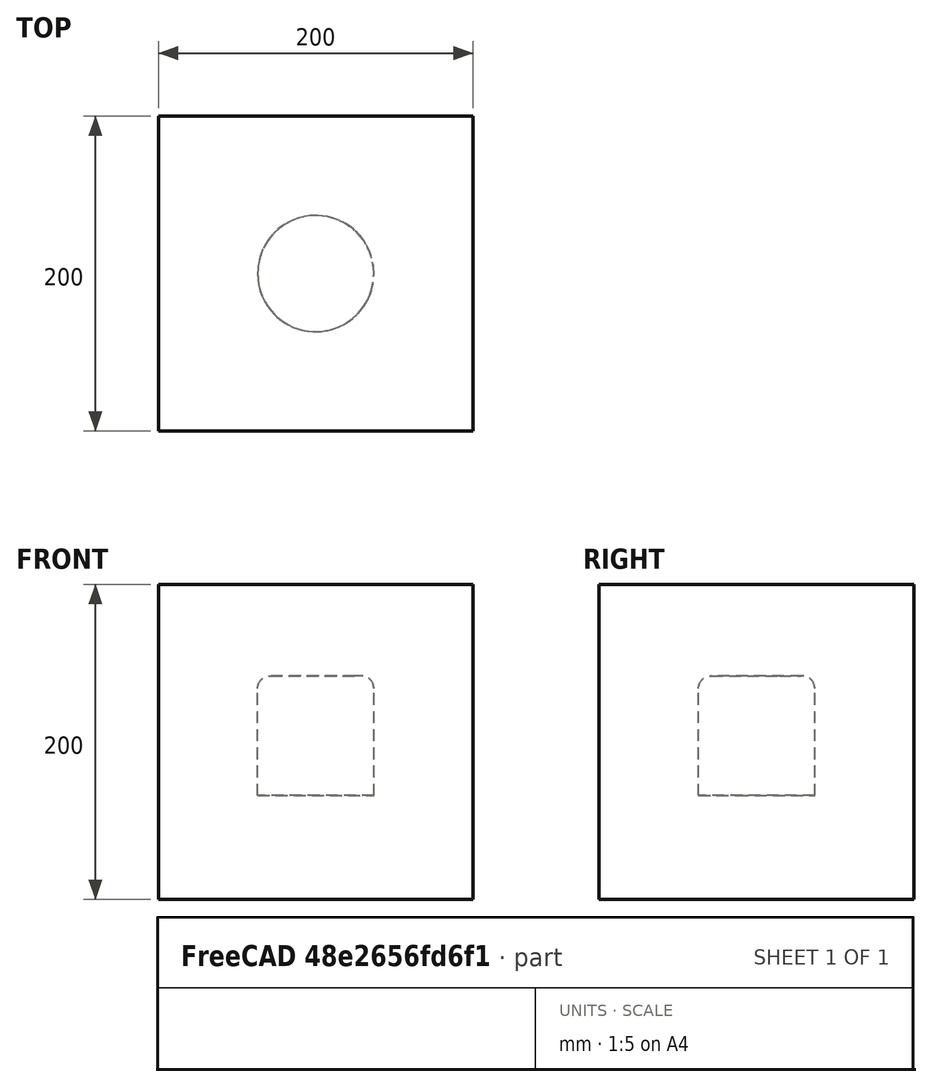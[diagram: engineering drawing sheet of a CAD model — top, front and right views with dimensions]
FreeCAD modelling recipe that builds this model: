
FCSTD DOCUMENT  (FreeCAD 0.21R33694 (Git))
Label: assemblyTest-B
License: All rights reserved
LicenseURL: http://en.wikipedia.org/wiki/All_rights_reserved
objects: App::DocumentObjectGroupPython×1254, Part::FeaturePython×4, App::Part×3, Part::Fuse×2
note: 6 computed .brp shape members not serialized (recipe doc carries the construction recipe); baked Part::Feature solids carry a one-line shape summary decoded from their .brp

FEATURE [App::DocumentObjectGroupPython] HALFPI  # scripted group (container) (typed FeaturePython)
  name = HALFPI
  value = pi/2.
FEATURE [App::DocumentObjectGroupPython] PI  # scripted group (container) (typed FeaturePython)
  name = PI
  value = 1.*pi
FEATURE [App::DocumentObjectGroupPython] TWOPI  # scripted group (container) (typed FeaturePython)
  name = TWOPI
  value = 2.*pi
FEATURE [App::DocumentObjectGroupPython] Variables  # scripted group (container) (typed FeaturePython)
FEATURE [App::DocumentObjectGroupPython] Quantities  # scripted group (container) (typed FeaturePython)
FEATURE [App::DocumentObjectGroupPython] Isotopes  # scripted group (container) (typed FeaturePython)
FEATURE [App::DocumentObjectGroupPython] Elements  # scripted group (container) (typed FeaturePython)
FEATURE [App::DocumentObjectGroupPython] G4Isotopes  # scripted group (container) (typed FeaturePython)
FEATURE [App::DocumentObjectGroupPython] H_element  # scripted group (container) (typed FeaturePython)
  Z = 1
  atom_value = 1.008
  formula = H
  name = H_element
FEATURE [App::DocumentObjectGroupPython] He_element  # scripted group (container) (typed FeaturePython)
  Z = 2
  atom_value = 4.0026
  formula = He
  name = He_element
FEATURE [App::DocumentObjectGroupPython] Li_element  # scripted group (container) (typed FeaturePython)
  Z = 3
  atom_value = 6.94
  formula = Li
  name = Li_element
FEATURE [App::DocumentObjectGroupPython] Be_element  # scripted group (container) (typed FeaturePython)
  Z = 4
  atom_value = 9.01218
  formula = Be
  name = Be_element
FEATURE [App::DocumentObjectGroupPython] B_element  # scripted group (container) (typed FeaturePython)
  Z = 5
  atom_value = 10.81
  formula = B
  name = B_element
FEATURE [App::DocumentObjectGroupPython] C_element  # scripted group (container) (typed FeaturePython)
  Z = 6
  atom_value = 12.011
  formula = C
  name = C_element
FEATURE [App::DocumentObjectGroupPython] N_element  # scripted group (container) (typed FeaturePython)
  Z = 7
  atom_value = 14.007
  formula = N
  name = N_element
FEATURE [App::DocumentObjectGroupPython] O_element  # scripted group (container) (typed FeaturePython)
  Z = 8
  atom_value = 15.999
  formula = O
  name = O_element
FEATURE [App::DocumentObjectGroupPython] F_element  # scripted group (container) (typed FeaturePython)
  Z = 9
  atom_value = 18.9984
  formula = F
  name = F_element
FEATURE [App::DocumentObjectGroupPython] Ne_element  # scripted group (container) (typed FeaturePython)
  Z = 10
  atom_value = 20.1797
  formula = Ne
  name = Ne_element
FEATURE [App::DocumentObjectGroupPython] Na_element  # scripted group (container) (typed FeaturePython)
  Z = 11
  atom_value = 22.9898
  formula = Na
  name = Na_element
FEATURE [App::DocumentObjectGroupPython] Mg_element  # scripted group (container) (typed FeaturePython)
  Z = 12
  atom_value = 24.305
  formula = Mg
  name = Mg_element
FEATURE [App::DocumentObjectGroupPython] Al_element  # scripted group (container) (typed FeaturePython)
  Z = 13
  atom_value = 26.9815
  formula = Al
  name = Al_element
FEATURE [App::DocumentObjectGroupPython] Si_element  # scripted group (container) (typed FeaturePython)
  Z = 14
  atom_value = 28.085
  formula = Si
  name = Si_element
FEATURE [App::DocumentObjectGroupPython] P_element  # scripted group (container) (typed FeaturePython)
  Z = 15
  atom_value = 30.9738
  formula = P
  name = P_element
FEATURE [App::DocumentObjectGroupPython] S_element  # scripted group (container) (typed FeaturePython)
  Z = 16
  atom_value = 32.06
  formula = S
  name = S_element
FEATURE [App::DocumentObjectGroupPython] Cl_element  # scripted group (container) (typed FeaturePython)
  Z = 17
  atom_value = 35.45
  formula = Cl
  name = Cl_element
FEATURE [App::DocumentObjectGroupPython] Ar_element  # scripted group (container) (typed FeaturePython)
  Z = 18
  atom_value = 39.95
  formula = Ar
  name = Ar_element
FEATURE [App::DocumentObjectGroupPython] K_element  # scripted group (container) (typed FeaturePython)
  Z = 19
  atom_value = 39.0983
  formula = K
  name = K_element
FEATURE [App::DocumentObjectGroupPython] Ca_element  # scripted group (container) (typed FeaturePython)
  Z = 20
  atom_value = 40.078
  formula = Ca
  name = Ca_element
FEATURE [App::DocumentObjectGroupPython] Sc_element  # scripted group (container) (typed FeaturePython)
  Z = 21
  atom_value = 44.9559
  formula = Sc
  name = Sc_element
FEATURE [App::DocumentObjectGroupPython] Ti_element  # scripted group (container) (typed FeaturePython)
  Z = 22
  atom_value = 47.867
  formula = Ti
  name = Ti_element
FEATURE [App::DocumentObjectGroupPython] V_element  # scripted group (container) (typed FeaturePython)
  Z = 23
  atom_value = 50.9415
  formula = V
  name = V_element
FEATURE [App::DocumentObjectGroupPython] Cr_element  # scripted group (container) (typed FeaturePython)
  Z = 24
  atom_value = 51.9961
  formula = Cr
  name = Cr_element
FEATURE [App::DocumentObjectGroupPython] Mn_element  # scripted group (container) (typed FeaturePython)
  Z = 25
  atom_value = 54.938
  formula = Mn
  name = Mn_element
FEATURE [App::DocumentObjectGroupPython] Fe_element  # scripted group (container) (typed FeaturePython)
  Z = 26
  atom_value = 55.845
  formula = Fe
  name = Fe_element
FEATURE [App::DocumentObjectGroupPython] Co_element  # scripted group (container) (typed FeaturePython)
  Z = 27
  atom_value = 58.9332
  formula = Co
  name = Co_element
FEATURE [App::DocumentObjectGroupPython] Ni_element  # scripted group (container) (typed FeaturePython)
  Z = 28
  atom_value = 58.6934
  formula = Ni
  name = Ni_element
FEATURE [App::DocumentObjectGroupPython] Cu_element  # scripted group (container) (typed FeaturePython)
  Z = 29
  atom_value = 63.546
  formula = Cu
  name = Cu_element
FEATURE [App::DocumentObjectGroupPython] Zn_element  # scripted group (container) (typed FeaturePython)
  Z = 30
  atom_value = 65.38
  formula = Zn
  name = Zn_element
FEATURE [App::DocumentObjectGroupPython] Ga_element  # scripted group (container) (typed FeaturePython)
  Z = 31
  atom_value = 69.723
  formula = Ga
  name = Ga_element
FEATURE [App::DocumentObjectGroupPython] Ge_element  # scripted group (container) (typed FeaturePython)
  Z = 32
  atom_value = 72.63
  formula = Ge
  name = Ge_element
FEATURE [App::DocumentObjectGroupPython] As_element  # scripted group (container) (typed FeaturePython)
  Z = 33
  atom_value = 74.9216
  formula = As
  name = As_element
FEATURE [App::DocumentObjectGroupPython] Se_element  # scripted group (container) (typed FeaturePython)
  Z = 34
  atom_value = 78.971
  formula = Se
  name = Se_element
FEATURE [App::DocumentObjectGroupPython] Br_element  # scripted group (container) (typed FeaturePython)
  Z = 35
  atom_value = 79.904
  formula = Br
  name = Br_element
FEATURE [App::DocumentObjectGroupPython] Kr_element  # scripted group (container) (typed FeaturePython)
  Z = 36
  atom_value = 83.798
  formula = Kr
  name = Kr_element
FEATURE [App::DocumentObjectGroupPython] Rb_element  # scripted group (container) (typed FeaturePython)
  Z = 37
  atom_value = 85.4678
  formula = Rb
  name = Rb_element
FEATURE [App::DocumentObjectGroupPython] Sr_element  # scripted group (container) (typed FeaturePython)
  Z = 38
  atom_value = 87.62
  formula = Sr
  name = Sr_element
FEATURE [App::DocumentObjectGroupPython] Y_element  # scripted group (container) (typed FeaturePython)
  Z = 39
  atom_value = 88.9058
  formula = Y
  name = Y_element
FEATURE [App::DocumentObjectGroupPython] Zr_element  # scripted group (container) (typed FeaturePython)
  Z = 40
  atom_value = 91.224
  formula = Zr
  name = Zr_element
FEATURE [App::DocumentObjectGroupPython] Nb_element  # scripted group (container) (typed FeaturePython)
  Z = 41
  atom_value = 92.9064
  formula = Nb
  name = Nb_element
FEATURE [App::DocumentObjectGroupPython] Mo_element  # scripted group (container) (typed FeaturePython)
  Z = 42
  atom_value = 95.95
  formula = Mo
  name = Mo_element
FEATURE [App::DocumentObjectGroupPython] Tc_element  # scripted group (container) (typed FeaturePython)
  Z = 43
  atom_value = 97
  formula = Tc
  name = Tc_element
FEATURE [App::DocumentObjectGroupPython] Ru_element  # scripted group (container) (typed FeaturePython)
  Z = 44
  atom_value = 101.07
  formula = Ru
  name = Ru_element
FEATURE [App::DocumentObjectGroupPython] Rh_element  # scripted group (container) (typed FeaturePython)
  Z = 45
  atom_value = 102.905
  formula = Rh
  name = Rh_element
FEATURE [App::DocumentObjectGroupPython] Pd_element  # scripted group (container) (typed FeaturePython)
  Z = 46
  atom_value = 106.42
  formula = Pd
  name = Pd_element
FEATURE [App::DocumentObjectGroupPython] Ag_element  # scripted group (container) (typed FeaturePython)
  Z = 47
  atom_value = 107.868
  formula = Ag
  name = Ag_element
FEATURE [App::DocumentObjectGroupPython] Cd_element  # scripted group (container) (typed FeaturePython)
  Z = 48
  atom_value = 112.414
  formula = Cd
  name = Cd_element
FEATURE [App::DocumentObjectGroupPython] In_element  # scripted group (container) (typed FeaturePython)
  Z = 49
  atom_value = 114.818
  formula = In
  name = In_element
FEATURE [App::DocumentObjectGroupPython] Sn_element  # scripted group (container) (typed FeaturePython)
  Z = 50
  atom_value = 118.71
  formula = Sn
  name = Sn_element
FEATURE [App::DocumentObjectGroupPython] Sb_element  # scripted group (container) (typed FeaturePython)
  Z = 51
  atom_value = 121.76
  formula = Sb
  name = Sb_element
FEATURE [App::DocumentObjectGroupPython] Te_element  # scripted group (container) (typed FeaturePython)
  Z = 52
  atom_value = 127.6
  formula = Te
  name = Te_element
FEATURE [App::DocumentObjectGroupPython] I_element  # scripted group (container) (typed FeaturePython)
  Z = 53
  atom_value = 126.904
  formula = I
  name = I_element
FEATURE [App::DocumentObjectGroupPython] Xe_element  # scripted group (container) (typed FeaturePython)
  Z = 54
  atom_value = 131.293
  formula = Xe
  name = Xe_element
FEATURE [App::DocumentObjectGroupPython] Cs_element  # scripted group (container) (typed FeaturePython)
  Z = 55
  atom_value = 132.905
  formula = Cs
  name = Cs_element
FEATURE [App::DocumentObjectGroupPython] Ba_element  # scripted group (container) (typed FeaturePython)
  Z = 56
  atom_value = 137.327
  formula = Ba
  name = Ba_element
FEATURE [App::DocumentObjectGroupPython] La_element  # scripted group (container) (typed FeaturePython)
  Z = 57
  atom_value = 138.905
  formula = La
  name = La_element
FEATURE [App::DocumentObjectGroupPython] Ce_element  # scripted group (container) (typed FeaturePython)
  Z = 58
  atom_value = 140.116
  formula = Ce
  name = Ce_element
FEATURE [App::DocumentObjectGroupPython] Pr_element  # scripted group (container) (typed FeaturePython)
  Z = 59
  atom_value = 140.908
  formula = Pr
  name = Pr_element
FEATURE [App::DocumentObjectGroupPython] Nd_element  # scripted group (container) (typed FeaturePython)
  Z = 60
  atom_value = 144.242
  formula = Nd
  name = Nd_element
FEATURE [App::DocumentObjectGroupPython] Pm_element  # scripted group (container) (typed FeaturePython)
  Z = 61
  atom_value = 145
  formula = Pm
  name = Pm_element
FEATURE [App::DocumentObjectGroupPython] Sm_element  # scripted group (container) (typed FeaturePython)
  Z = 62
  atom_value = 150.36
  formula = Sm
  name = Sm_element
FEATURE [App::DocumentObjectGroupPython] Eu_element  # scripted group (container) (typed FeaturePython)
  Z = 63
  atom_value = 151.964
  formula = Eu
  name = Eu_element
FEATURE [App::DocumentObjectGroupPython] Gd_element  # scripted group (container) (typed FeaturePython)
  Z = 64
  atom_value = 157.25
  formula = Gd
  name = Gd_element
FEATURE [App::DocumentObjectGroupPython] Tb_element  # scripted group (container) (typed FeaturePython)
  Z = 65
  atom_value = 158.925
  formula = Tb
  name = Tb_element
FEATURE [App::DocumentObjectGroupPython] Dy_element  # scripted group (container) (typed FeaturePython)
  Z = 66
  atom_value = 162.5
  formula = Dy
  name = Dy_element
FEATURE [App::DocumentObjectGroupPython] Ho_element  # scripted group (container) (typed FeaturePython)
  Z = 67
  atom_value = 164.93
  formula = Ho
  name = Ho_element
FEATURE [App::DocumentObjectGroupPython] Er_element  # scripted group (container) (typed FeaturePython)
  Z = 68
  atom_value = 167.259
  formula = Er
  name = Er_element
FEATURE [App::DocumentObjectGroupPython] Tm_element  # scripted group (container) (typed FeaturePython)
  Z = 69
  atom_value = 168.934
  formula = Tm
  name = Tm_element
FEATURE [App::DocumentObjectGroupPython] Yb_element  # scripted group (container) (typed FeaturePython)
  Z = 70
  atom_value = 173.045
  formula = Yb
  name = Yb_element
FEATURE [App::DocumentObjectGroupPython] Lu_element  # scripted group (container) (typed FeaturePython)
  Z = 71
  atom_value = 174.967
  formula = Lu
  name = Lu_element
FEATURE [App::DocumentObjectGroupPython] Hf_element  # scripted group (container) (typed FeaturePython)
  Z = 72
  atom_value = 178.49
  formula = Hf
  name = Hf_element
FEATURE [App::DocumentObjectGroupPython] Ta_element  # scripted group (container) (typed FeaturePython)
  Z = 73
  atom_value = 180.948
  formula = Ta
  name = Ta_element
FEATURE [App::DocumentObjectGroupPython] W_element  # scripted group (container) (typed FeaturePython)
  Z = 74
  atom_value = 183.84
  formula = W
  name = W_element
FEATURE [App::DocumentObjectGroupPython] Re_element  # scripted group (container) (typed FeaturePython)
  Z = 75
  atom_value = 186.207
  formula = Re
  name = Re_element
FEATURE [App::DocumentObjectGroupPython] Os_element  # scripted group (container) (typed FeaturePython)
  Z = 76
  atom_value = 190.23
  formula = Os
  name = Os_element
FEATURE [App::DocumentObjectGroupPython] Ir_element  # scripted group (container) (typed FeaturePython)
  Z = 77
  atom_value = 192.217
  formula = Ir
  name = Ir_element
FEATURE [App::DocumentObjectGroupPython] Pt_element  # scripted group (container) (typed FeaturePython)
  Z = 78
  atom_value = 195.084
  formula = Pt
  name = Pt_element
FEATURE [App::DocumentObjectGroupPython] Au_element  # scripted group (container) (typed FeaturePython)
  Z = 79
  atom_value = 196.967
  formula = Au
  name = Au_element
FEATURE [App::DocumentObjectGroupPython] Hg_element  # scripted group (container) (typed FeaturePython)
  Z = 80
  atom_value = 200.592
  formula = Hg
  name = Hg_element
FEATURE [App::DocumentObjectGroupPython] Tl_element  # scripted group (container) (typed FeaturePython)
  Z = 81
  atom_value = 204.38
  formula = Tl
  name = Tl_element
FEATURE [App::DocumentObjectGroupPython] Pb_element  # scripted group (container) (typed FeaturePython)
  Z = 82
  atom_value = 207.2
  formula = Pb
  name = Pb_element
FEATURE [App::DocumentObjectGroupPython] Bi_element  # scripted group (container) (typed FeaturePython)
  Z = 83
  atom_value = 208.98
  formula = Bi
  name = Bi_element
FEATURE [App::DocumentObjectGroupPython] Po_element  # scripted group (container) (typed FeaturePython)
  Z = 84
  atom_value = 209
  formula = Po
  name = Po_element
FEATURE [App::DocumentObjectGroupPython] At_element  # scripted group (container) (typed FeaturePython)
  Z = 85
  atom_value = 210
  formula = At
  name = At_element
FEATURE [App::DocumentObjectGroupPython] Rn_element  # scripted group (container) (typed FeaturePython)
  Z = 86
  atom_value = 222
  formula = Rn
  name = Rn_element
FEATURE [App::DocumentObjectGroupPython] Fr_element  # scripted group (container) (typed FeaturePython)
  Z = 87
  atom_value = 223
  formula = Fr
  name = Fr_element
FEATURE [App::DocumentObjectGroupPython] Ra_element  # scripted group (container) (typed FeaturePython)
  Z = 88
  atom_value = 226
  formula = Ra
  name = Ra_element
FEATURE [App::DocumentObjectGroupPython] Ac_element  # scripted group (container) (typed FeaturePython)
  Z = 89
  atom_value = 227
  formula = Ac
  name = Ac_element
FEATURE [App::DocumentObjectGroupPython] Th_element  # scripted group (container) (typed FeaturePython)
  Z = 90
  atom_value = 232.038
  formula = Th
  name = Th_element
FEATURE [App::DocumentObjectGroupPython] Pa_element  # scripted group (container) (typed FeaturePython)
  Z = 91
  atom_value = 231.036
  formula = Pa
  name = Pa_element
FEATURE [App::DocumentObjectGroupPython] U_element  # scripted group (container) (typed FeaturePython)
  Z = 92
  atom_value = 238.029
  formula = U
  name = U_element
FEATURE [App::DocumentObjectGroupPython] Np_element  # scripted group (container) (typed FeaturePython)
  Z = 93
  atom_value = 237
  formula = Np
  name = Np_element
FEATURE [App::DocumentObjectGroupPython] Pu_element  # scripted group (container) (typed FeaturePython)
  Z = 94
  atom_value = 244
  formula = Pu
  name = Pu_element
FEATURE [App::DocumentObjectGroupPython] Am_element  # scripted group (container) (typed FeaturePython)
  Z = 95
  atom_value = 243
  formula = Am
  name = Am_element
FEATURE [App::DocumentObjectGroupPython] Cm_element  # scripted group (container) (typed FeaturePython)
  Z = 96
  atom_value = 247
  formula = Cm
  name = Cm_element
FEATURE [App::DocumentObjectGroupPython] Bk_element  # scripted group (container) (typed FeaturePython)
  Z = 97
  atom_value = 247
  formula = Bk
  name = Bk_element
FEATURE [App::DocumentObjectGroupPython] Cf_element  # scripted group (container) (typed FeaturePython)
  Z = 98
  atom_value = 251
  formula = Cf
  name = Cf_element
FEATURE [App::DocumentObjectGroupPython] G4Elements  # scripted group (container) (typed FeaturePython)
  Group = -> [H_element,He_element,Li_element,Be_element,B_element,C_element,N_element,O_element,F_element,Ne_element,Na_element,Mg_element,Al_element,Si_element,P_element,S_element,Cl_element,Ar_element,K_element,Ca_element,Sc_element,Ti_element,V_element,Cr_element,Mn_element,Fe_element,Co_element,Ni_element,Cu_element,Zn_element,Ga_element,Ge_element,As_element,Se_element,Br_element,Kr_element,Rb_element,+61 more]
FEATURE [Part::FeaturePython] GDMLBox_WorldBox  # WARN: FeaturePython — macro-defined, semantics opaque (R4)
  lunit = 2
  material = 5
  x = 200
  y = 200
  z = 200
FEATURE [App::DocumentObjectGroupPython] HALFPI001  # scripted group (container) (typed FeaturePython)
  name = HALFPI
  value = pi/2.
FEATURE [App::DocumentObjectGroupPython] PI001  # scripted group (container) (typed FeaturePython)
  name = PI
  value = 1.*pi
FEATURE [App::DocumentObjectGroupPython] TWOPI001  # scripted group (container) (typed FeaturePython)
  name = TWOPI
  value = 2.*pi
FEATURE [App::DocumentObjectGroupPython] HALFPI001001  # scripted group (container) (typed FeaturePython)
  name = HALFPI001
  value = pi/2.
FEATURE [App::DocumentObjectGroupPython] PI001001  # scripted group (container) (typed FeaturePython)
  name = PI001
  value = 1.*pi
FEATURE [App::DocumentObjectGroupPython] TWOPI001001  # scripted group (container) (typed FeaturePython)
  name = TWOPI001
  value = 2.*pi
FEATURE [App::DocumentObjectGroupPython] Constants  # scripted group (container) (typed FeaturePython)
  Group = -> [HALFPI,PI,TWOPI,HALFPI001,PI001,TWOPI001,HALFPI001001,PI001001,TWOPI001001]
FEATURE [Part::FeaturePython] GDMLTorus_Torus  # WARN: FeaturePython — macro-defined, semantics opaque (R4)
  aunit = deg
  deltaphi = 360
  lunit = 2
  material = 0
  rmax = 8
  rmin = 0
  rtor = 28.9
  startphi = 0
FEATURE [Part::FeaturePython] GDMLTube_Tube  # WARN: FeaturePython — macro-defined, semantics opaque (R4)
  aunit = 1
  deltaphi = 360
  lunit = 2
  material = 0
  rmax = 28.9
  rmin = 0
  startphi = 0
  z = 16
FEATURE [Part::FeaturePython] GDMLTube_Tube001  label="GDMLTube_T_1"  # WARN: FeaturePython — macro-defined, semantics opaque (R4)
  Placement = pos=(0,0,-34) rot=(0,0,-1;0.349066rad)
  aunit = 1
  deltaphi = 360
  lunit = 2
  material = 0
  rmax = 36.9
  rmin = 0
  startphi = 0
  z = 68
FEATURE [Part::Fuse] Union
  Base = -> GDMLTorus_Torus
  Placement = pos=(0,0,0) rot=(0,0,1;0.523599rad)
  Tool = -> GDMLTube_Tube
FEATURE [Part::Fuse] Union001  label="U1"
  Base = -> Union
  Placement = pos=(0,0,34) rot=(0,0,1;0rad)
  Tool = -> GDMLTube_Tube001
  material = 211
FEATURE [App::Part] Bool_Union001  label="Detector"
  Group = -> [GDMLTorus_Torus,GDMLTube_Tube,Union,GDMLTube_Tube001,Union001]
  Origin = -> Origin005
FEATURE [App::Part] Part  label="DetectorAssembly"
  Group = -> [Bool_Union001]
  Origin = -> Origin007
FEATURE [App::Part] worldVOL
  Group = -> [GDMLBox_WorldBox,Part]
  Origin = -> Origin
FEATURE [App::DocumentObjectGroupPython] H_element553  label="H_element : 0.246"  # scripted group (container) (typed FeaturePython)
  n = 0.101327
FEATURE [App::DocumentObjectGroupPython] C_element593  label="C_element : 0.974"  # scripted group (container) (typed FeaturePython)
  n = 0.7755
FEATURE [App::DocumentObjectGroupPython] N_element273  label="N_element : 0.828"  # scripted group (container) (typed FeaturePython)
  n = 0.035057
FEATURE [App::DocumentObjectGroupPython] O_element521  label="O_element : 0.966"  # scripted group (container) (typed FeaturePython)
  n = 0.0523159
FEATURE [App::DocumentObjectGroupPython] F_element077  label="F_element : 0.727"  # scripted group (container) (typed FeaturePython)
  n = 0.017422
FEATURE [App::DocumentObjectGroupPython] Ca_element057  label="Ca_element : 0.240"  # scripted group (container) (typed FeaturePython)
  n = 0.018378
FEATURE [App::DocumentObjectGroupPython] G4_A_150_TISSUE  label="G4_A-150_TISSUE"  # scripted group (container) (typed FeaturePython)
  Dunit = g/cm3
  Dvalue = 1.127
  Group = -> [H_element553,C_element593,N_element273,O_element521,F_element077,Ca_element057]
  conduct = 2
  density = 1
  expand = 3
  formula = G4_A-150_TISSUE
  name = G4_A-150_TISSUE
  specific = 4
FEATURE [App::DocumentObjectGroupPython] C_element594  label="C_element : 390"  # scripted group (container) (typed FeaturePython)
  n = 3
  ref = C_element
FEATURE [App::DocumentObjectGroupPython] H_element554  label="H_element : 358"  # scripted group (container) (typed FeaturePython)
  n = 6
  ref = H_element
FEATURE [App::DocumentObjectGroupPython] O_element522  label="O_element : 335"  # scripted group (container) (typed FeaturePython)
  n = 1
  ref = O_element
FEATURE [App::DocumentObjectGroupPython] G4_ACETONE  # scripted group (container) (typed FeaturePython)
  Dunit = g/cm3
  Dvalue = 0.7899
  Group = -> [C_element594,H_element554,O_element522]
  conduct = 2
  density = 1
  expand = 3
  formula = G4_ACETONE
  name = G4_ACETONE
  specific = 4
FEATURE [App::DocumentObjectGroupPython] C_element595  label="C_element : 391"  # scripted group (container) (typed FeaturePython)
  n = 2
  ref = C_element
FEATURE [App::DocumentObjectGroupPython] H_element555  label="H_element : 359"  # scripted group (container) (typed FeaturePython)
  n = 2
  ref = H_element
FEATURE [App::DocumentObjectGroupPython] G4_ACETYLENE  # scripted group (container) (typed FeaturePython)
  Dunit = g/cm3
  Dvalue = 0.0010967
  Group = -> [C_element595,H_element555]
  conduct = 2
  density = 1
  expand = 3
  formula = G4_ACETYLENE
  name = G4_ACETYLENE
  specific = 4
FEATURE [App::DocumentObjectGroupPython] C_element596  label="C_element : 392"  # scripted group (container) (typed FeaturePython)
  n = 5
  ref = C_element
FEATURE [App::DocumentObjectGroupPython] H_element556  label="H_element : 360"  # scripted group (container) (typed FeaturePython)
  n = 5
  ref = H_element
FEATURE [App::DocumentObjectGroupPython] N_element274  label="N_element : 154"  # scripted group (container) (typed FeaturePython)
  n = 5
  ref = N_element
FEATURE [App::DocumentObjectGroupPython] G4_ADENINE  # scripted group (container) (typed FeaturePython)
  Dunit = g/cm3
  Dvalue = 1.6
  Group = -> [C_element596,H_element556,N_element274]
  conduct = 2
  density = 1
  expand = 3
  formula = G4_ADENINE
  name = G4_ADENINE
  specific = 4
FEATURE [App::DocumentObjectGroupPython] H_element557  label="H_element : 0.247"  # scripted group (container) (typed FeaturePython)
  n = 0.114
FEATURE [App::DocumentObjectGroupPython] C_element597  label="C_element : 0.975"  # scripted group (container) (typed FeaturePython)
  n = 0.598
FEATURE [App::DocumentObjectGroupPython] N_element275  label="N_element : 0.829"  # scripted group (container) (typed FeaturePython)
  n = 0.007
FEATURE [App::DocumentObjectGroupPython] O_element523  label="O_element : 0.967"  # scripted group (container) (typed FeaturePython)
  n = 0.278
FEATURE [App::DocumentObjectGroupPython] Na_element081  label="Na_element : 0.142"  # scripted group (container) (typed FeaturePython)
  n = 0.001
FEATURE [App::DocumentObjectGroupPython] S_element093  label="S_element : 0.065"  # scripted group (container) (typed FeaturePython)
  n = 0.001
FEATURE [App::DocumentObjectGroupPython] Cl_element121  label="Cl_element : 0.627"  # scripted group (container) (typed FeaturePython)
  n = 0.001
FEATURE [App::DocumentObjectGroupPython] G4_ADIPOSE_TISSUE_ICRP  # scripted group (container) (typed FeaturePython)
  Dunit = g/cm3
  Dvalue = 0.95
  Group = -> [H_element557,C_element597,N_element275,O_element523,Na_element081,S_element093,Cl_element121]
  conduct = 2
  density = 1
  expand = 3
  formula = G4_ADIPOSE_TISSUE_ICRP
  name = G4_ADIPOSE_TISSUE_ICRP
  specific = 4
FEATURE [App::DocumentObjectGroupPython] C_element598  label="C_element : 0.976"  # scripted group (container) (typed FeaturePython)
  n = 0.000124
FEATURE [App::DocumentObjectGroupPython] N_element276  label="N_element : 0.830"  # scripted group (container) (typed FeaturePython)
  n = 0.755268
FEATURE [App::DocumentObjectGroupPython] O_element524  label="O_element : 0.968"  # scripted group (container) (typed FeaturePython)
  n = 0.231781
FEATURE [App::DocumentObjectGroupPython] Ar_element009  label="Ar_element : 0.016"  # scripted group (container) (typed FeaturePython)
  n = 0.012827
FEATURE [App::DocumentObjectGroupPython] G4_AIR  # scripted group (container) (typed FeaturePython)
  Dunit = g/cm3
  Dvalue = 0.00120479
  Group = -> [C_element598,N_element276,O_element524,Ar_element009]
  conduct = 2
  density = 1
  expand = 3
  formula = G4_AIR
  name = G4_AIR
  specific = 4
FEATURE [App::DocumentObjectGroupPython] C_element599  label="C_element : 393"  # scripted group (container) (typed FeaturePython)
  n = 3
  ref = C_element
FEATURE [App::DocumentObjectGroupPython] H_element558  label="H_element : 361"  # scripted group (container) (typed FeaturePython)
  n = 7
  ref = H_element
FEATURE [App::DocumentObjectGroupPython] N_element277  label="N_element : 155"  # scripted group (container) (typed FeaturePython)
  n = 1
  ref = N_element
FEATURE [App::DocumentObjectGroupPython] O_element525  label="O_element : 336"  # scripted group (container) (typed FeaturePython)
  n = 2
  ref = O_element
FEATURE [App::DocumentObjectGroupPython] G4_ALANINE  # scripted group (container) (typed FeaturePython)
  Dunit = g/cm3
  Dvalue = 1.42
  Group = -> [C_element599,H_element558,N_element277,O_element525]
  conduct = 2
  density = 1
  expand = 3
  formula = G4_ALANINE
  name = G4_ALANINE
  specific = 4
FEATURE [App::DocumentObjectGroupPython] Al_element017  label="Al_element : 007"  # scripted group (container) (typed FeaturePython)
  n = 2
  ref = Al_element
FEATURE [App::DocumentObjectGroupPython] O_element526  label="O_element : 337"  # scripted group (container) (typed FeaturePython)
  n = 3
  ref = O_element
FEATURE [App::DocumentObjectGroupPython] G4_ALUMINUM_OXIDE  # scripted group (container) (typed FeaturePython)
  Dunit = g/cm3
  Dvalue = 3.97
  Group = -> [Al_element017,O_element526]
  conduct = 2
  density = 1
  expand = 3
  formula = G4_ALUMINUM_OXIDE
  name = G4_ALUMINUM_OXIDE
  specific = 4
FEATURE [App::DocumentObjectGroupPython] H_element559  label="H_element : 0.248"  # scripted group (container) (typed FeaturePython)
  n = 0.10593
FEATURE [App::DocumentObjectGroupPython] C_element600  label="C_element : 0.977"  # scripted group (container) (typed FeaturePython)
  n = 0.788974
FEATURE [App::DocumentObjectGroupPython] O_element527  label="O_element : 0.969"  # scripted group (container) (typed FeaturePython)
  n = 0.105096
FEATURE [App::DocumentObjectGroupPython] G4_AMBER  # scripted group (container) (typed FeaturePython)
  Dunit = g/cm3
  Dvalue = 1.1
  Group = -> [H_element559,C_element600,O_element527]
  conduct = 2
  density = 1
  expand = 3
  formula = G4_AMBER
  name = G4_AMBER
  specific = 4
FEATURE [App::DocumentObjectGroupPython] N_element278  label="N_element : 156"  # scripted group (container) (typed FeaturePython)
  n = 1
  ref = N_element
FEATURE [App::DocumentObjectGroupPython] H_element560  label="H_element : 362"  # scripted group (container) (typed FeaturePython)
  n = 3
  ref = H_element
FEATURE [App::DocumentObjectGroupPython] G4_AMMONIA  # scripted group (container) (typed FeaturePython)
  Dunit = g/cm3
  Dvalue = 0.000826019
  Group = -> [N_element278,H_element560]
  conduct = 2
  density = 1
  expand = 3
  formula = G4_AMMONIA
  name = G4_AMMONIA
  specific = 4
FEATURE [App::DocumentObjectGroupPython] C_element601  label="C_element : 394"  # scripted group (container) (typed FeaturePython)
  n = 6
  ref = C_element
FEATURE [App::DocumentObjectGroupPython] H_element561  label="H_element : 363"  # scripted group (container) (typed FeaturePython)
  n = 7
  ref = H_element
FEATURE [App::DocumentObjectGroupPython] N_element279  label="N_element : 157"  # scripted group (container) (typed FeaturePython)
  n = 1
  ref = N_element
FEATURE [App::DocumentObjectGroupPython] G4_ANILINE  # scripted group (container) (typed FeaturePython)
  Dunit = g/cm3
  Dvalue = 1.0235
  Group = -> [C_element601,H_element561,N_element279]
  conduct = 2
  density = 1
  expand = 3
  formula = G4_ANILINE
  name = G4_ANILINE
  specific = 4
FEATURE [App::DocumentObjectGroupPython] C_element602  label="C_element : 395"  # scripted group (container) (typed FeaturePython)
  n = 14
  ref = C_element
FEATURE [App::DocumentObjectGroupPython] H_element562  label="H_element : 364"  # scripted group (container) (typed FeaturePython)
  n = 10
  ref = H_element
FEATURE [App::DocumentObjectGroupPython] G4_ANTHRACENE  # scripted group (container) (typed FeaturePython)
  Dunit = g/cm3
  Dvalue = 1.283
  Group = -> [C_element602,H_element562]
  conduct = 2
  density = 1
  expand = 3
  formula = G4_ANTHRACENE
  name = G4_ANTHRACENE
  specific = 4
FEATURE [App::DocumentObjectGroupPython] H_element563  label="H_element : 0.249"  # scripted group (container) (typed FeaturePython)
  n = 0.0654709
FEATURE [App::DocumentObjectGroupPython] C_element603  label="C_element : 0.978"  # scripted group (container) (typed FeaturePython)
  n = 0.536944
FEATURE [App::DocumentObjectGroupPython] N_element280  label="N_element : 0.831"  # scripted group (container) (typed FeaturePython)
  n = 0.0215
FEATURE [App::DocumentObjectGroupPython] O_element528  label="O_element : 0.970"  # scripted group (container) (typed FeaturePython)
  n = 0.032085
FEATURE [App::DocumentObjectGroupPython] F_element078  label="F_element : 0.728"  # scripted group (container) (typed FeaturePython)
  n = 0.167411
FEATURE [App::DocumentObjectGroupPython] Ca_element058  label="Ca_element : 0.241"  # scripted group (container) (typed FeaturePython)
  n = 0.176589
FEATURE [App::DocumentObjectGroupPython] G4_B_100_BONE  label="G4_B-100_BONE"  # scripted group (container) (typed FeaturePython)
  Dunit = g/cm3
  Dvalue = 1.45
  Group = -> [H_element563,C_element603,N_element280,O_element528,F_element078,Ca_element058]
  conduct = 2
  density = 1
  expand = 3
  formula = G4_B-100_BONE
  name = G4_B-100_BONE
  specific = 4
FEATURE [App::DocumentObjectGroupPython] H_element564  label="H_element : 0.250"  # scripted group (container) (typed FeaturePython)
  n = 0.057441
FEATURE [App::DocumentObjectGroupPython] C_element604  label="C_element : 0.979"  # scripted group (container) (typed FeaturePython)
  n = 0.774591
FEATURE [App::DocumentObjectGroupPython] O_element529  label="O_element : 0.971"  # scripted group (container) (typed FeaturePython)
  n = 0.167968
FEATURE [App::DocumentObjectGroupPython] G4_BAKELITE  # scripted group (container) (typed FeaturePython)
  Dunit = g/cm3
  Dvalue = 1.25
  Group = -> [H_element564,C_element604,O_element529]
  conduct = 2
  density = 1
  expand = 3
  formula = G4_BAKELITE
  name = G4_BAKELITE
  specific = 4
FEATURE [App::DocumentObjectGroupPython] Ba_element013  label="Ba_element : 012"  # scripted group (container) (typed FeaturePython)
  n = 1
  ref = Ba_element
FEATURE [App::DocumentObjectGroupPython] F_element079  label="F_element : 037"  # scripted group (container) (typed FeaturePython)
  n = 2
  ref = F_element
FEATURE [App::DocumentObjectGroupPython] G4_BARIUM_FLUORIDE  # scripted group (container) (typed FeaturePython)
  Dunit = g/cm3
  Dvalue = 4.89
  Group = -> [Ba_element013,F_element079]
  conduct = 2
  density = 1
  expand = 3
  formula = G4_BARIUM_FLUORIDE
  name = G4_BARIUM_FLUORIDE
  specific = 4
FEATURE [App::DocumentObjectGroupPython] Ba_element014  label="Ba_element : 013"  # scripted group (container) (typed FeaturePython)
  n = 1
  ref = Ba_element
FEATURE [App::DocumentObjectGroupPython] S_element094  label="S_element : 028"  # scripted group (container) (typed FeaturePython)
  n = 1
  ref = S_element
FEATURE [App::DocumentObjectGroupPython] O_element530  label="O_element : 338"  # scripted group (container) (typed FeaturePython)
  n = 4
  ref = O_element
FEATURE [App::DocumentObjectGroupPython] G4_BARIUM_SULFATE  # scripted group (container) (typed FeaturePython)
  Dunit = g/cm3
  Dvalue = 4.5
  Group = -> [Ba_element014,S_element094,O_element530]
  conduct = 2
  density = 1
  expand = 3
  formula = G4_BARIUM_SULFATE
  name = G4_BARIUM_SULFATE
  specific = 4
FEATURE [App::DocumentObjectGroupPython] C_element605  label="C_element : 396"  # scripted group (container) (typed FeaturePython)
  n = 6
  ref = C_element
FEATURE [App::DocumentObjectGroupPython] H_element565  label="H_element : 365"  # scripted group (container) (typed FeaturePython)
  n = 6
  ref = H_element
FEATURE [App::DocumentObjectGroupPython] G4_BENZENE  # scripted group (container) (typed FeaturePython)
  Dunit = g/cm3
  Dvalue = 0.87865
  Group = -> [C_element605,H_element565]
  conduct = 2
  density = 1
  expand = 3
  formula = G4_BENZENE
  name = G4_BENZENE
  specific = 4
FEATURE [App::DocumentObjectGroupPython] Be_element009  label="Be_element : 008"  # scripted group (container) (typed FeaturePython)
  n = 1
  ref = Be_element
FEATURE [App::DocumentObjectGroupPython] O_element531  label="O_element : 339"  # scripted group (container) (typed FeaturePython)
  n = 1
  ref = O_element
FEATURE [App::DocumentObjectGroupPython] G4_BERYLLIUM_OXIDE  # scripted group (container) (typed FeaturePython)
  Dunit = g/cm3
  Dvalue = 3.01
  Group = -> [Be_element009,O_element531]
  conduct = 2
  density = 1
  expand = 3
  formula = G4_BERYLLIUM_OXIDE
  name = G4_BERYLLIUM_OXIDE
  specific = 4
FEATURE [App::DocumentObjectGroupPython] Bi_element009  label="Bi_element : 009"  # scripted group (container) (typed FeaturePython)
  n = 4
  ref = Bi_element
FEATURE [App::DocumentObjectGroupPython] Ge_element009  label="Ge_element : 008"  # scripted group (container) (typed FeaturePython)
  n = 3
  ref = Ge_element
FEATURE [App::DocumentObjectGroupPython] O_element532  label="O_element : 340"  # scripted group (container) (typed FeaturePython)
  n = 12
  ref = O_element
FEATURE [App::DocumentObjectGroupPython] G4_BGO  # scripted group (container) (typed FeaturePython)
  Dunit = g/cm3
  Dvalue = 7.13
  Group = -> [Bi_element009,Ge_element009,O_element532]
  conduct = 2
  density = 1
  expand = 3
  formula = G4_BGO
  name = G4_BGO
  specific = 4
FEATURE [App::DocumentObjectGroupPython] H_element566  label="H_element : 0.251"  # scripted group (container) (typed FeaturePython)
  n = 0.102
FEATURE [App::DocumentObjectGroupPython] C_element606  label="C_element : 0.980"  # scripted group (container) (typed FeaturePython)
  n = 0.11
FEATURE [App::DocumentObjectGroupPython] N_element281  label="N_element : 0.832"  # scripted group (container) (typed FeaturePython)
  n = 0.033
FEATURE [App::DocumentObjectGroupPython] O_element533  label="O_element : 0.972"  # scripted group (container) (typed FeaturePython)
  n = 0.745
FEATURE [App::DocumentObjectGroupPython] Na_element082  label="Na_element : 0.143"  # scripted group (container) (typed FeaturePython)
  n = 0.001
FEATURE [App::DocumentObjectGroupPython] P_element077  label="P_element : 0.138"  # scripted group (container) (typed FeaturePython)
  n = 0.001
FEATURE [App::DocumentObjectGroupPython] S_element095  label="S_element : 0.066"  # scripted group (container) (typed FeaturePython)
  n = 0.002
FEATURE [App::DocumentObjectGroupPython] Cl_element122  label="Cl_element : 0.628"  # scripted group (container) (typed FeaturePython)
  n = 0.003
FEATURE [App::DocumentObjectGroupPython] K_element053  label="K_element : 0.044"  # scripted group (container) (typed FeaturePython)
  n = 0.002
FEATURE [App::DocumentObjectGroupPython] Fe_element033  label="Fe_element : 0.021"  # scripted group (container) (typed FeaturePython)
  n = 0.001
FEATURE [App::DocumentObjectGroupPython] G4_BLOOD_ICRP  # scripted group (container) (typed FeaturePython)
  Dunit = g/cm3
  Dvalue = 1.06
  Group = -> [H_element566,C_element606,N_element281,O_element533,Na_element082,P_element077,S_element095,Cl_element122,K_element053,Fe_element033]
  conduct = 2
  density = 1
  expand = 3
  formula = G4_BLOOD_ICRP
  name = G4_BLOOD_ICRP
  specific = 4
FEATURE [App::DocumentObjectGroupPython] H_element567  label="H_element : 0.252"  # scripted group (container) (typed FeaturePython)
  n = 0.064
FEATURE [App::DocumentObjectGroupPython] C_element607  label="C_element : 0.981"  # scripted group (container) (typed FeaturePython)
  n = 0.278
FEATURE [App::DocumentObjectGroupPython] N_element282  label="N_element : 0.833"  # scripted group (container) (typed FeaturePython)
  n = 0.027
FEATURE [App::DocumentObjectGroupPython] O_element534  label="O_element : 0.973"  # scripted group (container) (typed FeaturePython)
  n = 0.41
FEATURE [App::DocumentObjectGroupPython] Mg_element045  label="Mg_element : 0.150"  # scripted group (container) (typed FeaturePython)
  n = 0.002
FEATURE [App::DocumentObjectGroupPython] P_element078  label="P_element : 0.139"  # scripted group (container) (typed FeaturePython)
  n = 0.07
FEATURE [App::DocumentObjectGroupPython] S_element096  label="S_element : 0.067"  # scripted group (container) (typed FeaturePython)
  n = 0.002
FEATURE [App::DocumentObjectGroupPython] Ca_element059  label="Ca_element : 0.242"  # scripted group (container) (typed FeaturePython)
  n = 0.147
FEATURE [App::DocumentObjectGroupPython] G4_BONE_COMPACT_ICRU  # scripted group (container) (typed FeaturePython)
  Dunit = g/cm3
  Dvalue = 1.85
  Group = -> [H_element567,C_element607,N_element282,O_element534,Mg_element045,P_element078,S_element096,Ca_element059]
  conduct = 2
  density = 1
  expand = 3
  formula = G4_BONE_COMPACT_ICRU
  name = G4_BONE_COMPACT_ICRU
  specific = 4
FEATURE [App::DocumentObjectGroupPython] H_element568  label="H_element : 0.253"  # scripted group (container) (typed FeaturePython)
  n = 0.034
FEATURE [App::DocumentObjectGroupPython] C_element608  label="C_element : 0.982"  # scripted group (container) (typed FeaturePython)
  n = 0.155
FEATURE [App::DocumentObjectGroupPython] N_element283  label="N_element : 0.834"  # scripted group (container) (typed FeaturePython)
  n = 0.042
FEATURE [App::DocumentObjectGroupPython] O_element535  label="O_element : 0.974"  # scripted group (container) (typed FeaturePython)
  n = 0.435
FEATURE [App::DocumentObjectGroupPython] Na_element083  label="Na_element : 0.144"  # scripted group (container) (typed FeaturePython)
  n = 0.001
FEATURE [App::DocumentObjectGroupPython] Mg_element046  label="Mg_element : 0.151"  # scripted group (container) (typed FeaturePython)
  n = 0.002
FEATURE [App::DocumentObjectGroupPython] P_element079  label="P_element : 0.140"  # scripted group (container) (typed FeaturePython)
  n = 0.103
FEATURE [App::DocumentObjectGroupPython] S_element097  label="S_element : 0.068"  # scripted group (container) (typed FeaturePython)
  n = 0.003
FEATURE [App::DocumentObjectGroupPython] Ca_element060  label="Ca_element : 0.243"  # scripted group (container) (typed FeaturePython)
  n = 0.225
FEATURE [App::DocumentObjectGroupPython] G4_BONE_CORTICAL_ICRP  # scripted group (container) (typed FeaturePython)
  Dunit = g/cm3
  Dvalue = 1.92
  Group = -> [H_element568,C_element608,N_element283,O_element535,Na_element083,Mg_element046,P_element079,S_element097,Ca_element060]
  conduct = 2
  density = 1
  expand = 3
  formula = G4_BONE_CORTICAL_ICRP
  name = G4_BONE_CORTICAL_ICRP
  specific = 4
FEATURE [App::DocumentObjectGroupPython] B_element029  label="B_element : 023"  # scripted group (container) (typed FeaturePython)
  n = 4
  ref = B_element
FEATURE [App::DocumentObjectGroupPython] C_element609  label="C_element : 397"  # scripted group (container) (typed FeaturePython)
  n = 1
  ref = C_element
FEATURE [App::DocumentObjectGroupPython] G4_BORON_CARBIDE  # scripted group (container) (typed FeaturePython)
  Dunit = g/cm3
  Dvalue = 2.52
  Group = -> [B_element029,C_element609]
  conduct = 2
  density = 1
  expand = 3
  formula = G4_BORON_CARBIDE
  name = G4_BORON_CARBIDE
  specific = 4
FEATURE [App::DocumentObjectGroupPython] B_element030  label="B_element : 024"  # scripted group (container) (typed FeaturePython)
  n = 2
  ref = B_element
FEATURE [App::DocumentObjectGroupPython] O_element536  label="O_element : 341"  # scripted group (container) (typed FeaturePython)
  n = 3
  ref = O_element
FEATURE [App::DocumentObjectGroupPython] G4_BORON_OXIDE  # scripted group (container) (typed FeaturePython)
  Dunit = g/cm3
  Dvalue = 1.812
  Group = -> [B_element030,O_element536]
  conduct = 2
  density = 1
  expand = 3
  formula = G4_BORON_OXIDE
  name = G4_BORON_OXIDE
  specific = 4
FEATURE [App::DocumentObjectGroupPython] H_element569  label="H_element : 0.254"  # scripted group (container) (typed FeaturePython)
  n = 0.107
FEATURE [App::DocumentObjectGroupPython] C_element610  label="C_element : 0.983"  # scripted group (container) (typed FeaturePython)
  n = 0.145
FEATURE [App::DocumentObjectGroupPython] N_element284  label="N_element : 0.835"  # scripted group (container) (typed FeaturePython)
  n = 0.022
FEATURE [App::DocumentObjectGroupPython] O_element537  label="O_element : 0.975"  # scripted group (container) (typed FeaturePython)
  n = 0.712
FEATURE [App::DocumentObjectGroupPython] Na_element084  label="Na_element : 0.145"  # scripted group (container) (typed FeaturePython)
  n = 0.002
FEATURE [App::DocumentObjectGroupPython] P_element080  label="P_element : 0.141"  # scripted group (container) (typed FeaturePython)
  n = 0.004
FEATURE [App::DocumentObjectGroupPython] S_element098  label="S_element : 0.069"  # scripted group (container) (typed FeaturePython)
  n = 0.002
FEATURE [App::DocumentObjectGroupPython] Cl_element123  label="Cl_element : 0.629"  # scripted group (container) (typed FeaturePython)
  n = 0.003
FEATURE [App::DocumentObjectGroupPython] K_element054  label="K_element : 0.045"  # scripted group (container) (typed FeaturePython)
  n = 0.003
FEATURE [App::DocumentObjectGroupPython] G4_BRAIN_ICRP  # scripted group (container) (typed FeaturePython)
  Dunit = g/cm3
  Dvalue = 1.04
  Group = -> [H_element569,C_element610,N_element284,O_element537,Na_element084,P_element080,S_element098,Cl_element123,K_element054]
  conduct = 2
  density = 1
  expand = 3
  formula = G4_BRAIN_ICRP
  name = G4_BRAIN_ICRP
  specific = 4
FEATURE [App::DocumentObjectGroupPython] C_element611  label="C_element : 398"  # scripted group (container) (typed FeaturePython)
  n = 4
  ref = C_element
FEATURE [App::DocumentObjectGroupPython] H_element570  label="H_element : 366"  # scripted group (container) (typed FeaturePython)
  n = 10
  ref = H_element
FEATURE [App::DocumentObjectGroupPython] G4_BUTANE  # scripted group (container) (typed FeaturePython)
  Dunit = g/cm3
  Dvalue = 0.00249343
  Group = -> [C_element611,H_element570]
  conduct = 2
  density = 1
  expand = 3
  formula = G4_BUTANE
  name = G4_BUTANE
  specific = 4
FEATURE [App::DocumentObjectGroupPython] C_element612  label="C_element : 399"  # scripted group (container) (typed FeaturePython)
  n = 4
  ref = C_element
FEATURE [App::DocumentObjectGroupPython] H_element571  label="H_element : 367"  # scripted group (container) (typed FeaturePython)
  n = 10
  ref = H_element
FEATURE [App::DocumentObjectGroupPython] O_element538  label="O_element : 342"  # scripted group (container) (typed FeaturePython)
  n = 1
  ref = O_element
FEATURE [App::DocumentObjectGroupPython] G4_N_BUTYL_ALCOHOL  label="G4_N-BUTYL_ALCOHOL"  # scripted group (container) (typed FeaturePython)
  Dunit = g/cm3
  Dvalue = 0.8098
  Group = -> [C_element612,H_element571,O_element538]
  conduct = 2
  density = 1
  expand = 3
  formula = G4_N-BUTYL_ALCOHOL
  name = G4_N-BUTYL_ALCOHOL
  specific = 4
FEATURE [App::DocumentObjectGroupPython] H_element572  label="H_element : 0.255"  # scripted group (container) (typed FeaturePython)
  n = 0.02468
FEATURE [App::DocumentObjectGroupPython] C_element613  label="C_element : 0.984"  # scripted group (container) (typed FeaturePython)
  n = 0.501611
FEATURE [App::DocumentObjectGroupPython] O_element539  label="O_element : 0.976"  # scripted group (container) (typed FeaturePython)
  n = 0.004527
FEATURE [App::DocumentObjectGroupPython] F_element080  label="F_element : 0.729"  # scripted group (container) (typed FeaturePython)
  n = 0.465209
FEATURE [App::DocumentObjectGroupPython] Si_element029  label="Si_element : 0.390"  # scripted group (container) (typed FeaturePython)
  n = 0.003973
FEATURE [App::DocumentObjectGroupPython] G4_C_552  label="G4_C-552"  # scripted group (container) (typed FeaturePython)
  Dunit = g/cm3
  Dvalue = 1.76
  Group = -> [H_element572,C_element613,O_element539,F_element080,Si_element029]
  conduct = 2
  density = 1
  expand = 3
  formula = G4_C-552
  name = G4_C-552
  specific = 4
FEATURE [App::DocumentObjectGroupPython] Cd_element013  label="Cd_element : 012"  # scripted group (container) (typed FeaturePython)
  n = 1
  ref = Cd_element
FEATURE [App::DocumentObjectGroupPython] Te_element009  label="Te_element : 008"  # scripted group (container) (typed FeaturePython)
  n = 1
  ref = Te_element
FEATURE [App::DocumentObjectGroupPython] G4_CADMIUM_TELLURIDE  # scripted group (container) (typed FeaturePython)
  Dunit = g/cm3
  Dvalue = 6.2
  Group = -> [Cd_element013,Te_element009]
  conduct = 2
  density = 1
  expand = 3
  formula = G4_CADMIUM_TELLURIDE
  name = G4_CADMIUM_TELLURIDE
  specific = 4
FEATURE [App::DocumentObjectGroupPython] Cd_element014  label="Cd_element : 013"  # scripted group (container) (typed FeaturePython)
  n = 1
  ref = Cd_element
FEATURE [App::DocumentObjectGroupPython] W_element021  label="W_element : 020"  # scripted group (container) (typed FeaturePython)
  n = 1
  ref = W_element
FEATURE [App::DocumentObjectGroupPython] O_element540  label="O_element : 343"  # scripted group (container) (typed FeaturePython)
  n = 4
  ref = O_element
FEATURE [App::DocumentObjectGroupPython] G4_CADMIUM_TUNGSTATE  # scripted group (container) (typed FeaturePython)
  Dunit = g/cm3
  Dvalue = 7.9
  Group = -> [Cd_element014,W_element021,O_element540]
  conduct = 2
  density = 1
  expand = 3
  formula = G4_CADMIUM_TUNGSTATE
  name = G4_CADMIUM_TUNGSTATE
  specific = 4
FEATURE [App::DocumentObjectGroupPython] Ca_element061  label="Ca_element : 028"  # scripted group (container) (typed FeaturePython)
  n = 1
  ref = Ca_element
FEATURE [App::DocumentObjectGroupPython] C_element614  label="C_element : 400"  # scripted group (container) (typed FeaturePython)
  n = 1
  ref = C_element
FEATURE [App::DocumentObjectGroupPython] O_element541  label="O_element : 344"  # scripted group (container) (typed FeaturePython)
  n = 3
  ref = O_element
FEATURE [App::DocumentObjectGroupPython] G4_CALCIUM_CARBONATE  # scripted group (container) (typed FeaturePython)
  Dunit = g/cm3
  Dvalue = 2.8
  Group = -> [Ca_element061,C_element614,O_element541]
  conduct = 2
  density = 1
  expand = 3
  formula = G4_CALCIUM_CARBONATE
  name = G4_CALCIUM_CARBONATE
  specific = 4
FEATURE [App::DocumentObjectGroupPython] Ca_element062  label="Ca_element : 029"  # scripted group (container) (typed FeaturePython)
  n = 1
  ref = Ca_element
FEATURE [App::DocumentObjectGroupPython] F_element081  label="F_element : 038"  # scripted group (container) (typed FeaturePython)
  n = 2
  ref = F_element
FEATURE [App::DocumentObjectGroupPython] G4_CALCIUM_FLUORIDE  # scripted group (container) (typed FeaturePython)
  Dunit = g/cm3
  Dvalue = 3.18
  Group = -> [Ca_element062,F_element081]
  conduct = 2
  density = 1
  expand = 3
  formula = G4_CALCIUM_FLUORIDE
  name = G4_CALCIUM_FLUORIDE
  specific = 4
FEATURE [App::DocumentObjectGroupPython] Ca_element063  label="Ca_element : 030"  # scripted group (container) (typed FeaturePython)
  n = 1
  ref = Ca_element
FEATURE [App::DocumentObjectGroupPython] O_element542  label="O_element : 345"  # scripted group (container) (typed FeaturePython)
  n = 1
  ref = O_element
FEATURE [App::DocumentObjectGroupPython] G4_CALCIUM_OXIDE  # scripted group (container) (typed FeaturePython)
  Dunit = g/cm3
  Dvalue = 3.3
  Group = -> [Ca_element063,O_element542]
  conduct = 2
  density = 1
  expand = 3
  formula = G4_CALCIUM_OXIDE
  name = G4_CALCIUM_OXIDE
  specific = 4
FEATURE [App::DocumentObjectGroupPython] Ca_element064  label="Ca_element : 031"  # scripted group (container) (typed FeaturePython)
  n = 1
  ref = Ca_element
FEATURE [App::DocumentObjectGroupPython] S_element099  label="S_element : 029"  # scripted group (container) (typed FeaturePython)
  n = 1
  ref = S_element
FEATURE [App::DocumentObjectGroupPython] O_element543  label="O_element : 346"  # scripted group (container) (typed FeaturePython)
  n = 4
  ref = O_element
FEATURE [App::DocumentObjectGroupPython] G4_CALCIUM_SULFATE  # scripted group (container) (typed FeaturePython)
  Dunit = g/cm3
  Dvalue = 2.96
  Group = -> [Ca_element064,S_element099,O_element543]
  conduct = 2
  density = 1
  expand = 3
  formula = G4_CALCIUM_SULFATE
  name = G4_CALCIUM_SULFATE
  specific = 4
FEATURE [App::DocumentObjectGroupPython] Ca_element065  label="Ca_element : 032"  # scripted group (container) (typed FeaturePython)
  n = 1
  ref = Ca_element
FEATURE [App::DocumentObjectGroupPython] W_element022  label="W_element : 021"  # scripted group (container) (typed FeaturePython)
  n = 1
  ref = W_element
FEATURE [App::DocumentObjectGroupPython] O_element544  label="O_element : 347"  # scripted group (container) (typed FeaturePython)
  n = 4
  ref = O_element
FEATURE [App::DocumentObjectGroupPython] G4_CALCIUM_TUNGSTATE  # scripted group (container) (typed FeaturePython)
  Dunit = g/cm3
  Dvalue = 6.062
  Group = -> [Ca_element065,W_element022,O_element544]
  conduct = 2
  density = 1
  expand = 3
  formula = G4_CALCIUM_TUNGSTATE
  name = G4_CALCIUM_TUNGSTATE
  specific = 4
FEATURE [App::DocumentObjectGroupPython] C_element615  label="C_element : 401"  # scripted group (container) (typed FeaturePython)
  n = 1
  ref = C_element
FEATURE [App::DocumentObjectGroupPython] O_element545  label="O_element : 348"  # scripted group (container) (typed FeaturePython)
  n = 2
  ref = O_element
FEATURE [App::DocumentObjectGroupPython] G4_CARBON_DIOXIDE  # scripted group (container) (typed FeaturePython)
  Dunit = g/cm3
  Dvalue = 0.00184212
  Group = -> [C_element615,O_element545]
  conduct = 2
  density = 1
  expand = 3
  formula = G4_CARBON_DIOXIDE
  name = G4_CARBON_DIOXIDE
  specific = 4
FEATURE [App::DocumentObjectGroupPython] C_element616  label="C_element : 402"  # scripted group (container) (typed FeaturePython)
  n = 1
  ref = C_element
FEATURE [App::DocumentObjectGroupPython] Cl_element124  label="Cl_element : 061"  # scripted group (container) (typed FeaturePython)
  n = 4
  ref = Cl_element
FEATURE [App::DocumentObjectGroupPython] G4_CARBON_TETRACHLORIDE  # scripted group (container) (typed FeaturePython)
  Dunit = g/cm3
  Dvalue = 1.594
  Group = -> [C_element616,Cl_element124]
  conduct = 2
  density = 1
  expand = 3
  formula = G4_CARBON_TETRACHLORIDE
  name = G4_CARBON_TETRACHLORIDE
  specific = 4
FEATURE [App::DocumentObjectGroupPython] C_element617  label="C_element : 403"  # scripted group (container) (typed FeaturePython)
  n = 6
  ref = C_element
FEATURE [App::DocumentObjectGroupPython] H_element573  label="H_element : 368"  # scripted group (container) (typed FeaturePython)
  n = 10
  ref = H_element
FEATURE [App::DocumentObjectGroupPython] O_element546  label="O_element : 349"  # scripted group (container) (typed FeaturePython)
  n = 5
  ref = O_element
FEATURE [App::DocumentObjectGroupPython] G4_CELLULOSE_CELLOPHANE  # scripted group (container) (typed FeaturePython)
  Dunit = g/cm3
  Dvalue = 1.42
  Group = -> [C_element617,H_element573,O_element546]
  conduct = 2
  density = 1
  expand = 3
  formula = G4_CELLULOSE_CELLOPHANE
  name = G4_CELLULOSE_CELLOPHANE
  specific = 4
FEATURE [App::DocumentObjectGroupPython] H_element574  label="H_element : 0.256"  # scripted group (container) (typed FeaturePython)
  n = 0.067125
FEATURE [App::DocumentObjectGroupPython] C_element618  label="C_element : 0.985"  # scripted group (container) (typed FeaturePython)
  n = 0.545403
FEATURE [App::DocumentObjectGroupPython] O_element547  label="O_element : 0.977"  # scripted group (container) (typed FeaturePython)
  n = 0.387472
FEATURE [App::DocumentObjectGroupPython] G4_CELLULOSE_BUTYRATE  # scripted group (container) (typed FeaturePython)
  Dunit = g/cm3
  Dvalue = 1.2
  Group = -> [H_element574,C_element618,O_element547]
  conduct = 2
  density = 1
  expand = 3
  formula = G4_CELLULOSE_BUTYRATE
  name = G4_CELLULOSE_BUTYRATE
  specific = 4
FEATURE [App::DocumentObjectGroupPython] H_element575  label="H_element : 0.257"  # scripted group (container) (typed FeaturePython)
  n = 0.029216
FEATURE [App::DocumentObjectGroupPython] C_element619  label="C_element : 0.986"  # scripted group (container) (typed FeaturePython)
  n = 0.271296
FEATURE [App::DocumentObjectGroupPython] N_element285  label="N_element : 0.836"  # scripted group (container) (typed FeaturePython)
  n = 0.121276
FEATURE [App::DocumentObjectGroupPython] O_element548  label="O_element : 0.978"  # scripted group (container) (typed FeaturePython)
  n = 0.578212
FEATURE [App::DocumentObjectGroupPython] G4_CELLULOSE_NITRATE  # scripted group (container) (typed FeaturePython)
  Dunit = g/cm3
  Dvalue = 1.49
  Group = -> [H_element575,C_element619,N_element285,O_element548]
  conduct = 2
  density = 1
  expand = 3
  formula = G4_CELLULOSE_NITRATE
  name = G4_CELLULOSE_NITRATE
  specific = 4
FEATURE [App::DocumentObjectGroupPython] H_element576  label="H_element : 0.258"  # scripted group (container) (typed FeaturePython)
  n = 0.107596
FEATURE [App::DocumentObjectGroupPython] N_element286  label="N_element : 0.837"  # scripted group (container) (typed FeaturePython)
  n = 0.0008
FEATURE [App::DocumentObjectGroupPython] O_element549  label="O_element : 0.979"  # scripted group (container) (typed FeaturePython)
  n = 0.874976
FEATURE [App::DocumentObjectGroupPython] S_element100  label="S_element : 0.070"  # scripted group (container) (typed FeaturePython)
  n = 0.014627
FEATURE [App::DocumentObjectGroupPython] Ce_element009  label="Ce_element : 0.005"  # scripted group (container) (typed FeaturePython)
  n = 0.002001
FEATURE [App::DocumentObjectGroupPython] G4_CERIC_SULFATE  # scripted group (container) (typed FeaturePython)
  Dunit = g/cm3
  Dvalue = 1.03
  Group = -> [H_element576,N_element286,O_element549,S_element100,Ce_element009]
  conduct = 2
  density = 1
  expand = 3
  formula = G4_CERIC_SULFATE
  name = G4_CERIC_SULFATE
  specific = 4
FEATURE [App::DocumentObjectGroupPython] Cs_element013  label="Cs_element : 012"  # scripted group (container) (typed FeaturePython)
  n = 1
  ref = Cs_element
FEATURE [App::DocumentObjectGroupPython] F_element082  label="F_element : 039"  # scripted group (container) (typed FeaturePython)
  n = 1
  ref = F_element
FEATURE [App::DocumentObjectGroupPython] G4_CESIUM_FLUORIDE  # scripted group (container) (typed FeaturePython)
  Dunit = g/cm3
  Dvalue = 4.115
  Group = -> [Cs_element013,F_element082]
  conduct = 2
  density = 1
  expand = 3
  formula = G4_CESIUM_FLUORIDE
  name = G4_CESIUM_FLUORIDE
  specific = 4
FEATURE [App::DocumentObjectGroupPython] Cs_element014  label="Cs_element : 013"  # scripted group (container) (typed FeaturePython)
  n = 1
  ref = Cs_element
FEATURE [App::DocumentObjectGroupPython] I_element041  label="I_element : 026"  # scripted group (container) (typed FeaturePython)
  n = 1
  ref = I_element
FEATURE [App::DocumentObjectGroupPython] G4_CESIUM_IODIDE  # scripted group (container) (typed FeaturePython)
  Dunit = g/cm3
  Dvalue = 4.51
  Group = -> [Cs_element014,I_element041]
  conduct = 2
  density = 1
  expand = 3
  formula = G4_CESIUM_IODIDE
  name = G4_CESIUM_IODIDE
  specific = 4
FEATURE [App::DocumentObjectGroupPython] C_element620  label="C_element : 404"  # scripted group (container) (typed FeaturePython)
  n = 6
  ref = C_element
FEATURE [App::DocumentObjectGroupPython] H_element577  label="H_element : 369"  # scripted group (container) (typed FeaturePython)
  n = 5
  ref = H_element
FEATURE [App::DocumentObjectGroupPython] Cl_element125  label="Cl_element : 062"  # scripted group (container) (typed FeaturePython)
  n = 1
  ref = Cl_element
FEATURE [App::DocumentObjectGroupPython] G4_CHLOROBENZENE  # scripted group (container) (typed FeaturePython)
  Dunit = g/cm3
  Dvalue = 1.1058
  Group = -> [C_element620,H_element577,Cl_element125]
  conduct = 2
  density = 1
  expand = 3
  formula = G4_CHLOROBENZENE
  name = G4_CHLOROBENZENE
  specific = 4
FEATURE [App::DocumentObjectGroupPython] C_element621  label="C_element : 405"  # scripted group (container) (typed FeaturePython)
  n = 1
  ref = C_element
FEATURE [App::DocumentObjectGroupPython] H_element578  label="H_element : 370"  # scripted group (container) (typed FeaturePython)
  n = 1
  ref = H_element
FEATURE [App::DocumentObjectGroupPython] Cl_element126  label="Cl_element : 063"  # scripted group (container) (typed FeaturePython)
  n = 3
  ref = Cl_element
FEATURE [App::DocumentObjectGroupPython] G4_CHLOROFORM  # scripted group (container) (typed FeaturePython)
  Dunit = g/cm3
  Dvalue = 1.4832
  Group = -> [C_element621,H_element578,Cl_element126]
  conduct = 2
  density = 1
  expand = 3
  formula = G4_CHLOROFORM
  name = G4_CHLOROFORM
  specific = 4
FEATURE [App::DocumentObjectGroupPython] H_element579  label="H_element : 0.259"  # scripted group (container) (typed FeaturePython)
  n = 0.01
FEATURE [App::DocumentObjectGroupPython] C_element622  label="C_element : 0.987"  # scripted group (container) (typed FeaturePython)
  n = 0.001
FEATURE [App::DocumentObjectGroupPython] O_element550  label="O_element : 0.980"  # scripted group (container) (typed FeaturePython)
  n = 0.529107
FEATURE [App::DocumentObjectGroupPython] Na_element085  label="Na_element : 0.146"  # scripted group (container) (typed FeaturePython)
  n = 0.016
FEATURE [App::DocumentObjectGroupPython] Mg_element047  label="Mg_element : 0.152"  # scripted group (container) (typed FeaturePython)
  n = 0.002
FEATURE [App::DocumentObjectGroupPython] Al_element018  label="Al_element : 0.039"  # scripted group (container) (typed FeaturePython)
  n = 0.033872
FEATURE [App::DocumentObjectGroupPython] Si_element030  label="Si_element : 0.391"  # scripted group (container) (typed FeaturePython)
  n = 0.337021
FEATURE [App::DocumentObjectGroupPython] K_element055  label="K_element : 0.046"  # scripted group (container) (typed FeaturePython)
  n = 0.013
FEATURE [App::DocumentObjectGroupPython] Ca_element066  label="Ca_element : 0.244"  # scripted group (container) (typed FeaturePython)
  n = 0.044
FEATURE [App::DocumentObjectGroupPython] Fe_element034  label="Fe_element : 0.022"  # scripted group (container) (typed FeaturePython)
  n = 0.014
FEATURE [App::DocumentObjectGroupPython] G4_CONCRETE  # scripted group (container) (typed FeaturePython)
  Dunit = g/cm3
  Dvalue = 2.3
  Group = -> [H_element579,C_element622,O_element550,Na_element085,Mg_element047,Al_element018,Si_element030,K_element055,Ca_element066,Fe_element034]
  conduct = 2
  density = 1
  expand = 3
  formula = G4_CONCRETE
  name = G4_CONCRETE
  specific = 4
FEATURE [App::DocumentObjectGroupPython] C_element623  label="C_element : 406"  # scripted group (container) (typed FeaturePython)
  n = 6
  ref = C_element
FEATURE [App::DocumentObjectGroupPython] H_element580  label="H_element : 371"  # scripted group (container) (typed FeaturePython)
  n = 12
  ref = H_element
FEATURE [App::DocumentObjectGroupPython] G4_CYCLOHEXANE  # scripted group (container) (typed FeaturePython)
  Dunit = g/cm3
  Dvalue = 0.779
  Group = -> [C_element623,H_element580]
  conduct = 2
  density = 1
  expand = 3
  formula = G4_CYCLOHEXANE
  name = G4_CYCLOHEXANE
  specific = 4
FEATURE [App::DocumentObjectGroupPython] C_element624  label="C_element : 407"  # scripted group (container) (typed FeaturePython)
  n = 6
  ref = C_element
FEATURE [App::DocumentObjectGroupPython] H_element581  label="H_element : 372"  # scripted group (container) (typed FeaturePython)
  n = 4
  ref = H_element
FEATURE [App::DocumentObjectGroupPython] Cl_element127  label="Cl_element : 064"  # scripted group (container) (typed FeaturePython)
  n = 2
  ref = Cl_element
FEATURE [App::DocumentObjectGroupPython] G4_1_2_DICHLOROBENZENE  label="G4_1.2-DICHLOROBENZENE"  # scripted group (container) (typed FeaturePython)
  Dunit = g/cm3
  Dvalue = 1.3048
  Group = -> [C_element624,H_element581,Cl_element127]
  conduct = 2
  density = 1
  expand = 3
  formula = G4_1.2-DICHLOROBENZENE
  name = G4_1.2-DICHLOROBENZENE
  specific = 4
FEATURE [App::DocumentObjectGroupPython] C_element625  label="C_element : 408"  # scripted group (container) (typed FeaturePython)
  n = 4
  ref = C_element
FEATURE [App::DocumentObjectGroupPython] H_element582  label="H_element : 373"  # scripted group (container) (typed FeaturePython)
  n = 8
  ref = H_element
FEATURE [App::DocumentObjectGroupPython] O_element551  label="O_element : 350"  # scripted group (container) (typed FeaturePython)
  n = 1
  ref = O_element
FEATURE [App::DocumentObjectGroupPython] Cl_element128  label="Cl_element : 065"  # scripted group (container) (typed FeaturePython)
  n = 2
  ref = Cl_element
FEATURE [App::DocumentObjectGroupPython] G4_DICHLORODIETHYL_ETHER  # scripted group (container) (typed FeaturePython)
  Dunit = g/cm3
  Dvalue = 1.2199
  Group = -> [C_element625,H_element582,O_element551,Cl_element128]
  conduct = 2
  density = 1
  expand = 3
  formula = G4_DICHLORODIETHYL_ETHER
  name = G4_DICHLORODIETHYL_ETHER
  specific = 4
FEATURE [App::DocumentObjectGroupPython] C_element626  label="C_element : 409"  # scripted group (container) (typed FeaturePython)
  n = 2
  ref = C_element
FEATURE [App::DocumentObjectGroupPython] H_element583  label="H_element : 374"  # scripted group (container) (typed FeaturePython)
  n = 4
  ref = H_element
FEATURE [App::DocumentObjectGroupPython] Cl_element129  label="Cl_element : 066"  # scripted group (container) (typed FeaturePython)
  n = 2
  ref = Cl_element
FEATURE [App::DocumentObjectGroupPython] G4_1_2_DICHLOROETHANE  label="G4_1.2-DICHLOROETHANE"  # scripted group (container) (typed FeaturePython)
  Dunit = g/cm3
  Dvalue = 1.2351
  Group = -> [C_element626,H_element583,Cl_element129]
  conduct = 2
  density = 1
  expand = 3
  formula = G4_1.2-DICHLOROETHANE
  name = G4_1.2-DICHLOROETHANE
  specific = 4
FEATURE [App::DocumentObjectGroupPython] C_element627  label="C_element : 410"  # scripted group (container) (typed FeaturePython)
  n = 4
  ref = C_element
FEATURE [App::DocumentObjectGroupPython] H_element584  label="H_element : 375"  # scripted group (container) (typed FeaturePython)
  n = 10
  ref = H_element
FEATURE [App::DocumentObjectGroupPython] O_element552  label="O_element : 351"  # scripted group (container) (typed FeaturePython)
  n = 1
  ref = O_element
FEATURE [App::DocumentObjectGroupPython] G4_DIETHYL_ETHER  # scripted group (container) (typed FeaturePython)
  Dunit = g/cm3
  Dvalue = 0.71378
  Group = -> [C_element627,H_element584,O_element552]
  conduct = 2
  density = 1
  expand = 3
  formula = G4_DIETHYL_ETHER
  name = G4_DIETHYL_ETHER
  specific = 4
FEATURE [App::DocumentObjectGroupPython] C_element628  label="C_element : 411"  # scripted group (container) (typed FeaturePython)
  n = 3
  ref = C_element
FEATURE [App::DocumentObjectGroupPython] H_element585  label="H_element : 376"  # scripted group (container) (typed FeaturePython)
  n = 7
  ref = H_element
FEATURE [App::DocumentObjectGroupPython] N_element287  label="N_element : 158"  # scripted group (container) (typed FeaturePython)
  n = 1
  ref = N_element
FEATURE [App::DocumentObjectGroupPython] O_element553  label="O_element : 352"  # scripted group (container) (typed FeaturePython)
  n = 1
  ref = O_element
FEATURE [App::DocumentObjectGroupPython] G4_N_N_DIMETHYL_FORMAMIDE  label="G4_N.N-DIMETHYL_FORMAMIDE"  # scripted group (container) (typed FeaturePython)
  Dunit = g/cm3
  Dvalue = 0.9487
  Group = -> [C_element628,H_element585,N_element287,O_element553]
  conduct = 2
  density = 1
  expand = 3
  formula = G4_N.N-DIMETHYL_FORMAMIDE
  name = G4_N.N-DIMETHYL_FORMAMIDE
  specific = 4
FEATURE [App::DocumentObjectGroupPython] C_element629  label="C_element : 412"  # scripted group (container) (typed FeaturePython)
  n = 2
  ref = C_element
FEATURE [App::DocumentObjectGroupPython] H_element586  label="H_element : 377"  # scripted group (container) (typed FeaturePython)
  n = 6
  ref = H_element
FEATURE [App::DocumentObjectGroupPython] O_element554  label="O_element : 353"  # scripted group (container) (typed FeaturePython)
  n = 1
  ref = O_element
FEATURE [App::DocumentObjectGroupPython] S_element101  label="S_element : 030"  # scripted group (container) (typed FeaturePython)
  n = 1
  ref = S_element
FEATURE [App::DocumentObjectGroupPython] G4_DIMETHYL_SULFOXIDE  # scripted group (container) (typed FeaturePython)
  Dunit = g/cm3
  Dvalue = 1.1014
  Group = -> [C_element629,H_element586,O_element554,S_element101]
  conduct = 2
  density = 1
  expand = 3
  formula = G4_DIMETHYL_SULFOXIDE
  name = G4_DIMETHYL_SULFOXIDE
  specific = 4
FEATURE [App::DocumentObjectGroupPython] C_element630  label="C_element : 413"  # scripted group (container) (typed FeaturePython)
  n = 2
  ref = C_element
FEATURE [App::DocumentObjectGroupPython] H_element587  label="H_element : 378"  # scripted group (container) (typed FeaturePython)
  n = 6
  ref = H_element
FEATURE [App::DocumentObjectGroupPython] G4_ETHANE  # scripted group (container) (typed FeaturePython)
  Dunit = g/cm3
  Dvalue = 0.00125324
  Group = -> [C_element630,H_element587]
  conduct = 2
  density = 1
  expand = 3
  formula = G4_ETHANE
  name = G4_ETHANE
  specific = 4
FEATURE [App::DocumentObjectGroupPython] C_element631  label="C_element : 414"  # scripted group (container) (typed FeaturePython)
  n = 2
  ref = C_element
FEATURE [App::DocumentObjectGroupPython] H_element588  label="H_element : 379"  # scripted group (container) (typed FeaturePython)
  n = 6
  ref = H_element
FEATURE [App::DocumentObjectGroupPython] O_element555  label="O_element : 354"  # scripted group (container) (typed FeaturePython)
  n = 1
  ref = O_element
FEATURE [App::DocumentObjectGroupPython] G4_ETHYL_ALCOHOL  # scripted group (container) (typed FeaturePython)
  Dunit = g/cm3
  Dvalue = 0.7893
  Group = -> [C_element631,H_element588,O_element555]
  conduct = 2
  density = 1
  expand = 3
  formula = G4_ETHYL_ALCOHOL
  name = G4_ETHYL_ALCOHOL
  specific = 4
FEATURE [App::DocumentObjectGroupPython] H_element589  label="H_element : 0.260"  # scripted group (container) (typed FeaturePython)
  n = 0.090027
FEATURE [App::DocumentObjectGroupPython] C_element632  label="C_element : 0.988"  # scripted group (container) (typed FeaturePython)
  n = 0.585182
FEATURE [App::DocumentObjectGroupPython] O_element556  label="O_element : 0.981"  # scripted group (container) (typed FeaturePython)
  n = 0.324791
FEATURE [App::DocumentObjectGroupPython] G4_ETHYL_CELLULOSE  # scripted group (container) (typed FeaturePython)
  Dunit = g/cm3
  Dvalue = 1.13
  Group = -> [H_element589,C_element632,O_element556]
  conduct = 2
  density = 1
  expand = 3
  formula = G4_ETHYL_CELLULOSE
  name = G4_ETHYL_CELLULOSE
  specific = 4
FEATURE [App::DocumentObjectGroupPython] C_element633  label="C_element : 415"  # scripted group (container) (typed FeaturePython)
  n = 2
  ref = C_element
FEATURE [App::DocumentObjectGroupPython] H_element590  label="H_element : 380"  # scripted group (container) (typed FeaturePython)
  n = 4
  ref = H_element
FEATURE [App::DocumentObjectGroupPython] G4_ETHYLENE  # scripted group (container) (typed FeaturePython)
  Dunit = g/cm3
  Dvalue = 0.00117497
  Group = -> [C_element633,H_element590]
  conduct = 2
  density = 1
  expand = 3
  formula = G4_ETHYLENE
  name = G4_ETHYLENE
  specific = 4
FEATURE [App::DocumentObjectGroupPython] H_element591  label="H_element : 0.261"  # scripted group (container) (typed FeaturePython)
  n = 0.096
FEATURE [App::DocumentObjectGroupPython] C_element634  label="C_element : 0.989"  # scripted group (container) (typed FeaturePython)
  n = 0.195
FEATURE [App::DocumentObjectGroupPython] N_element288  label="N_element : 0.838"  # scripted group (container) (typed FeaturePython)
  n = 0.057
FEATURE [App::DocumentObjectGroupPython] O_element557  label="O_element : 0.982"  # scripted group (container) (typed FeaturePython)
  n = 0.646
FEATURE [App::DocumentObjectGroupPython] Na_element086  label="Na_element : 0.147"  # scripted group (container) (typed FeaturePython)
  n = 0.001
FEATURE [App::DocumentObjectGroupPython] P_element081  label="P_element : 0.142"  # scripted group (container) (typed FeaturePython)
  n = 0.001
FEATURE [App::DocumentObjectGroupPython] S_element102  label="S_element : 0.071"  # scripted group (container) (typed FeaturePython)
  n = 0.003
FEATURE [App::DocumentObjectGroupPython] Cl_element130  label="Cl_element : 0.630"  # scripted group (container) (typed FeaturePython)
  n = 0.001
FEATURE [App::DocumentObjectGroupPython] G4_EYE_LENS_ICRP  # scripted group (container) (typed FeaturePython)
  Dunit = g/cm3
  Dvalue = 1.07
  Group = -> [H_element591,C_element634,N_element288,O_element557,Na_element086,P_element081,S_element102,Cl_element130]
  conduct = 2
  density = 1
  expand = 3
  formula = G4_EYE_LENS_ICRP
  name = G4_EYE_LENS_ICRP
  specific = 4
FEATURE [App::DocumentObjectGroupPython] Fe_element035  label="Fe_element : 017"  # scripted group (container) (typed FeaturePython)
  n = 2
  ref = Fe_element
FEATURE [App::DocumentObjectGroupPython] O_element558  label="O_element : 355"  # scripted group (container) (typed FeaturePython)
  n = 3
  ref = O_element
FEATURE [App::DocumentObjectGroupPython] G4_FERRIC_OXIDE  # scripted group (container) (typed FeaturePython)
  Dunit = g/cm3
  Dvalue = 5.2
  Group = -> [Fe_element035,O_element558]
  conduct = 2
  density = 1
  expand = 3
  formula = G4_FERRIC_OXIDE
  name = G4_FERRIC_OXIDE
  specific = 4
FEATURE [App::DocumentObjectGroupPython] Fe_element036  label="Fe_element : 018"  # scripted group (container) (typed FeaturePython)
  n = 1
  ref = Fe_element
FEATURE [App::DocumentObjectGroupPython] B_element031  label="B_element : 025"  # scripted group (container) (typed FeaturePython)
  n = 1
  ref = B_element
FEATURE [App::DocumentObjectGroupPython] G4_FERROBORIDE  # scripted group (container) (typed FeaturePython)
  Dunit = g/cm3
  Dvalue = 7.15
  Group = -> [Fe_element036,B_element031]
  conduct = 2
  density = 1
  expand = 3
  formula = G4_FERROBORIDE
  name = G4_FERROBORIDE
  specific = 4
FEATURE [App::DocumentObjectGroupPython] Fe_element037  label="Fe_element : 019"  # scripted group (container) (typed FeaturePython)
  n = 1
  ref = Fe_element
FEATURE [App::DocumentObjectGroupPython] O_element559  label="O_element : 356"  # scripted group (container) (typed FeaturePython)
  n = 1
  ref = O_element
FEATURE [App::DocumentObjectGroupPython] G4_FERROUS_OXIDE  # scripted group (container) (typed FeaturePython)
  Dunit = g/cm3
  Dvalue = 5.7
  Group = -> [Fe_element037,O_element559]
  conduct = 2
  density = 1
  expand = 3
  formula = G4_FERROUS_OXIDE
  name = G4_FERROUS_OXIDE
  specific = 4
FEATURE [App::DocumentObjectGroupPython] H_element592  label="H_element : 0.262"  # scripted group (container) (typed FeaturePython)
  n = 0.108259
FEATURE [App::DocumentObjectGroupPython] N_element289  label="N_element : 0.839"  # scripted group (container) (typed FeaturePython)
  n = 2.7e-05
FEATURE [App::DocumentObjectGroupPython] O_element560  label="O_element : 0.983"  # scripted group (container) (typed FeaturePython)
  n = 0.878636
FEATURE [App::DocumentObjectGroupPython] Na_element087  label="Na_element : 0.148"  # scripted group (container) (typed FeaturePython)
  n = 2.2e-05
FEATURE [App::DocumentObjectGroupPython] S_element103  label="S_element : 0.072"  # scripted group (container) (typed FeaturePython)
  n = 0.012968
FEATURE [App::DocumentObjectGroupPython] Cl_element131  label="Cl_element : 0.631"  # scripted group (container) (typed FeaturePython)
  n = 3.4e-05
FEATURE [App::DocumentObjectGroupPython] Fe_element038  label="Fe_element : 0.023"  # scripted group (container) (typed FeaturePython)
  n = 5.4e-05
FEATURE [App::DocumentObjectGroupPython] G4_FERROUS_SULFATE  # scripted group (container) (typed FeaturePython)
  Dunit = g/cm3
  Dvalue = 1.024
  Group = -> [H_element592,N_element289,O_element560,Na_element087,S_element103,Cl_element131,Fe_element038]
  conduct = 2
  density = 1
  expand = 3
  formula = G4_FERROUS_SULFATE
  name = G4_FERROUS_SULFATE
  specific = 4
FEATURE [App::DocumentObjectGroupPython] C_element635  label="C_element : 0.990"  # scripted group (container) (typed FeaturePython)
  n = 0.099335
FEATURE [App::DocumentObjectGroupPython] F_element083  label="F_element : 0.730"  # scripted group (container) (typed FeaturePython)
  n = 0.314247
FEATURE [App::DocumentObjectGroupPython] Cl_element132  label="Cl_element : 0.632"  # scripted group (container) (typed FeaturePython)
  n = 0.586418
FEATURE [App::DocumentObjectGroupPython] G4_FREON_12  label="G4_FREON-12"  # scripted group (container) (typed FeaturePython)
  Dunit = g/cm3
  Dvalue = 1.12
  Group = -> [C_element635,F_element083,Cl_element132]
  conduct = 2
  density = 1
  expand = 3
  formula = G4_FREON-12
  name = G4_FREON-12
  specific = 4
FEATURE [App::DocumentObjectGroupPython] C_element636  label="C_element : 0.991"  # scripted group (container) (typed FeaturePython)
  n = 0.057245
FEATURE [App::DocumentObjectGroupPython] F_element084  label="F_element : 0.731"  # scripted group (container) (typed FeaturePython)
  n = 0.181096
FEATURE [App::DocumentObjectGroupPython] Br_element029  label="Br_element : 0.769"  # scripted group (container) (typed FeaturePython)
  n = 0.761659
FEATURE [App::DocumentObjectGroupPython] G4_FREON_12B2  label="G4_FREON-12B2"  # scripted group (container) (typed FeaturePython)
  Dunit = g/cm3
  Dvalue = 1.8
  Group = -> [C_element636,F_element084,Br_element029]
  conduct = 2
  density = 1
  expand = 3
  formula = G4_FREON-12B2
  name = G4_FREON-12B2
  specific = 4
FEATURE [App::DocumentObjectGroupPython] C_element637  label="C_element : 0.992"  # scripted group (container) (typed FeaturePython)
  n = 0.114983
FEATURE [App::DocumentObjectGroupPython] F_element085  label="F_element : 0.732"  # scripted group (container) (typed FeaturePython)
  n = 0.545621
FEATURE [App::DocumentObjectGroupPython] Cl_element133  label="Cl_element : 0.633"  # scripted group (container) (typed FeaturePython)
  n = 0.339396
FEATURE [App::DocumentObjectGroupPython] G4_FREON_13  label="G4_FREON-13"  # scripted group (container) (typed FeaturePython)
  Dunit = g/cm3
  Dvalue = 0.95
  Group = -> [C_element637,F_element085,Cl_element133]
  conduct = 2
  density = 1
  expand = 3
  formula = G4_FREON-13
  name = G4_FREON-13
  specific = 4
FEATURE [App::DocumentObjectGroupPython] C_element638  label="C_element : 416"  # scripted group (container) (typed FeaturePython)
  n = 1
  ref = C_element
FEATURE [App::DocumentObjectGroupPython] F_element086  label="F_element : 040"  # scripted group (container) (typed FeaturePython)
  n = 3
  ref = F_element
FEATURE [App::DocumentObjectGroupPython] Br_element030  label="Br_element : 016"  # scripted group (container) (typed FeaturePython)
  n = 1
  ref = Br_element
FEATURE [App::DocumentObjectGroupPython] G4_FREON_13B1  label="G4_FREON-13B1"  # scripted group (container) (typed FeaturePython)
  Dunit = g/cm3
  Dvalue = 1.5
  Group = -> [C_element638,F_element086,Br_element030]
  conduct = 2
  density = 1
  expand = 3
  formula = G4_FREON-13B1
  name = G4_FREON-13B1
  specific = 4
FEATURE [App::DocumentObjectGroupPython] C_element639  label="C_element : 0.993"  # scripted group (container) (typed FeaturePython)
  n = 0.061309
FEATURE [App::DocumentObjectGroupPython] F_element087  label="F_element : 0.733"  # scripted group (container) (typed FeaturePython)
  n = 0.290924
FEATURE [App::DocumentObjectGroupPython] I_element042  label="I_element : 0.657"  # scripted group (container) (typed FeaturePython)
  n = 0.647767
FEATURE [App::DocumentObjectGroupPython] G4_FREON_13I1  label="G4_FREON-13I1"  # scripted group (container) (typed FeaturePython)
  Dunit = g/cm3
  Dvalue = 1.8
  Group = -> [C_element639,F_element087,I_element042]
  conduct = 2
  density = 1
  expand = 3
  formula = G4_FREON-13I1
  name = G4_FREON-13I1
  specific = 4
FEATURE [App::DocumentObjectGroupPython] Gd_element009  label="Gd_element : 007"  # scripted group (container) (typed FeaturePython)
  n = 2
  ref = Gd_element
FEATURE [App::DocumentObjectGroupPython] O_element561  label="O_element : 357"  # scripted group (container) (typed FeaturePython)
  n = 2
  ref = O_element
FEATURE [App::DocumentObjectGroupPython] S_element104  label="S_element : 031"  # scripted group (container) (typed FeaturePython)
  n = 1
  ref = S_element
FEATURE [App::DocumentObjectGroupPython] G4_GADOLINIUM_OXYSULFIDE  # scripted group (container) (typed FeaturePython)
  Dunit = g/cm3
  Dvalue = 7.44
  Group = -> [Gd_element009,O_element561,S_element104]
  conduct = 2
  density = 1
  expand = 3
  formula = G4_GADOLINIUM_OXYSULFIDE
  name = G4_GADOLINIUM_OXYSULFIDE
  specific = 4
FEATURE [App::DocumentObjectGroupPython] Ga_element009  label="Ga_element : 008"  # scripted group (container) (typed FeaturePython)
  n = 1
  ref = Ga_element
FEATURE [App::DocumentObjectGroupPython] As_element013  label="As_element : 008"  # scripted group (container) (typed FeaturePython)
  n = 1
  ref = As_element
FEATURE [App::DocumentObjectGroupPython] G4_GALLIUM_ARSENIDE  # scripted group (container) (typed FeaturePython)
  Dunit = g/cm3
  Dvalue = 5.31
  Group = -> [Ga_element009,As_element013]
  conduct = 2
  density = 1
  expand = 3
  formula = G4_GALLIUM_ARSENIDE
  name = G4_GALLIUM_ARSENIDE
  specific = 4
FEATURE [App::DocumentObjectGroupPython] H_element593  label="H_element : 0.263"  # scripted group (container) (typed FeaturePython)
  n = 0.08118
FEATURE [App::DocumentObjectGroupPython] C_element640  label="C_element : 0.994"  # scripted group (container) (typed FeaturePython)
  n = 0.41606
FEATURE [App::DocumentObjectGroupPython] N_element290  label="N_element : 0.840"  # scripted group (container) (typed FeaturePython)
  n = 0.11124
FEATURE [App::DocumentObjectGroupPython] O_element562  label="O_element : 0.984"  # scripted group (container) (typed FeaturePython)
  n = 0.38064
FEATURE [App::DocumentObjectGroupPython] S_element105  label="S_element : 0.073"  # scripted group (container) (typed FeaturePython)
  n = 0.01088
FEATURE [App::DocumentObjectGroupPython] G4_GEL_PHOTO_EMULSION  # scripted group (container) (typed FeaturePython)
  Dunit = g/cm3
  Dvalue = 1.2914
  Group = -> [H_element593,C_element640,N_element290,O_element562,S_element105]
  conduct = 2
  density = 1
  expand = 3
  formula = G4_GEL_PHOTO_EMULSION
  name = G4_GEL_PHOTO_EMULSION
  specific = 4
FEATURE [App::DocumentObjectGroupPython] B_element032  label="B_element : 0.043"  # scripted group (container) (typed FeaturePython)
  n = 0.0400639
FEATURE [App::DocumentObjectGroupPython] O_element563  label="O_element : 0.985"  # scripted group (container) (typed FeaturePython)
  n = 0.539561
FEATURE [App::DocumentObjectGroupPython] Na_element088  label="Na_element : 0.149"  # scripted group (container) (typed FeaturePython)
  n = 0.0281909
FEATURE [App::DocumentObjectGroupPython] Al_element019  label="Al_element : 0.040"  # scripted group (container) (typed FeaturePython)
  n = 0.011644
FEATURE [App::DocumentObjectGroupPython] Si_element031  label="Si_element : 0.392"  # scripted group (container) (typed FeaturePython)
  n = 0.377219
FEATURE [App::DocumentObjectGroupPython] K_element056  label="K_element : 0.047"  # scripted group (container) (typed FeaturePython)
  n = 0.00332099
FEATURE [App::DocumentObjectGroupPython] G4_Pyrex_Glass  # scripted group (container) (typed FeaturePython)
  Dunit = g/cm3
  Dvalue = 2.23
  Group = -> [B_element032,O_element563,Na_element088,Al_element019,Si_element031,K_element056]
  conduct = 2
  density = 1
  expand = 3
  formula = G4_Pyrex_Glass
  name = G4_Pyrex_Glass
  specific = 4
FEATURE [App::DocumentObjectGroupPython] O_element564  label="O_element : 0.986"  # scripted group (container) (typed FeaturePython)
  n = 0.156453
FEATURE [App::DocumentObjectGroupPython] Si_element032  label="Si_element : 0.393"  # scripted group (container) (typed FeaturePython)
  n = 0.080866
FEATURE [App::DocumentObjectGroupPython] Ti_element017  label="Ti_element : 0.019"  # scripted group (container) (typed FeaturePython)
  n = 0.008092
FEATURE [App::DocumentObjectGroupPython] As_element014  label="As_element : 0.006"  # scripted group (container) (typed FeaturePython)
  n = 0.002651
FEATURE [App::DocumentObjectGroupPython] Pb_element025  label="Pb_element : 0.933"  # scripted group (container) (typed FeaturePython)
  n = 0.751938
FEATURE [App::DocumentObjectGroupPython] G4_GLASS_LEAD  # scripted group (container) (typed FeaturePython)
  Dunit = g/cm3
  Dvalue = 6.22
  Group = -> [O_element564,Si_element032,Ti_element017,As_element014,Pb_element025]
  conduct = 2
  density = 1
  expand = 3
  formula = G4_GLASS_LEAD
  name = G4_GLASS_LEAD
  specific = 4
FEATURE [App::DocumentObjectGroupPython] O_element565  label="O_element : 0.987"  # scripted group (container) (typed FeaturePython)
  n = 0.4598
FEATURE [App::DocumentObjectGroupPython] Na_element089  label="Na_element : 0.150"  # scripted group (container) (typed FeaturePython)
  n = 0.0964411
FEATURE [App::DocumentObjectGroupPython] Si_element033  label="Si_element : 0.394"  # scripted group (container) (typed FeaturePython)
  n = 0.336553
FEATURE [App::DocumentObjectGroupPython] Ca_element067  label="Ca_element : 0.245"  # scripted group (container) (typed FeaturePython)
  n = 0.107205
FEATURE [App::DocumentObjectGroupPython] G4_GLASS_PLATE  # scripted group (container) (typed FeaturePython)
  Dunit = g/cm3
  Dvalue = 2.4
  Group = -> [O_element565,Na_element089,Si_element033,Ca_element067]
  conduct = 2
  density = 1
  expand = 3
  formula = G4_GLASS_PLATE
  name = G4_GLASS_PLATE
  specific = 4
FEATURE [App::DocumentObjectGroupPython] C_element641  label="C_element : 417"  # scripted group (container) (typed FeaturePython)
  n = 5
  ref = C_element
FEATURE [App::DocumentObjectGroupPython] H_element594  label="H_element : 381"  # scripted group (container) (typed FeaturePython)
  n = 10
  ref = H_element
FEATURE [App::DocumentObjectGroupPython] N_element291  label="N_element : 159"  # scripted group (container) (typed FeaturePython)
  n = 2
  ref = N_element
FEATURE [App::DocumentObjectGroupPython] O_element566  label="O_element : 358"  # scripted group (container) (typed FeaturePython)
  n = 3
  ref = O_element
FEATURE [App::DocumentObjectGroupPython] G4_GLUTAMINE  # scripted group (container) (typed FeaturePython)
  Dunit = g/cm3
  Dvalue = 1.46
  Group = -> [C_element641,H_element594,N_element291,O_element566]
  conduct = 2
  density = 1
  expand = 3
  formula = G4_GLUTAMINE
  name = G4_GLUTAMINE
  specific = 4
FEATURE [App::DocumentObjectGroupPython] C_element642  label="C_element : 418"  # scripted group (container) (typed FeaturePython)
  n = 3
  ref = C_element
FEATURE [App::DocumentObjectGroupPython] H_element595  label="H_element : 382"  # scripted group (container) (typed FeaturePython)
  n = 8
  ref = H_element
FEATURE [App::DocumentObjectGroupPython] O_element567  label="O_element : 359"  # scripted group (container) (typed FeaturePython)
  n = 3
  ref = O_element
FEATURE [App::DocumentObjectGroupPython] G4_GLYCEROL  # scripted group (container) (typed FeaturePython)
  Dunit = g/cm3
  Dvalue = 1.2613
  Group = -> [C_element642,H_element595,O_element567]
  conduct = 2
  density = 1
  expand = 3
  formula = G4_GLYCEROL
  name = G4_GLYCEROL
  specific = 4
FEATURE [App::DocumentObjectGroupPython] C_element643  label="C_element : 419"  # scripted group (container) (typed FeaturePython)
  n = 5
  ref = C_element
FEATURE [App::DocumentObjectGroupPython] H_element596  label="H_element : 383"  # scripted group (container) (typed FeaturePython)
  n = 5
  ref = H_element
FEATURE [App::DocumentObjectGroupPython] N_element292  label="N_element : 160"  # scripted group (container) (typed FeaturePython)
  n = 5
  ref = N_element
FEATURE [App::DocumentObjectGroupPython] O_element568  label="O_element : 360"  # scripted group (container) (typed FeaturePython)
  n = 1
  ref = O_element
FEATURE [App::DocumentObjectGroupPython] G4_GUANINE  # scripted group (container) (typed FeaturePython)
  Dunit = g/cm3
  Dvalue = 2.2
  Group = -> [C_element643,H_element596,N_element292,O_element568]
  conduct = 2
  density = 1
  expand = 3
  formula = G4_GUANINE
  name = G4_GUANINE
  specific = 4
FEATURE [App::DocumentObjectGroupPython] Ca_element068  label="Ca_element : 033"  # scripted group (container) (typed FeaturePython)
  n = 1
  ref = Ca_element
FEATURE [App::DocumentObjectGroupPython] S_element106  label="S_element : 032"  # scripted group (container) (typed FeaturePython)
  n = 1
  ref = S_element
FEATURE [App::DocumentObjectGroupPython] O_element569  label="O_element : 361"  # scripted group (container) (typed FeaturePython)
  n = 6
  ref = O_element
FEATURE [App::DocumentObjectGroupPython] H_element597  label="H_element : 384"  # scripted group (container) (typed FeaturePython)
  n = 4
  ref = H_element
FEATURE [App::DocumentObjectGroupPython] G4_GYPSUM  # scripted group (container) (typed FeaturePython)
  Dunit = g/cm3
  Dvalue = 2.32
  Group = -> [Ca_element068,S_element106,O_element569,H_element597]
  conduct = 2
  density = 1
  expand = 3
  formula = G4_GYPSUM
  name = G4_GYPSUM
  specific = 4
FEATURE [App::DocumentObjectGroupPython] C_element644  label="C_element : 420"  # scripted group (container) (typed FeaturePython)
  n = 7
  ref = C_element
FEATURE [App::DocumentObjectGroupPython] H_element598  label="H_element : 385"  # scripted group (container) (typed FeaturePython)
  n = 16
  ref = H_element
FEATURE [App::DocumentObjectGroupPython] G4_N_HEPTANE  label="G4_N-HEPTANE"  # scripted group (container) (typed FeaturePython)
  Dunit = g/cm3
  Dvalue = 0.68376
  Group = -> [C_element644,H_element598]
  conduct = 2
  density = 1
  expand = 3
  formula = G4_N-HEPTANE
  name = G4_N-HEPTANE
  specific = 4
FEATURE [App::DocumentObjectGroupPython] C_element645  label="C_element : 421"  # scripted group (container) (typed FeaturePython)
  n = 6
  ref = C_element
FEATURE [App::DocumentObjectGroupPython] H_element599  label="H_element : 386"  # scripted group (container) (typed FeaturePython)
  n = 14
  ref = H_element
FEATURE [App::DocumentObjectGroupPython] G4_N_HEXANE  label="G4_N-HEXANE"  # scripted group (container) (typed FeaturePython)
  Dunit = g/cm3
  Dvalue = 0.6603
  Group = -> [C_element645,H_element599]
  conduct = 2
  density = 1
  expand = 3
  formula = G4_N-HEXANE
  name = G4_N-HEXANE
  specific = 4
FEATURE [App::DocumentObjectGroupPython] C_element646  label="C_element : 422"  # scripted group (container) (typed FeaturePython)
  n = 22
  ref = C_element
FEATURE [App::DocumentObjectGroupPython] H_element600  label="H_element : 387"  # scripted group (container) (typed FeaturePython)
  n = 10
  ref = H_element
FEATURE [App::DocumentObjectGroupPython] N_element293  label="N_element : 161"  # scripted group (container) (typed FeaturePython)
  n = 2
  ref = N_element
FEATURE [App::DocumentObjectGroupPython] O_element570  label="O_element : 362"  # scripted group (container) (typed FeaturePython)
  n = 5
  ref = O_element
FEATURE [App::DocumentObjectGroupPython] G4_KAPTON  # scripted group (container) (typed FeaturePython)
  Dunit = g/cm3
  Dvalue = 1.42
  Group = -> [C_element646,H_element600,N_element293,O_element570]
  conduct = 2
  density = 1
  expand = 3
  formula = G4_KAPTON
  name = G4_KAPTON
  specific = 4
FEATURE [App::DocumentObjectGroupPython] La_element013  label="La_element : 011"  # scripted group (container) (typed FeaturePython)
  n = 1
  ref = La_element
FEATURE [App::DocumentObjectGroupPython] Br_element031  label="Br_element : 017"  # scripted group (container) (typed FeaturePython)
  n = 1
  ref = Br_element
FEATURE [App::DocumentObjectGroupPython] O_element571  label="O_element : 363"  # scripted group (container) (typed FeaturePython)
  n = 1
  ref = O_element
FEATURE [App::DocumentObjectGroupPython] G4_LANTHANUM_OXYBROMIDE  # scripted group (container) (typed FeaturePython)
  Dunit = g/cm3
  Dvalue = 6.28
  Group = -> [La_element013,Br_element031,O_element571]
  conduct = 2
  density = 1
  expand = 3
  formula = G4_LANTHANUM_OXYBROMIDE
  name = G4_LANTHANUM_OXYBROMIDE
  specific = 4
FEATURE [App::DocumentObjectGroupPython] La_element014  label="La_element : 012"  # scripted group (container) (typed FeaturePython)
  n = 2
  ref = La_element
FEATURE [App::DocumentObjectGroupPython] O_element572  label="O_element : 364"  # scripted group (container) (typed FeaturePython)
  n = 2
  ref = O_element
FEATURE [App::DocumentObjectGroupPython] S_element107  label="S_element : 033"  # scripted group (container) (typed FeaturePython)
  n = 1
  ref = S_element
FEATURE [App::DocumentObjectGroupPython] G4_LANTHANUM_OXYSULFIDE  # scripted group (container) (typed FeaturePython)
  Dunit = g/cm3
  Dvalue = 5.86
  Group = -> [La_element014,O_element572,S_element107]
  conduct = 2
  density = 1
  expand = 3
  formula = G4_LANTHANUM_OXYSULFIDE
  name = G4_LANTHANUM_OXYSULFIDE
  specific = 4
FEATURE [App::DocumentObjectGroupPython] O_element573  label="O_element : 0.988"  # scripted group (container) (typed FeaturePython)
  n = 0.071682
FEATURE [App::DocumentObjectGroupPython] Pb_element026  label="Pb_element : 0.934"  # scripted group (container) (typed FeaturePython)
  n = 0.928318
FEATURE [App::DocumentObjectGroupPython] G4_LEAD_OXIDE  # scripted group (container) (typed FeaturePython)
  Dunit = g/cm3
  Dvalue = 9.53
  Group = -> [O_element573,Pb_element026]
  conduct = 2
  density = 1
  expand = 3
  formula = G4_LEAD_OXIDE
  name = G4_LEAD_OXIDE
  specific = 4
FEATURE [App::DocumentObjectGroupPython] Li_element033  label="Li_element : 031"  # scripted group (container) (typed FeaturePython)
  n = 1
  ref = Li_element
FEATURE [App::DocumentObjectGroupPython] N_element294  label="N_element : 162"  # scripted group (container) (typed FeaturePython)
  n = 1
  ref = N_element
FEATURE [App::DocumentObjectGroupPython] H_element601  label="H_element : 388"  # scripted group (container) (typed FeaturePython)
  n = 2
  ref = H_element
FEATURE [App::DocumentObjectGroupPython] G4_LITHIUM_AMIDE  # scripted group (container) (typed FeaturePython)
  Dunit = g/cm3
  Dvalue = 1.178
  Group = -> [Li_element033,N_element294,H_element601]
  conduct = 2
  density = 1
  expand = 3
  formula = G4_LITHIUM_AMIDE
  name = G4_LITHIUM_AMIDE
  specific = 4
FEATURE [App::DocumentObjectGroupPython] Li_element034  label="Li_element : 032"  # scripted group (container) (typed FeaturePython)
  n = 2
  ref = Li_element
FEATURE [App::DocumentObjectGroupPython] C_element647  label="C_element : 423"  # scripted group (container) (typed FeaturePython)
  n = 1
  ref = C_element
FEATURE [App::DocumentObjectGroupPython] O_element574  label="O_element : 365"  # scripted group (container) (typed FeaturePython)
  n = 3
  ref = O_element
FEATURE [App::DocumentObjectGroupPython] G4_LITHIUM_CARBONATE  # scripted group (container) (typed FeaturePython)
  Dunit = g/cm3
  Dvalue = 2.11
  Group = -> [Li_element034,C_element647,O_element574]
  conduct = 2
  density = 1
  expand = 3
  formula = G4_LITHIUM_CARBONATE
  name = G4_LITHIUM_CARBONATE
  specific = 4
FEATURE [App::DocumentObjectGroupPython] Li_element035  label="Li_element : 033"  # scripted group (container) (typed FeaturePython)
  n = 1
  ref = Li_element
FEATURE [App::DocumentObjectGroupPython] F_element088  label="F_element : 041"  # scripted group (container) (typed FeaturePython)
  n = 1
  ref = F_element
FEATURE [App::DocumentObjectGroupPython] G4_LITHIUM_FLUORIDE  # scripted group (container) (typed FeaturePython)
  Dunit = g/cm3
  Dvalue = 2.635
  Group = -> [Li_element035,F_element088]
  conduct = 2
  density = 1
  expand = 3
  formula = G4_LITHIUM_FLUORIDE
  name = G4_LITHIUM_FLUORIDE
  specific = 4
FEATURE [App::DocumentObjectGroupPython] Li_element036  label="Li_element : 034"  # scripted group (container) (typed FeaturePython)
  n = 1
  ref = Li_element
FEATURE [App::DocumentObjectGroupPython] H_element602  label="H_element : 389"  # scripted group (container) (typed FeaturePython)
  n = 1
  ref = H_element
FEATURE [App::DocumentObjectGroupPython] G4_LITHIUM_HYDRIDE  # scripted group (container) (typed FeaturePython)
  Dunit = g/cm3
  Dvalue = 0.82
  Group = -> [Li_element036,H_element602]
  conduct = 2
  density = 1
  expand = 3
  formula = G4_LITHIUM_HYDRIDE
  name = G4_LITHIUM_HYDRIDE
  specific = 4
FEATURE [App::DocumentObjectGroupPython] Li_element037  label="Li_element : 035"  # scripted group (container) (typed FeaturePython)
  n = 1
  ref = Li_element
FEATURE [App::DocumentObjectGroupPython] I_element043  label="I_element : 027"  # scripted group (container) (typed FeaturePython)
  n = 1
  ref = I_element
FEATURE [App::DocumentObjectGroupPython] G4_LITHIUM_IODIDE  # scripted group (container) (typed FeaturePython)
  Dunit = g/cm3
  Dvalue = 3.494
  Group = -> [Li_element037,I_element043]
  conduct = 2
  density = 1
  expand = 3
  formula = G4_LITHIUM_IODIDE
  name = G4_LITHIUM_IODIDE
  specific = 4
FEATURE [App::DocumentObjectGroupPython] Li_element038  label="Li_element : 036"  # scripted group (container) (typed FeaturePython)
  n = 2
  ref = Li_element
FEATURE [App::DocumentObjectGroupPython] O_element575  label="O_element : 366"  # scripted group (container) (typed FeaturePython)
  n = 1
  ref = O_element
FEATURE [App::DocumentObjectGroupPython] G4_LITHIUM_OXIDE  # scripted group (container) (typed FeaturePython)
  Dunit = g/cm3
  Dvalue = 2.013
  Group = -> [Li_element038,O_element575]
  conduct = 2
  density = 1
  expand = 3
  formula = G4_LITHIUM_OXIDE
  name = G4_LITHIUM_OXIDE
  specific = 4
FEATURE [App::DocumentObjectGroupPython] Li_element039  label="Li_element : 037"  # scripted group (container) (typed FeaturePython)
  n = 2
  ref = Li_element
FEATURE [App::DocumentObjectGroupPython] B_element033  label="B_element : 026"  # scripted group (container) (typed FeaturePython)
  n = 4
  ref = B_element
FEATURE [App::DocumentObjectGroupPython] O_element576  label="O_element : 367"  # scripted group (container) (typed FeaturePython)
  n = 7
  ref = O_element
FEATURE [App::DocumentObjectGroupPython] G4_LITHIUM_TETRABORATE  # scripted group (container) (typed FeaturePython)
  Dunit = g/cm3
  Dvalue = 2.44
  Group = -> [Li_element039,B_element033,O_element576]
  conduct = 2
  density = 1
  expand = 3
  formula = G4_LITHIUM_TETRABORATE
  name = G4_LITHIUM_TETRABORATE
  specific = 4
FEATURE [App::DocumentObjectGroupPython] H_element603  label="H_element : 0.264"  # scripted group (container) (typed FeaturePython)
  n = 0.105
FEATURE [App::DocumentObjectGroupPython] C_element648  label="C_element : 0.995"  # scripted group (container) (typed FeaturePython)
  n = 0.083
FEATURE [App::DocumentObjectGroupPython] N_element295  label="N_element : 0.841"  # scripted group (container) (typed FeaturePython)
  n = 0.023
FEATURE [App::DocumentObjectGroupPython] O_element577  label="O_element : 0.989"  # scripted group (container) (typed FeaturePython)
  n = 0.779
FEATURE [App::DocumentObjectGroupPython] Na_element090  label="Na_element : 0.151"  # scripted group (container) (typed FeaturePython)
  n = 0.002
FEATURE [App::DocumentObjectGroupPython] P_element082  label="P_element : 0.143"  # scripted group (container) (typed FeaturePython)
  n = 0.001
FEATURE [App::DocumentObjectGroupPython] S_element108  label="S_element : 0.074"  # scripted group (container) (typed FeaturePython)
  n = 0.002
FEATURE [App::DocumentObjectGroupPython] Cl_element134  label="Cl_element : 0.634"  # scripted group (container) (typed FeaturePython)
  n = 0.003
FEATURE [App::DocumentObjectGroupPython] K_element057  label="K_element : 0.048"  # scripted group (container) (typed FeaturePython)
  n = 0.002
FEATURE [App::DocumentObjectGroupPython] G4_LUNG_ICRP  # scripted group (container) (typed FeaturePython)
  Dunit = g/cm3
  Dvalue = 1.04
  Group = -> [H_element603,C_element648,N_element295,O_element577,Na_element090,P_element082,S_element108,Cl_element134,K_element057]
  conduct = 2
  density = 1
  expand = 3
  formula = G4_LUNG_ICRP
  name = G4_LUNG_ICRP
  specific = 4
FEATURE [App::DocumentObjectGroupPython] H_element604  label="H_element : 0.265"  # scripted group (container) (typed FeaturePython)
  n = 0.114318
FEATURE [App::DocumentObjectGroupPython] C_element649  label="C_element : 0.996"  # scripted group (container) (typed FeaturePython)
  n = 0.655824
FEATURE [App::DocumentObjectGroupPython] O_element578  label="O_element : 0.990"  # scripted group (container) (typed FeaturePython)
  n = 0.0921831
FEATURE [App::DocumentObjectGroupPython] Mg_element048  label="Mg_element : 0.153"  # scripted group (container) (typed FeaturePython)
  n = 0.134792
FEATURE [App::DocumentObjectGroupPython] Ca_element069  label="Ca_element : 0.246"  # scripted group (container) (typed FeaturePython)
  n = 0.002883
FEATURE [App::DocumentObjectGroupPython] G4_M3_WAX  # scripted group (container) (typed FeaturePython)
  Dunit = g/cm3
  Dvalue = 1.05
  Group = -> [H_element604,C_element649,O_element578,Mg_element048,Ca_element069]
  conduct = 2
  density = 1
  expand = 3
  formula = G4_M3_WAX
  name = G4_M3_WAX
  specific = 4
FEATURE [App::DocumentObjectGroupPython] Mg_element049  label="Mg_element : 020"  # scripted group (container) (typed FeaturePython)
  n = 1
  ref = Mg_element
FEATURE [App::DocumentObjectGroupPython] C_element650  label="C_element : 424"  # scripted group (container) (typed FeaturePython)
  n = 1
  ref = C_element
FEATURE [App::DocumentObjectGroupPython] O_element579  label="O_element : 368"  # scripted group (container) (typed FeaturePython)
  n = 3
  ref = O_element
FEATURE [App::DocumentObjectGroupPython] G4_MAGNESIUM_CARBONATE  # scripted group (container) (typed FeaturePython)
  Dunit = g/cm3
  Dvalue = 2.958
  Group = -> [Mg_element049,C_element650,O_element579]
  conduct = 2
  density = 1
  expand = 3
  formula = G4_MAGNESIUM_CARBONATE
  name = G4_MAGNESIUM_CARBONATE
  specific = 4
FEATURE [App::DocumentObjectGroupPython] Mg_element050  label="Mg_element : 021"  # scripted group (container) (typed FeaturePython)
  n = 1
  ref = Mg_element
FEATURE [App::DocumentObjectGroupPython] F_element089  label="F_element : 042"  # scripted group (container) (typed FeaturePython)
  n = 2
  ref = F_element
FEATURE [App::DocumentObjectGroupPython] G4_MAGNESIUM_FLUORIDE  # scripted group (container) (typed FeaturePython)
  Dunit = g/cm3
  Dvalue = 3
  Group = -> [Mg_element050,F_element089]
  conduct = 2
  density = 1
  expand = 3
  formula = G4_MAGNESIUM_FLUORIDE
  name = G4_MAGNESIUM_FLUORIDE
  specific = 4
FEATURE [App::DocumentObjectGroupPython] Mg_element051  label="Mg_element : 022"  # scripted group (container) (typed FeaturePython)
  n = 1
  ref = Mg_element
FEATURE [App::DocumentObjectGroupPython] O_element580  label="O_element : 369"  # scripted group (container) (typed FeaturePython)
  n = 1
  ref = O_element
FEATURE [App::DocumentObjectGroupPython] G4_MAGNESIUM_OXIDE  # scripted group (container) (typed FeaturePython)
  Dunit = g/cm3
  Dvalue = 3.58
  Group = -> [Mg_element051,O_element580]
  conduct = 2
  density = 1
  expand = 3
  formula = G4_MAGNESIUM_OXIDE
  name = G4_MAGNESIUM_OXIDE
  specific = 4
FEATURE [App::DocumentObjectGroupPython] Mg_element052  label="Mg_element : 023"  # scripted group (container) (typed FeaturePython)
  n = 1
  ref = Mg_element
FEATURE [App::DocumentObjectGroupPython] B_element034  label="B_element : 027"  # scripted group (container) (typed FeaturePython)
  n = 4
  ref = B_element
FEATURE [App::DocumentObjectGroupPython] O_element581  label="O_element : 370"  # scripted group (container) (typed FeaturePython)
  n = 7
  ref = O_element
FEATURE [App::DocumentObjectGroupPython] G4_MAGNESIUM_TETRABORATE  # scripted group (container) (typed FeaturePython)
  Dunit = g/cm3
  Dvalue = 2.53
  Group = -> [Mg_element052,B_element034,O_element581]
  conduct = 2
  density = 1
  expand = 3
  formula = G4_MAGNESIUM_TETRABORATE
  name = G4_MAGNESIUM_TETRABORATE
  specific = 4
FEATURE [App::DocumentObjectGroupPython] Hg_element009  label="Hg_element : 008"  # scripted group (container) (typed FeaturePython)
  n = 1
  ref = Hg_element
FEATURE [App::DocumentObjectGroupPython] I_element044  label="I_element : 028"  # scripted group (container) (typed FeaturePython)
  n = 2
  ref = I_element
FEATURE [App::DocumentObjectGroupPython] G4_MERCURIC_IODIDE  # scripted group (container) (typed FeaturePython)
  Dunit = g/cm3
  Dvalue = 6.36
  Group = -> [Hg_element009,I_element044]
  conduct = 2
  density = 1
  expand = 3
  formula = G4_MERCURIC_IODIDE
  name = G4_MERCURIC_IODIDE
  specific = 4
FEATURE [App::DocumentObjectGroupPython] C_element651  label="C_element : 425"  # scripted group (container) (typed FeaturePython)
  n = 1
  ref = C_element
FEATURE [App::DocumentObjectGroupPython] H_element605  label="H_element : 390"  # scripted group (container) (typed FeaturePython)
  n = 4
  ref = H_element
FEATURE [App::DocumentObjectGroupPython] G4_METHANE  # scripted group (container) (typed FeaturePython)
  Dunit = g/cm3
  Dvalue = 0.000667151
  Group = -> [C_element651,H_element605]
  conduct = 2
  density = 1
  expand = 3
  formula = G4_METHANE
  name = G4_METHANE
  specific = 4
FEATURE [App::DocumentObjectGroupPython] C_element652  label="C_element : 426"  # scripted group (container) (typed FeaturePython)
  n = 1
  ref = C_element
FEATURE [App::DocumentObjectGroupPython] H_element606  label="H_element : 391"  # scripted group (container) (typed FeaturePython)
  n = 4
  ref = H_element
FEATURE [App::DocumentObjectGroupPython] O_element582  label="O_element : 371"  # scripted group (container) (typed FeaturePython)
  n = 1
  ref = O_element
FEATURE [App::DocumentObjectGroupPython] G4_METHANOL  # scripted group (container) (typed FeaturePython)
  Dunit = g/cm3
  Dvalue = 0.7914
  Group = -> [C_element652,H_element606,O_element582]
  conduct = 2
  density = 1
  expand = 3
  formula = G4_METHANOL
  name = G4_METHANOL
  specific = 4
FEATURE [App::DocumentObjectGroupPython] H_element607  label="H_element : 0.266"  # scripted group (container) (typed FeaturePython)
  n = 0.13404
FEATURE [App::DocumentObjectGroupPython] C_element653  label="C_element : 0.997"  # scripted group (container) (typed FeaturePython)
  n = 0.77796
FEATURE [App::DocumentObjectGroupPython] O_element583  label="O_element : 0.991"  # scripted group (container) (typed FeaturePython)
  n = 0.03502
FEATURE [App::DocumentObjectGroupPython] Mg_element053  label="Mg_element : 0.154"  # scripted group (container) (typed FeaturePython)
  n = 0.038594
FEATURE [App::DocumentObjectGroupPython] Ti_element018  label="Ti_element : 0.020"  # scripted group (container) (typed FeaturePython)
  n = 0.014386
FEATURE [App::DocumentObjectGroupPython] G4_MIX_D_WAX  # scripted group (container) (typed FeaturePython)
  Dunit = g/cm3
  Dvalue = 0.99
  Group = -> [H_element607,C_element653,O_element583,Mg_element053,Ti_element018]
  conduct = 2
  density = 1
  expand = 3
  formula = G4_MIX_D_WAX
  name = G4_MIX_D_WAX
  specific = 4
FEATURE [App::DocumentObjectGroupPython] H_element608  label="H_element : 0.267"  # scripted group (container) (typed FeaturePython)
  n = 0.081192
FEATURE [App::DocumentObjectGroupPython] C_element654  label="C_element : 0.998"  # scripted group (container) (typed FeaturePython)
  n = 0.583442
FEATURE [App::DocumentObjectGroupPython] N_element296  label="N_element : 0.842"  # scripted group (container) (typed FeaturePython)
  n = 0.017798
FEATURE [App::DocumentObjectGroupPython] O_element584  label="O_element : 0.992"  # scripted group (container) (typed FeaturePython)
  n = 0.186381
FEATURE [App::DocumentObjectGroupPython] Mg_element054  label="Mg_element : 0.155"  # scripted group (container) (typed FeaturePython)
  n = 0.130287
FEATURE [App::DocumentObjectGroupPython] Cl_element135  label="Cl_element : 0.635"  # scripted group (container) (typed FeaturePython)
  n = 0.0009
FEATURE [App::DocumentObjectGroupPython] G4_MS20_TISSUE  # scripted group (container) (typed FeaturePython)
  Dunit = g/cm3
  Dvalue = 1
  Group = -> [H_element608,C_element654,N_element296,O_element584,Mg_element054,Cl_element135]
  conduct = 2
  density = 1
  expand = 3
  formula = G4_MS20_TISSUE
  name = G4_MS20_TISSUE
  specific = 4
FEATURE [App::DocumentObjectGroupPython] H_element609  label="H_element : 0.268"  # scripted group (container) (typed FeaturePython)
  n = 0.102
FEATURE [App::DocumentObjectGroupPython] C_element655  label="C_element : 0.999"  # scripted group (container) (typed FeaturePython)
  n = 0.143
FEATURE [App::DocumentObjectGroupPython] N_element297  label="N_element : 0.843"  # scripted group (container) (typed FeaturePython)
  n = 0.034
FEATURE [App::DocumentObjectGroupPython] O_element585  label="O_element : 0.993"  # scripted group (container) (typed FeaturePython)
  n = 0.71
FEATURE [App::DocumentObjectGroupPython] Na_element091  label="Na_element : 0.152"  # scripted group (container) (typed FeaturePython)
  n = 0.001
FEATURE [App::DocumentObjectGroupPython] P_element083  label="P_element : 0.144"  # scripted group (container) (typed FeaturePython)
  n = 0.002
FEATURE [App::DocumentObjectGroupPython] S_element109  label="S_element : 0.075"  # scripted group (container) (typed FeaturePython)
  n = 0.003
FEATURE [App::DocumentObjectGroupPython] Cl_element136  label="Cl_element : 0.636"  # scripted group (container) (typed FeaturePython)
  n = 0.001
FEATURE [App::DocumentObjectGroupPython] K_element058  label="K_element : 0.049"  # scripted group (container) (typed FeaturePython)
  n = 0.004
FEATURE [App::DocumentObjectGroupPython] G4_MUSCLE_SKELETAL_ICRP  # scripted group (container) (typed FeaturePython)
  Dunit = g/cm3
  Dvalue = 1.05
  Group = -> [H_element609,C_element655,N_element297,O_element585,Na_element091,P_element083,S_element109,Cl_element136,K_element058]
  conduct = 2
  density = 1
  expand = 3
  formula = G4_MUSCLE_SKELETAL_ICRP
  name = G4_MUSCLE_SKELETAL_ICRP
  specific = 4
FEATURE [App::DocumentObjectGroupPython] H_element610  label="H_element : 0.269"  # scripted group (container) (typed FeaturePython)
  n = 0.102102
FEATURE [App::DocumentObjectGroupPython] C_element656  label="C_element : 0.1000"  # scripted group (container) (typed FeaturePython)
  n = 0.123123
FEATURE [App::DocumentObjectGroupPython] N_element298  label="N_element : 0.844"  # scripted group (container) (typed FeaturePython)
  n = 0.035035
FEATURE [App::DocumentObjectGroupPython] O_element586  label="O_element : 0.994"  # scripted group (container) (typed FeaturePython)
  n = 0.72973
FEATURE [App::DocumentObjectGroupPython] Na_element092  label="Na_element : 0.153"  # scripted group (container) (typed FeaturePython)
  n = 0.001001
FEATURE [App::DocumentObjectGroupPython] P_element084  label="P_element : 0.145"  # scripted group (container) (typed FeaturePython)
  n = 0.002002
FEATURE [App::DocumentObjectGroupPython] S_element110  label="S_element : 0.076"  # scripted group (container) (typed FeaturePython)
  n = 0.004004
FEATURE [App::DocumentObjectGroupPython] K_element059  label="K_element : 0.050"  # scripted group (container) (typed FeaturePython)
  n = 0.003003
FEATURE [App::DocumentObjectGroupPython] G4_MUSCLE_STRIATED_ICRU  # scripted group (container) (typed FeaturePython)
  Dunit = g/cm3
  Dvalue = 1.04
  Group = -> [H_element610,C_element656,N_element298,O_element586,Na_element092,P_element084,S_element110,K_element059]
  conduct = 2
  density = 1
  expand = 3
  formula = G4_MUSCLE_STRIATED_ICRU
  name = G4_MUSCLE_STRIATED_ICRU
  specific = 4
FEATURE [App::DocumentObjectGroupPython] H_element611  label="H_element : 0.270"  # scripted group (container) (typed FeaturePython)
  n = 0.0982341
FEATURE [App::DocumentObjectGroupPython] C_element657  label="C_element : 0.1001"  # scripted group (container) (typed FeaturePython)
  n = 0.156214
FEATURE [App::DocumentObjectGroupPython] N_element299  label="N_element : 0.845"  # scripted group (container) (typed FeaturePython)
  n = 0.035451
FEATURE [App::DocumentObjectGroupPython] O_element587  label="O_element : 0.995"  # scripted group (container) (typed FeaturePython)
  n = 0.710101
FEATURE [App::DocumentObjectGroupPython] G4_MUSCLE_WITH_SUCROSE  # scripted group (container) (typed FeaturePython)
  Dunit = g/cm3
  Dvalue = 1.11
  Group = -> [H_element611,C_element657,N_element299,O_element587]
  conduct = 2
  density = 1
  expand = 3
  formula = G4_MUSCLE_WITH_SUCROSE
  name = G4_MUSCLE_WITH_SUCROSE
  specific = 4
FEATURE [App::DocumentObjectGroupPython] H_element612  label="H_element : 0.271"  # scripted group (container) (typed FeaturePython)
  n = 0.101969
FEATURE [App::DocumentObjectGroupPython] C_element658  label="C_element : 0.1002"  # scripted group (container) (typed FeaturePython)
  n = 0.120058
FEATURE [App::DocumentObjectGroupPython] N_element300  label="N_element : 0.846"  # scripted group (container) (typed FeaturePython)
  n = 0.035451
FEATURE [App::DocumentObjectGroupPython] O_element588  label="O_element : 0.996"  # scripted group (container) (typed FeaturePython)
  n = 0.742522
FEATURE [App::DocumentObjectGroupPython] G4_MUSCLE_WITHOUT_SUCROSE  # scripted group (container) (typed FeaturePython)
  Dunit = g/cm3
  Dvalue = 1.07
  Group = -> [H_element612,C_element658,N_element300,O_element588]
  conduct = 2
  density = 1
  expand = 3
  formula = G4_MUSCLE_WITHOUT_SUCROSE
  name = G4_MUSCLE_WITHOUT_SUCROSE
  specific = 4
FEATURE [App::DocumentObjectGroupPython] C_element659  label="C_element : 427"  # scripted group (container) (typed FeaturePython)
  n = 10
  ref = C_element
FEATURE [App::DocumentObjectGroupPython] H_element613  label="H_element : 392"  # scripted group (container) (typed FeaturePython)
  n = 8
  ref = H_element
FEATURE [App::DocumentObjectGroupPython] G4_NAPHTHALENE  # scripted group (container) (typed FeaturePython)
  Dunit = g/cm3
  Dvalue = 1.145
  Group = -> [C_element659,H_element613]
  conduct = 2
  density = 1
  expand = 3
  formula = G4_NAPHTHALENE
  name = G4_NAPHTHALENE
  specific = 4
FEATURE [App::DocumentObjectGroupPython] C_element660  label="C_element : 428"  # scripted group (container) (typed FeaturePython)
  n = 6
  ref = C_element
FEATURE [App::DocumentObjectGroupPython] H_element614  label="H_element : 393"  # scripted group (container) (typed FeaturePython)
  n = 5
  ref = H_element
FEATURE [App::DocumentObjectGroupPython] N_element301  label="N_element : 163"  # scripted group (container) (typed FeaturePython)
  n = 1
  ref = N_element
FEATURE [App::DocumentObjectGroupPython] O_element589  label="O_element : 372"  # scripted group (container) (typed FeaturePython)
  n = 2
  ref = O_element
FEATURE [App::DocumentObjectGroupPython] G4_NITROBENZENE  # scripted group (container) (typed FeaturePython)
  Dunit = g/cm3
  Dvalue = 1.19867
  Group = -> [C_element660,H_element614,N_element301,O_element589]
  conduct = 2
  density = 1
  expand = 3
  formula = G4_NITROBENZENE
  name = G4_NITROBENZENE
  specific = 4
FEATURE [App::DocumentObjectGroupPython] N_element302  label="N_element : 164"  # scripted group (container) (typed FeaturePython)
  n = 2
  ref = N_element
FEATURE [App::DocumentObjectGroupPython] O_element590  label="O_element : 373"  # scripted group (container) (typed FeaturePython)
  n = 1
  ref = O_element
FEATURE [App::DocumentObjectGroupPython] G4_NITROUS_OXIDE  # scripted group (container) (typed FeaturePython)
  Dunit = g/cm3
  Dvalue = 0.00183094
  Group = -> [N_element302,O_element590]
  conduct = 2
  density = 1
  expand = 3
  formula = G4_NITROUS_OXIDE
  name = G4_NITROUS_OXIDE
  specific = 4
FEATURE [App::DocumentObjectGroupPython] H_element615  label="H_element : 0.272"  # scripted group (container) (typed FeaturePython)
  n = 0.103509
FEATURE [App::DocumentObjectGroupPython] C_element661  label="C_element : 0.1003"  # scripted group (container) (typed FeaturePython)
  n = 0.648416
FEATURE [App::DocumentObjectGroupPython] N_element303  label="N_element : 0.847"  # scripted group (container) (typed FeaturePython)
  n = 0.0995361
FEATURE [App::DocumentObjectGroupPython] O_element591  label="O_element : 0.997"  # scripted group (container) (typed FeaturePython)
  n = 0.148539
FEATURE [App::DocumentObjectGroupPython] G4_NYLON_8062  label="G4_NYLON-8062"  # scripted group (container) (typed FeaturePython)
  Dunit = g/cm3
  Dvalue = 1.08
  Group = -> [H_element615,C_element661,N_element303,O_element591]
  conduct = 2
  density = 1
  expand = 3
  formula = G4_NYLON-8062
  name = G4_NYLON-8062
  specific = 4
FEATURE [App::DocumentObjectGroupPython] C_element662  label="C_element : 429"  # scripted group (container) (typed FeaturePython)
  n = 6
  ref = C_element
FEATURE [App::DocumentObjectGroupPython] H_element616  label="H_element : 394"  # scripted group (container) (typed FeaturePython)
  n = 11
  ref = H_element
FEATURE [App::DocumentObjectGroupPython] N_element304  label="N_element : 165"  # scripted group (container) (typed FeaturePython)
  n = 1
  ref = N_element
FEATURE [App::DocumentObjectGroupPython] O_element592  label="O_element : 374"  # scripted group (container) (typed FeaturePython)
  n = 1
  ref = O_element
FEATURE [App::DocumentObjectGroupPython] G4_NYLON_6_6  label="G4_NYLON-6-6"  # scripted group (container) (typed FeaturePython)
  Dunit = g/cm3
  Dvalue = 1.14
  Group = -> [C_element662,H_element616,N_element304,O_element592]
  conduct = 2
  density = 1
  expand = 3
  formula = G4_NYLON-6-6
  name = G4_NYLON-6-6
  specific = 4
FEATURE [App::DocumentObjectGroupPython] H_element617  label="H_element : 0.273"  # scripted group (container) (typed FeaturePython)
  n = 0.107062
FEATURE [App::DocumentObjectGroupPython] C_element663  label="C_element : 0.1004"  # scripted group (container) (typed FeaturePython)
  n = 0.680449
FEATURE [App::DocumentObjectGroupPython] N_element305  label="N_element : 0.848"  # scripted group (container) (typed FeaturePython)
  n = 0.099189
FEATURE [App::DocumentObjectGroupPython] O_element593  label="O_element : 0.998"  # scripted group (container) (typed FeaturePython)
  n = 0.1133
FEATURE [App::DocumentObjectGroupPython] G4_NYLON_6_10  label="G4_NYLON-6-10"  # scripted group (container) (typed FeaturePython)
  Dunit = g/cm3
  Dvalue = 1.14
  Group = -> [H_element617,C_element663,N_element305,O_element593]
  conduct = 2
  density = 1
  expand = 3
  formula = G4_NYLON-6-10
  name = G4_NYLON-6-10
  specific = 4
FEATURE [App::DocumentObjectGroupPython] H_element618  label="H_element : 0.274"  # scripted group (container) (typed FeaturePython)
  n = 0.115476
FEATURE [App::DocumentObjectGroupPython] C_element664  label="C_element : 0.1005"  # scripted group (container) (typed FeaturePython)
  n = 0.720818
FEATURE [App::DocumentObjectGroupPython] N_element306  label="N_element : 0.849"  # scripted group (container) (typed FeaturePython)
  n = 0.0764169
FEATURE [App::DocumentObjectGroupPython] O_element594  label="O_element : 0.999"  # scripted group (container) (typed FeaturePython)
  n = 0.0872889
FEATURE [App::DocumentObjectGroupPython] G4_NYLON_11_RILSAN  label="G4_NYLON-11_RILSAN"  # scripted group (container) (typed FeaturePython)
  Dunit = g/cm3
  Dvalue = 1.425
  Group = -> [H_element618,C_element664,N_element306,O_element594]
  conduct = 2
  density = 1
  expand = 3
  formula = G4_NYLON-11_RILSAN
  name = G4_NYLON-11_RILSAN
  specific = 4
FEATURE [App::DocumentObjectGroupPython] C_element665  label="C_element : 430"  # scripted group (container) (typed FeaturePython)
  n = 8
  ref = C_element
FEATURE [App::DocumentObjectGroupPython] H_element619  label="H_element : 395"  # scripted group (container) (typed FeaturePython)
  n = 18
  ref = H_element
FEATURE [App::DocumentObjectGroupPython] G4_OCTANE  # scripted group (container) (typed FeaturePython)
  Dunit = g/cm3
  Dvalue = 0.7026
  Group = -> [C_element665,H_element619]
  conduct = 2
  density = 1
  expand = 3
  formula = G4_OCTANE
  name = G4_OCTANE
  specific = 4
FEATURE [App::DocumentObjectGroupPython] C_element666  label="C_element : 431"  # scripted group (container) (typed FeaturePython)
  n = 25
  ref = C_element
FEATURE [App::DocumentObjectGroupPython] H_element620  label="H_element : 396"  # scripted group (container) (typed FeaturePython)
  n = 52
  ref = H_element
FEATURE [App::DocumentObjectGroupPython] G4_PARAFFIN  # scripted group (container) (typed FeaturePython)
  Dunit = g/cm3
  Dvalue = 0.93
  Group = -> [C_element666,H_element620]
  conduct = 2
  density = 1
  expand = 3
  formula = G4_PARAFFIN
  name = G4_PARAFFIN
  specific = 4
FEATURE [App::DocumentObjectGroupPython] C_element667  label="C_element : 432"  # scripted group (container) (typed FeaturePython)
  n = 5
  ref = C_element
FEATURE [App::DocumentObjectGroupPython] H_element621  label="H_element : 397"  # scripted group (container) (typed FeaturePython)
  n = 12
  ref = H_element
FEATURE [App::DocumentObjectGroupPython] G4_N_PENTANE  label="G4_N-PENTANE"  # scripted group (container) (typed FeaturePython)
  Dunit = g/cm3
  Dvalue = 0.6262
  Group = -> [C_element667,H_element621]
  conduct = 2
  density = 1
  expand = 3
  formula = G4_N-PENTANE
  name = G4_N-PENTANE
  specific = 4
FEATURE [App::DocumentObjectGroupPython] H_element622  label="H_element : 0.275"  # scripted group (container) (typed FeaturePython)
  n = 0.0141
FEATURE [App::DocumentObjectGroupPython] C_element668  label="C_element : 0.1006"  # scripted group (container) (typed FeaturePython)
  n = 0.072261
FEATURE [App::DocumentObjectGroupPython] N_element307  label="N_element : 0.850"  # scripted group (container) (typed FeaturePython)
  n = 0.01932
FEATURE [App::DocumentObjectGroupPython] O_element595  label="O_element : 0.1000"  # scripted group (container) (typed FeaturePython)
  n = 0.066101
FEATURE [App::DocumentObjectGroupPython] S_element111  label="S_element : 0.077"  # scripted group (container) (typed FeaturePython)
  n = 0.00189
FEATURE [App::DocumentObjectGroupPython] Br_element032  label="Br_element : 0.770"  # scripted group (container) (typed FeaturePython)
  n = 0.349103
FEATURE [App::DocumentObjectGroupPython] Ag_element025  label="Ag_element : 0.579"  # scripted group (container) (typed FeaturePython)
  n = 0.474105
FEATURE [App::DocumentObjectGroupPython] I_element045  label="I_element : 0.658"  # scripted group (container) (typed FeaturePython)
  n = 0.00312
FEATURE [App::DocumentObjectGroupPython] G4_PHOTO_EMULSION  # scripted group (container) (typed FeaturePython)
  Dunit = g/cm3
  Dvalue = 3.815
  Group = -> [H_element622,C_element668,N_element307,O_element595,S_element111,Br_element032,Ag_element025,I_element045]
  conduct = 2
  density = 1
  expand = 3
  formula = G4_PHOTO_EMULSION
  name = G4_PHOTO_EMULSION
  specific = 4
FEATURE [App::DocumentObjectGroupPython] C_element669  label="C_element : 433"  # scripted group (container) (typed FeaturePython)
  n = 9
  ref = C_element
FEATURE [App::DocumentObjectGroupPython] H_element623  label="H_element : 398"  # scripted group (container) (typed FeaturePython)
  n = 10
  ref = H_element
FEATURE [App::DocumentObjectGroupPython] G4_PLASTIC_SC_VINYLTOLUENE  # scripted group (container) (typed FeaturePython)
  Dunit = g/cm3
  Dvalue = 1.032
  Group = -> [C_element669,H_element623]
  conduct = 2
  density = 1
  expand = 3
  formula = G4_PLASTIC_SC_VINYLTOLUENE
  name = G4_PLASTIC_SC_VINYLTOLUENE
  specific = 4
FEATURE [App::DocumentObjectGroupPython] Pu_element009  label="Pu_element : 008"  # scripted group (container) (typed FeaturePython)
  n = 1
  ref = Pu_element
FEATURE [App::DocumentObjectGroupPython] O_element596  label="O_element : 375"  # scripted group (container) (typed FeaturePython)
  n = 2
  ref = O_element
FEATURE [App::DocumentObjectGroupPython] G4_PLUTONIUM_DIOXIDE  # scripted group (container) (typed FeaturePython)
  Dunit = g/cm3
  Dvalue = 11.46
  Group = -> [Pu_element009,O_element596]
  conduct = 2
  density = 1
  expand = 3
  formula = G4_PLUTONIUM_DIOXIDE
  name = G4_PLUTONIUM_DIOXIDE
  specific = 4
FEATURE [App::DocumentObjectGroupPython] C_element670  label="C_element : 434"  # scripted group (container) (typed FeaturePython)
  n = 3
  ref = C_element
FEATURE [App::DocumentObjectGroupPython] H_element624  label="H_element : 399"  # scripted group (container) (typed FeaturePython)
  n = 3
  ref = H_element
FEATURE [App::DocumentObjectGroupPython] N_element308  label="N_element : 166"  # scripted group (container) (typed FeaturePython)
  n = 1
  ref = N_element
FEATURE [App::DocumentObjectGroupPython] G4_POLYACRYLONITRILE  # scripted group (container) (typed FeaturePython)
  Dunit = g/cm3
  Dvalue = 1.17
  Group = -> [C_element670,H_element624,N_element308]
  conduct = 2
  density = 1
  expand = 3
  formula = G4_POLYACRYLONITRILE
  name = G4_POLYACRYLONITRILE
  specific = 4
FEATURE [App::DocumentObjectGroupPython] C_element671  label="C_element : 435"  # scripted group (container) (typed FeaturePython)
  n = 16
  ref = C_element
FEATURE [App::DocumentObjectGroupPython] H_element625  label="H_element : 400"  # scripted group (container) (typed FeaturePython)
  n = 14
  ref = H_element
FEATURE [App::DocumentObjectGroupPython] O_element597  label="O_element : 376"  # scripted group (container) (typed FeaturePython)
  n = 3
  ref = O_element
FEATURE [App::DocumentObjectGroupPython] G4_POLYCARBONATE  # scripted group (container) (typed FeaturePython)
  Dunit = g/cm3
  Dvalue = 1.2
  Group = -> [C_element671,H_element625,O_element597]
  conduct = 2
  density = 1
  expand = 3
  formula = G4_POLYCARBONATE
  name = G4_POLYCARBONATE
  specific = 4
FEATURE [App::DocumentObjectGroupPython] C_element672  label="C_element : 436"  # scripted group (container) (typed FeaturePython)
  n = 8
  ref = C_element
FEATURE [App::DocumentObjectGroupPython] H_element626  label="H_element : 401"  # scripted group (container) (typed FeaturePython)
  n = 7
  ref = H_element
FEATURE [App::DocumentObjectGroupPython] Cl_element137  label="Cl_element : 067"  # scripted group (container) (typed FeaturePython)
  n = 1
  ref = Cl_element
FEATURE [App::DocumentObjectGroupPython] G4_POLYCHLOROSTYRENE  # scripted group (container) (typed FeaturePython)
  Dunit = g/cm3
  Dvalue = 1.3
  Group = -> [C_element672,H_element626,Cl_element137]
  conduct = 2
  density = 1
  expand = 3
  formula = G4_POLYCHLOROSTYRENE
  name = G4_POLYCHLOROSTYRENE
  specific = 4
FEATURE [App::DocumentObjectGroupPython] C_element673  label="C_element : 437"  # scripted group (container) (typed FeaturePython)
  n = 1
  ref = C_element
FEATURE [App::DocumentObjectGroupPython] H_element627  label="H_element : 402"  # scripted group (container) (typed FeaturePython)
  n = 2
  ref = H_element
FEATURE [App::DocumentObjectGroupPython] G4_POLYETHYLENE  # scripted group (container) (typed FeaturePython)
  Dunit = g/cm3
  Dvalue = 0.94
  Group = -> [C_element673,H_element627]
  conduct = 2
  density = 1
  expand = 3
  formula = G4_POLYETHYLENE
  name = G4_POLYETHYLENE
  specific = 4
FEATURE [App::DocumentObjectGroupPython] C_element674  label="C_element : 438"  # scripted group (container) (typed FeaturePython)
  n = 10
  ref = C_element
FEATURE [App::DocumentObjectGroupPython] H_element628  label="H_element : 403"  # scripted group (container) (typed FeaturePython)
  n = 8
  ref = H_element
FEATURE [App::DocumentObjectGroupPython] O_element598  label="O_element : 377"  # scripted group (container) (typed FeaturePython)
  n = 4
  ref = O_element
FEATURE [App::DocumentObjectGroupPython] G4_MYLAR  # scripted group (container) (typed FeaturePython)
  Dunit = g/cm3
  Dvalue = 1.4
  Group = -> [C_element674,H_element628,O_element598]
  conduct = 2
  density = 1
  expand = 3
  formula = G4_MYLAR
  name = G4_MYLAR
  specific = 4
FEATURE [App::DocumentObjectGroupPython] C_element675  label="C_element : 439"  # scripted group (container) (typed FeaturePython)
  n = 5
  ref = C_element
FEATURE [App::DocumentObjectGroupPython] H_element629  label="H_element : 404"  # scripted group (container) (typed FeaturePython)
  n = 8
  ref = H_element
FEATURE [App::DocumentObjectGroupPython] O_element599  label="O_element : 378"  # scripted group (container) (typed FeaturePython)
  n = 2
  ref = O_element
FEATURE [App::DocumentObjectGroupPython] G4_PLEXIGLASS  # scripted group (container) (typed FeaturePython)
  Dunit = g/cm3
  Dvalue = 1.19
  Group = -> [C_element675,H_element629,O_element599]
  conduct = 2
  density = 1
  expand = 3
  formula = G4_PLEXIGLASS
  name = G4_PLEXIGLASS
  specific = 4
FEATURE [App::DocumentObjectGroupPython] C_element676  label="C_element : 440"  # scripted group (container) (typed FeaturePython)
  n = 1
  ref = C_element
FEATURE [App::DocumentObjectGroupPython] H_element630  label="H_element : 405"  # scripted group (container) (typed FeaturePython)
  n = 2
  ref = H_element
FEATURE [App::DocumentObjectGroupPython] O_element600  label="O_element : 379"  # scripted group (container) (typed FeaturePython)
  n = 1
  ref = O_element
FEATURE [App::DocumentObjectGroupPython] G4_POLYOXYMETHYLENE  # scripted group (container) (typed FeaturePython)
  Dunit = g/cm3
  Dvalue = 1.425
  Group = -> [C_element676,H_element630,O_element600]
  conduct = 2
  density = 1
  expand = 3
  formula = G4_POLYOXYMETHYLENE
  name = G4_POLYOXYMETHYLENE
  specific = 4
FEATURE [App::DocumentObjectGroupPython] C_element677  label="C_element : 441"  # scripted group (container) (typed FeaturePython)
  n = 2
  ref = C_element
FEATURE [App::DocumentObjectGroupPython] H_element631  label="H_element : 406"  # scripted group (container) (typed FeaturePython)
  n = 4
  ref = H_element
FEATURE [App::DocumentObjectGroupPython] G4_POLYPROPYLENE  # scripted group (container) (typed FeaturePython)
  Dunit = g/cm3
  Dvalue = 0.9
  Group = -> [C_element677,H_element631]
  conduct = 2
  density = 1
  expand = 3
  formula = G4_POLYPROPYLENE
  name = G4_POLYPROPYLENE
  specific = 4
FEATURE [App::DocumentObjectGroupPython] C_element678  label="C_element : 442"  # scripted group (container) (typed FeaturePython)
  n = 8
  ref = C_element
FEATURE [App::DocumentObjectGroupPython] H_element632  label="H_element : 407"  # scripted group (container) (typed FeaturePython)
  n = 8
  ref = H_element
FEATURE [App::DocumentObjectGroupPython] G4_POLYSTYRENE  # scripted group (container) (typed FeaturePython)
  Dunit = g/cm3
  Dvalue = 1.06
  Group = -> [C_element678,H_element632]
  conduct = 2
  density = 1
  expand = 3
  formula = G4_POLYSTYRENE
  name = G4_POLYSTYRENE
  specific = 4
FEATURE [App::DocumentObjectGroupPython] C_element679  label="C_element : 443"  # scripted group (container) (typed FeaturePython)
  n = 2
  ref = C_element
FEATURE [App::DocumentObjectGroupPython] F_element090  label="F_element : 043"  # scripted group (container) (typed FeaturePython)
  n = 4
  ref = F_element
FEATURE [App::DocumentObjectGroupPython] G4_TEFLON  # scripted group (container) (typed FeaturePython)
  Dunit = g/cm3
  Dvalue = 2.2
  Group = -> [C_element679,F_element090]
  conduct = 2
  density = 1
  expand = 3
  formula = G4_TEFLON
  name = G4_TEFLON
  specific = 4
FEATURE [App::DocumentObjectGroupPython] C_element680  label="C_element : 444"  # scripted group (container) (typed FeaturePython)
  n = 2
  ref = C_element
FEATURE [App::DocumentObjectGroupPython] F_element091  label="F_element : 044"  # scripted group (container) (typed FeaturePython)
  n = 3
  ref = F_element
FEATURE [App::DocumentObjectGroupPython] Cl_element138  label="Cl_element : 068"  # scripted group (container) (typed FeaturePython)
  n = 1
  ref = Cl_element
FEATURE [App::DocumentObjectGroupPython] G4_POLYTRIFLUOROCHLOROETHYLENE  # scripted group (container) (typed FeaturePython)
  Dunit = g/cm3
  Dvalue = 2.1
  Group = -> [C_element680,F_element091,Cl_element138]
  conduct = 2
  density = 1
  expand = 3
  formula = G4_POLYTRIFLUOROCHLOROETHYLENE
  name = G4_POLYTRIFLUOROCHLOROETHYLENE
  specific = 4
FEATURE [App::DocumentObjectGroupPython] C_element681  label="C_element : 445"  # scripted group (container) (typed FeaturePython)
  n = 4
  ref = C_element
FEATURE [App::DocumentObjectGroupPython] H_element633  label="H_element : 408"  # scripted group (container) (typed FeaturePython)
  n = 6
  ref = H_element
FEATURE [App::DocumentObjectGroupPython] O_element601  label="O_element : 380"  # scripted group (container) (typed FeaturePython)
  n = 2
  ref = O_element
FEATURE [App::DocumentObjectGroupPython] G4_POLYVINYL_ACETATE  # scripted group (container) (typed FeaturePython)
  Dunit = g/cm3
  Dvalue = 1.19
  Group = -> [C_element681,H_element633,O_element601]
  conduct = 2
  density = 1
  expand = 3
  formula = G4_POLYVINYL_ACETATE
  name = G4_POLYVINYL_ACETATE
  specific = 4
FEATURE [App::DocumentObjectGroupPython] C_element682  label="C_element : 446"  # scripted group (container) (typed FeaturePython)
  n = 2
  ref = C_element
FEATURE [App::DocumentObjectGroupPython] H_element634  label="H_element : 409"  # scripted group (container) (typed FeaturePython)
  n = 4
  ref = H_element
FEATURE [App::DocumentObjectGroupPython] O_element602  label="O_element : 381"  # scripted group (container) (typed FeaturePython)
  n = 1
  ref = O_element
FEATURE [App::DocumentObjectGroupPython] G4_POLYVINYL_ALCOHOL  # scripted group (container) (typed FeaturePython)
  Dunit = g/cm3
  Dvalue = 1.3
  Group = -> [C_element682,H_element634,O_element602]
  conduct = 2
  density = 1
  expand = 3
  formula = G4_POLYVINYL_ALCOHOL
  name = G4_POLYVINYL_ALCOHOL
  specific = 4
FEATURE [App::DocumentObjectGroupPython] C_element683  label="C_element : 447"  # scripted group (container) (typed FeaturePython)
  n = 8
  ref = C_element
FEATURE [App::DocumentObjectGroupPython] H_element635  label="H_element : 410"  # scripted group (container) (typed FeaturePython)
  n = 14
  ref = H_element
FEATURE [App::DocumentObjectGroupPython] O_element603  label="O_element : 382"  # scripted group (container) (typed FeaturePython)
  n = 2
  ref = O_element
FEATURE [App::DocumentObjectGroupPython] G4_POLYVINYL_BUTYRAL  # scripted group (container) (typed FeaturePython)
  Dunit = g/cm3
  Dvalue = 1.12
  Group = -> [C_element683,H_element635,O_element603]
  conduct = 2
  density = 1
  expand = 3
  formula = G4_POLYVINYL_BUTYRAL
  name = G4_POLYVINYL_BUTYRAL
  specific = 4
FEATURE [App::DocumentObjectGroupPython] C_element684  label="C_element : 448"  # scripted group (container) (typed FeaturePython)
  n = 2
  ref = C_element
FEATURE [App::DocumentObjectGroupPython] H_element636  label="H_element : 411"  # scripted group (container) (typed FeaturePython)
  n = 3
  ref = H_element
FEATURE [App::DocumentObjectGroupPython] Cl_element139  label="Cl_element : 069"  # scripted group (container) (typed FeaturePython)
  n = 1
  ref = Cl_element
FEATURE [App::DocumentObjectGroupPython] G4_POLYVINYL_CHLORIDE  # scripted group (container) (typed FeaturePython)
  Dunit = g/cm3
  Dvalue = 1.3
  Group = -> [C_element684,H_element636,Cl_element139]
  conduct = 2
  density = 1
  expand = 3
  formula = G4_POLYVINYL_CHLORIDE
  name = G4_POLYVINYL_CHLORIDE
  specific = 4
FEATURE [App::DocumentObjectGroupPython] C_element685  label="C_element : 449"  # scripted group (container) (typed FeaturePython)
  n = 2
  ref = C_element
FEATURE [App::DocumentObjectGroupPython] H_element637  label="H_element : 412"  # scripted group (container) (typed FeaturePython)
  n = 2
  ref = H_element
FEATURE [App::DocumentObjectGroupPython] Cl_element140  label="Cl_element : 070"  # scripted group (container) (typed FeaturePython)
  n = 2
  ref = Cl_element
FEATURE [App::DocumentObjectGroupPython] G4_POLYVINYLIDENE_CHLORIDE  # scripted group (container) (typed FeaturePython)
  Dunit = g/cm3
  Dvalue = 1.7
  Group = -> [C_element685,H_element637,Cl_element140]
  conduct = 2
  density = 1
  expand = 3
  formula = G4_POLYVINYLIDENE_CHLORIDE
  name = G4_POLYVINYLIDENE_CHLORIDE
  specific = 4
FEATURE [App::DocumentObjectGroupPython] C_element686  label="C_element : 450"  # scripted group (container) (typed FeaturePython)
  n = 2
  ref = C_element
FEATURE [App::DocumentObjectGroupPython] H_element638  label="H_element : 413"  # scripted group (container) (typed FeaturePython)
  n = 2
  ref = H_element
FEATURE [App::DocumentObjectGroupPython] F_element092  label="F_element : 045"  # scripted group (container) (typed FeaturePython)
  n = 2
  ref = F_element
FEATURE [App::DocumentObjectGroupPython] G4_POLYVINYLIDENE_FLUORIDE  # scripted group (container) (typed FeaturePython)
  Dunit = g/cm3
  Dvalue = 1.76
  Group = -> [C_element686,H_element638,F_element092]
  conduct = 2
  density = 1
  expand = 3
  formula = G4_POLYVINYLIDENE_FLUORIDE
  name = G4_POLYVINYLIDENE_FLUORIDE
  specific = 4
FEATURE [App::DocumentObjectGroupPython] C_element687  label="C_element : 451"  # scripted group (container) (typed FeaturePython)
  n = 6
  ref = C_element
FEATURE [App::DocumentObjectGroupPython] H_element639  label="H_element : 414"  # scripted group (container) (typed FeaturePython)
  n = 9
  ref = H_element
FEATURE [App::DocumentObjectGroupPython] N_element309  label="N_element : 167"  # scripted group (container) (typed FeaturePython)
  n = 1
  ref = N_element
FEATURE [App::DocumentObjectGroupPython] O_element604  label="O_element : 383"  # scripted group (container) (typed FeaturePython)
  n = 1
  ref = O_element
FEATURE [App::DocumentObjectGroupPython] G4_POLYVINYL_PYRROLIDONE  # scripted group (container) (typed FeaturePython)
  Dunit = g/cm3
  Dvalue = 1.25
  Group = -> [C_element687,H_element639,N_element309,O_element604]
  conduct = 2
  density = 1
  expand = 3
  formula = G4_POLYVINYL_PYRROLIDONE
  name = G4_POLYVINYL_PYRROLIDONE
  specific = 4
FEATURE [App::DocumentObjectGroupPython] K_element060  label="K_element : 011"  # scripted group (container) (typed FeaturePython)
  n = 1
  ref = K_element
FEATURE [App::DocumentObjectGroupPython] I_element046  label="I_element : 029"  # scripted group (container) (typed FeaturePython)
  n = 1
  ref = I_element
FEATURE [App::DocumentObjectGroupPython] G4_POTASSIUM_IODIDE  # scripted group (container) (typed FeaturePython)
  Dunit = g/cm3
  Dvalue = 3.13
  Group = -> [K_element060,I_element046]
  conduct = 2
  density = 1
  expand = 3
  formula = G4_POTASSIUM_IODIDE
  name = G4_POTASSIUM_IODIDE
  specific = 4
FEATURE [App::DocumentObjectGroupPython] K_element061  label="K_element : 012"  # scripted group (container) (typed FeaturePython)
  n = 2
  ref = K_element
FEATURE [App::DocumentObjectGroupPython] O_element605  label="O_element : 384"  # scripted group (container) (typed FeaturePython)
  n = 1
  ref = O_element
FEATURE [App::DocumentObjectGroupPython] G4_POTASSIUM_OXIDE  # scripted group (container) (typed FeaturePython)
  Dunit = g/cm3
  Dvalue = 2.32
  Group = -> [K_element061,O_element605]
  conduct = 2
  density = 1
  expand = 3
  formula = G4_POTASSIUM_OXIDE
  name = G4_POTASSIUM_OXIDE
  specific = 4
FEATURE [App::DocumentObjectGroupPython] C_element688  label="C_element : 452"  # scripted group (container) (typed FeaturePython)
  n = 3
  ref = C_element
FEATURE [App::DocumentObjectGroupPython] H_element640  label="H_element : 415"  # scripted group (container) (typed FeaturePython)
  n = 8
  ref = H_element
FEATURE [App::DocumentObjectGroupPython] G4_PROPANE  # scripted group (container) (typed FeaturePython)
  Dunit = g/cm3
  Dvalue = 0.00187939
  Group = -> [C_element688,H_element640]
  conduct = 2
  density = 1
  expand = 3
  formula = G4_PROPANE
  name = G4_PROPANE
  specific = 4
FEATURE [App::DocumentObjectGroupPython] C_element689  label="C_element : 453"  # scripted group (container) (typed FeaturePython)
  n = 3
  ref = C_element
FEATURE [App::DocumentObjectGroupPython] H_element641  label="H_element : 416"  # scripted group (container) (typed FeaturePython)
  n = 8
  ref = H_element
FEATURE [App::DocumentObjectGroupPython] G4_lPROPANE  # scripted group (container) (typed FeaturePython)
  Dunit = g/cm3
  Dvalue = 0.43
  Group = -> [C_element689,H_element641]
  conduct = 2
  density = 1
  expand = 3
  formula = G4_lPROPANE
  name = G4_lPROPANE
  specific = 4
FEATURE [App::DocumentObjectGroupPython] C_element690  label="C_element : 454"  # scripted group (container) (typed FeaturePython)
  n = 3
  ref = C_element
FEATURE [App::DocumentObjectGroupPython] H_element642  label="H_element : 417"  # scripted group (container) (typed FeaturePython)
  n = 8
  ref = H_element
FEATURE [App::DocumentObjectGroupPython] O_element606  label="O_element : 385"  # scripted group (container) (typed FeaturePython)
  n = 1
  ref = O_element
FEATURE [App::DocumentObjectGroupPython] G4_N_PROPYL_ALCOHOL  label="G4_N-PROPYL_ALCOHOL"  # scripted group (container) (typed FeaturePython)
  Dunit = g/cm3
  Dvalue = 0.8035
  Group = -> [C_element690,H_element642,O_element606]
  conduct = 2
  density = 1
  expand = 3
  formula = G4_N-PROPYL_ALCOHOL
  name = G4_N-PROPYL_ALCOHOL
  specific = 4
FEATURE [App::DocumentObjectGroupPython] C_element691  label="C_element : 455"  # scripted group (container) (typed FeaturePython)
  n = 5
  ref = C_element
FEATURE [App::DocumentObjectGroupPython] H_element643  label="H_element : 418"  # scripted group (container) (typed FeaturePython)
  n = 5
  ref = H_element
FEATURE [App::DocumentObjectGroupPython] N_element310  label="N_element : 168"  # scripted group (container) (typed FeaturePython)
  n = 1
  ref = N_element
FEATURE [App::DocumentObjectGroupPython] G4_PYRIDINE  # scripted group (container) (typed FeaturePython)
  Dunit = g/cm3
  Dvalue = 0.9819
  Group = -> [C_element691,H_element643,N_element310]
  conduct = 2
  density = 1
  expand = 3
  formula = G4_PYRIDINE
  name = G4_PYRIDINE
  specific = 4
FEATURE [App::DocumentObjectGroupPython] H_element644  label="H_element : 0.276"  # scripted group (container) (typed FeaturePython)
  n = 0.143711
FEATURE [App::DocumentObjectGroupPython] C_element692  label="C_element : 0.1007"  # scripted group (container) (typed FeaturePython)
  n = 0.856289
FEATURE [App::DocumentObjectGroupPython] G4_RUBBER_BUTYL  # scripted group (container) (typed FeaturePython)
  Dunit = g/cm3
  Dvalue = 0.92
  Group = -> [H_element644,C_element692]
  conduct = 2
  density = 1
  expand = 3
  formula = G4_RUBBER_BUTYL
  name = G4_RUBBER_BUTYL
  specific = 4
FEATURE [App::DocumentObjectGroupPython] H_element645  label="H_element : 0.277"  # scripted group (container) (typed FeaturePython)
  n = 0.118371
FEATURE [App::DocumentObjectGroupPython] C_element693  label="C_element : 0.1008"  # scripted group (container) (typed FeaturePython)
  n = 0.881629
FEATURE [App::DocumentObjectGroupPython] G4_RUBBER_NATURAL  # scripted group (container) (typed FeaturePython)
  Dunit = g/cm3
  Dvalue = 0.92
  Group = -> [H_element645,C_element693]
  conduct = 2
  density = 1
  expand = 3
  formula = G4_RUBBER_NATURAL
  name = G4_RUBBER_NATURAL
  specific = 4
FEATURE [App::DocumentObjectGroupPython] H_element646  label="H_element : 0.278"  # scripted group (container) (typed FeaturePython)
  n = 0.05692
FEATURE [App::DocumentObjectGroupPython] C_element694  label="C_element : 0.1009"  # scripted group (container) (typed FeaturePython)
  n = 0.542646
FEATURE [App::DocumentObjectGroupPython] Cl_element141  label="Cl_element : 0.637"  # scripted group (container) (typed FeaturePython)
  n = 0.400434
FEATURE [App::DocumentObjectGroupPython] G4_RUBBER_NEOPRENE  # scripted group (container) (typed FeaturePython)
  Dunit = g/cm3
  Dvalue = 1.23
  Group = -> [H_element646,C_element694,Cl_element141]
  conduct = 2
  density = 1
  expand = 3
  formula = G4_RUBBER_NEOPRENE
  name = G4_RUBBER_NEOPRENE
  specific = 4
FEATURE [App::DocumentObjectGroupPython] Si_element034  label="Si_element : 008"  # scripted group (container) (typed FeaturePython)
  n = 1
  ref = Si_element
FEATURE [App::DocumentObjectGroupPython] O_element607  label="O_element : 386"  # scripted group (container) (typed FeaturePython)
  n = 2
  ref = O_element
FEATURE [App::DocumentObjectGroupPython] G4_SILICON_DIOXIDE  # scripted group (container) (typed FeaturePython)
  Dunit = g/cm3
  Dvalue = 2.32
  Group = -> [Si_element034,O_element607]
  conduct = 2
  density = 1
  expand = 3
  formula = G4_SILICON_DIOXIDE
  name = G4_SILICON_DIOXIDE
  specific = 4
FEATURE [App::DocumentObjectGroupPython] Ag_element026  label="Ag_element : 016"  # scripted group (container) (typed FeaturePython)
  n = 1
  ref = Ag_element
FEATURE [App::DocumentObjectGroupPython] Br_element033  label="Br_element : 018"  # scripted group (container) (typed FeaturePython)
  n = 1
  ref = Br_element
FEATURE [App::DocumentObjectGroupPython] G4_SILVER_BROMIDE  # scripted group (container) (typed FeaturePython)
  Dunit = g/cm3
  Dvalue = 6.473
  Group = -> [Ag_element026,Br_element033]
  conduct = 2
  density = 1
  expand = 3
  formula = G4_SILVER_BROMIDE
  name = G4_SILVER_BROMIDE
  specific = 4
FEATURE [App::DocumentObjectGroupPython] Ag_element027  label="Ag_element : 017"  # scripted group (container) (typed FeaturePython)
  n = 1
  ref = Ag_element
FEATURE [App::DocumentObjectGroupPython] Cl_element142  label="Cl_element : 071"  # scripted group (container) (typed FeaturePython)
  n = 1
  ref = Cl_element
FEATURE [App::DocumentObjectGroupPython] G4_SILVER_CHLORIDE  # scripted group (container) (typed FeaturePython)
  Dunit = g/cm3
  Dvalue = 5.56
  Group = -> [Ag_element027,Cl_element142]
  conduct = 2
  density = 1
  expand = 3
  formula = G4_SILVER_CHLORIDE
  name = G4_SILVER_CHLORIDE
  specific = 4
FEATURE [App::DocumentObjectGroupPython] Br_element034  label="Br_element : 0.771"  # scripted group (container) (typed FeaturePython)
  n = 0.422895
FEATURE [App::DocumentObjectGroupPython] Ag_element028  label="Ag_element : 0.580"  # scripted group (container) (typed FeaturePython)
  n = 0.573748
FEATURE [App::DocumentObjectGroupPython] I_element047  label="I_element : 0.659"  # scripted group (container) (typed FeaturePython)
  n = 0.003357
FEATURE [App::DocumentObjectGroupPython] G4_SILVER_HALIDES  # scripted group (container) (typed FeaturePython)
  Dunit = g/cm3
  Dvalue = 6.47
  Group = -> [Br_element034,Ag_element028,I_element047]
  conduct = 2
  density = 1
  expand = 3
  formula = G4_SILVER_HALIDES
  name = G4_SILVER_HALIDES
  specific = 4
FEATURE [App::DocumentObjectGroupPython] Ag_element029  label="Ag_element : 018"  # scripted group (container) (typed FeaturePython)
  n = 1
  ref = Ag_element
FEATURE [App::DocumentObjectGroupPython] I_element048  label="I_element : 030"  # scripted group (container) (typed FeaturePython)
  n = 1
  ref = I_element
FEATURE [App::DocumentObjectGroupPython] G4_SILVER_IODIDE  # scripted group (container) (typed FeaturePython)
  Dunit = g/cm3
  Dvalue = 6.01
  Group = -> [Ag_element029,I_element048]
  conduct = 2
  density = 1
  expand = 3
  formula = G4_SILVER_IODIDE
  name = G4_SILVER_IODIDE
  specific = 4
FEATURE [App::DocumentObjectGroupPython] H_element647  label="H_element : 0.279"  # scripted group (container) (typed FeaturePython)
  n = 0.1
FEATURE [App::DocumentObjectGroupPython] C_element695  label="C_element : 0.1010"  # scripted group (container) (typed FeaturePython)
  n = 0.204
FEATURE [App::DocumentObjectGroupPython] N_element311  label="N_element : 0.851"  # scripted group (container) (typed FeaturePython)
  n = 0.042
FEATURE [App::DocumentObjectGroupPython] O_element608  label="O_element : 0.1001"  # scripted group (container) (typed FeaturePython)
  n = 0.645
FEATURE [App::DocumentObjectGroupPython] Na_element093  label="Na_element : 0.154"  # scripted group (container) (typed FeaturePython)
  n = 0.002
FEATURE [App::DocumentObjectGroupPython] P_element085  label="P_element : 0.146"  # scripted group (container) (typed FeaturePython)
  n = 0.001
FEATURE [App::DocumentObjectGroupPython] S_element112  label="S_element : 0.078"  # scripted group (container) (typed FeaturePython)
  n = 0.002
FEATURE [App::DocumentObjectGroupPython] Cl_element143  label="Cl_element : 0.638"  # scripted group (container) (typed FeaturePython)
  n = 0.003
FEATURE [App::DocumentObjectGroupPython] K_element062  label="K_element : 0.051"  # scripted group (container) (typed FeaturePython)
  n = 0.001
FEATURE [App::DocumentObjectGroupPython] G4_SKIN_ICRP  # scripted group (container) (typed FeaturePython)
  Dunit = g/cm3
  Dvalue = 1.09
  Group = -> [H_element647,C_element695,N_element311,O_element608,Na_element093,P_element085,S_element112,Cl_element143,K_element062]
  conduct = 2
  density = 1
  expand = 3
  formula = G4_SKIN_ICRP
  name = G4_SKIN_ICRP
  specific = 4
FEATURE [App::DocumentObjectGroupPython] Na_element094  label="Na_element : 019"  # scripted group (container) (typed FeaturePython)
  n = 2
  ref = Na_element
FEATURE [App::DocumentObjectGroupPython] C_element696  label="C_element : 456"  # scripted group (container) (typed FeaturePython)
  n = 1
  ref = C_element
FEATURE [App::DocumentObjectGroupPython] O_element609  label="O_element : 387"  # scripted group (container) (typed FeaturePython)
  n = 3
  ref = O_element
FEATURE [App::DocumentObjectGroupPython] G4_SODIUM_CARBONATE  # scripted group (container) (typed FeaturePython)
  Dunit = g/cm3
  Dvalue = 2.532
  Group = -> [Na_element094,C_element696,O_element609]
  conduct = 2
  density = 1
  expand = 3
  formula = G4_SODIUM_CARBONATE
  name = G4_SODIUM_CARBONATE
  specific = 4
FEATURE [App::DocumentObjectGroupPython] Na_element095  label="Na_element : 020"  # scripted group (container) (typed FeaturePython)
  n = 1
  ref = Na_element
FEATURE [App::DocumentObjectGroupPython] I_element049  label="I_element : 031"  # scripted group (container) (typed FeaturePython)
  n = 1
  ref = I_element
FEATURE [App::DocumentObjectGroupPython] G4_SODIUM_IODIDE  # scripted group (container) (typed FeaturePython)
  Dunit = g/cm3
  Dvalue = 3.667
  Group = -> [Na_element095,I_element049]
  conduct = 2
  density = 1
  expand = 3
  formula = G4_SODIUM_IODIDE
  name = G4_SODIUM_IODIDE
  specific = 4
FEATURE [App::DocumentObjectGroupPython] Na_element096  label="Na_element : 021"  # scripted group (container) (typed FeaturePython)
  n = 2
  ref = Na_element
FEATURE [App::DocumentObjectGroupPython] O_element610  label="O_element : 388"  # scripted group (container) (typed FeaturePython)
  n = 1
  ref = O_element
FEATURE [App::DocumentObjectGroupPython] G4_SODIUM_MONOXIDE  # scripted group (container) (typed FeaturePython)
  Dunit = g/cm3
  Dvalue = 2.27
  Group = -> [Na_element096,O_element610]
  conduct = 2
  density = 1
  expand = 3
  formula = G4_SODIUM_MONOXIDE
  name = G4_SODIUM_MONOXIDE
  specific = 4
FEATURE [App::DocumentObjectGroupPython] Na_element097  label="Na_element : 022"  # scripted group (container) (typed FeaturePython)
  n = 1
  ref = Na_element
FEATURE [App::DocumentObjectGroupPython] N_element312  label="N_element : 169"  # scripted group (container) (typed FeaturePython)
  n = 1
  ref = N_element
FEATURE [App::DocumentObjectGroupPython] O_element611  label="O_element : 389"  # scripted group (container) (typed FeaturePython)
  n = 3
  ref = O_element
FEATURE [App::DocumentObjectGroupPython] G4_SODIUM_NITRATE  # scripted group (container) (typed FeaturePython)
  Dunit = g/cm3
  Dvalue = 2.261
  Group = -> [Na_element097,N_element312,O_element611]
  conduct = 2
  density = 1
  expand = 3
  formula = G4_SODIUM_NITRATE
  name = G4_SODIUM_NITRATE
  specific = 4
FEATURE [App::DocumentObjectGroupPython] C_element697  label="C_element : 457"  # scripted group (container) (typed FeaturePython)
  n = 14
  ref = C_element
FEATURE [App::DocumentObjectGroupPython] H_element648  label="H_element : 419"  # scripted group (container) (typed FeaturePython)
  n = 12
  ref = H_element
FEATURE [App::DocumentObjectGroupPython] G4_STILBENE  # scripted group (container) (typed FeaturePython)
  Dunit = g/cm3
  Dvalue = 0.9707
  Group = -> [C_element697,H_element648]
  conduct = 2
  density = 1
  expand = 3
  formula = G4_STILBENE
  name = G4_STILBENE
  specific = 4
FEATURE [App::DocumentObjectGroupPython] C_element698  label="C_element : 458"  # scripted group (container) (typed FeaturePython)
  n = 12
  ref = C_element
FEATURE [App::DocumentObjectGroupPython] H_element649  label="H_element : 420"  # scripted group (container) (typed FeaturePython)
  n = 22
  ref = H_element
FEATURE [App::DocumentObjectGroupPython] O_element612  label="O_element : 390"  # scripted group (container) (typed FeaturePython)
  n = 11
  ref = O_element
FEATURE [App::DocumentObjectGroupPython] G4_SUCROSE  # scripted group (container) (typed FeaturePython)
  Dunit = g/cm3
  Dvalue = 1.5805
  Group = -> [C_element698,H_element649,O_element612]
  conduct = 2
  density = 1
  expand = 3
  formula = G4_SUCROSE
  name = G4_SUCROSE
  specific = 4
FEATURE [App::DocumentObjectGroupPython] C_element699  label="C_element : 459"  # scripted group (container) (typed FeaturePython)
  n = 18
  ref = C_element
FEATURE [App::DocumentObjectGroupPython] H_element650  label="H_element : 421"  # scripted group (container) (typed FeaturePython)
  n = 14
  ref = H_element
FEATURE [App::DocumentObjectGroupPython] G4_TERPHENYL  # scripted group (container) (typed FeaturePython)
  Dunit = g/cm3
  Dvalue = 1.24
  Group = -> [C_element699,H_element650]
  conduct = 2
  density = 1
  expand = 3
  formula = G4_TERPHENYL
  name = G4_TERPHENYL
  specific = 4
FEATURE [App::DocumentObjectGroupPython] H_element651  label="H_element : 0.280"  # scripted group (container) (typed FeaturePython)
  n = 0.106
FEATURE [App::DocumentObjectGroupPython] C_element700  label="C_element : 0.1011"  # scripted group (container) (typed FeaturePython)
  n = 0.099
FEATURE [App::DocumentObjectGroupPython] N_element313  label="N_element : 0.852"  # scripted group (container) (typed FeaturePython)
  n = 0.02
FEATURE [App::DocumentObjectGroupPython] O_element613  label="O_element : 0.1002"  # scripted group (container) (typed FeaturePython)
  n = 0.766
FEATURE [App::DocumentObjectGroupPython] Na_element098  label="Na_element : 0.155"  # scripted group (container) (typed FeaturePython)
  n = 0.002
FEATURE [App::DocumentObjectGroupPython] P_element086  label="P_element : 0.147"  # scripted group (container) (typed FeaturePython)
  n = 0.001
FEATURE [App::DocumentObjectGroupPython] S_element113  label="S_element : 0.079"  # scripted group (container) (typed FeaturePython)
  n = 0.002
FEATURE [App::DocumentObjectGroupPython] Cl_element144  label="Cl_element : 0.639"  # scripted group (container) (typed FeaturePython)
  n = 0.002
FEATURE [App::DocumentObjectGroupPython] K_element063  label="K_element : 0.052"  # scripted group (container) (typed FeaturePython)
  n = 0.002
FEATURE [App::DocumentObjectGroupPython] G4_TESTIS_ICRP  # scripted group (container) (typed FeaturePython)
  Dunit = g/cm3
  Dvalue = 1.04
  Group = -> [H_element651,C_element700,N_element313,O_element613,Na_element098,P_element086,S_element113,Cl_element144,K_element063]
  conduct = 2
  density = 1
  expand = 3
  formula = G4_TESTIS_ICRP
  name = G4_TESTIS_ICRP
  specific = 4
FEATURE [App::DocumentObjectGroupPython] C_element701  label="C_element : 460"  # scripted group (container) (typed FeaturePython)
  n = 2
  ref = C_element
FEATURE [App::DocumentObjectGroupPython] Cl_element145  label="Cl_element : 072"  # scripted group (container) (typed FeaturePython)
  n = 4
  ref = Cl_element
FEATURE [App::DocumentObjectGroupPython] G4_TETRACHLOROETHYLENE  # scripted group (container) (typed FeaturePython)
  Dunit = g/cm3
  Dvalue = 1.625
  Group = -> [C_element701,Cl_element145]
  conduct = 2
  density = 1
  expand = 3
  formula = G4_TETRACHLOROETHYLENE
  name = G4_TETRACHLOROETHYLENE
  specific = 4
FEATURE [App::DocumentObjectGroupPython] Tl_element009  label="Tl_element : 008"  # scripted group (container) (typed FeaturePython)
  n = 1
  ref = Tl_element
FEATURE [App::DocumentObjectGroupPython] Cl_element146  label="Cl_element : 073"  # scripted group (container) (typed FeaturePython)
  n = 1
  ref = Cl_element
FEATURE [App::DocumentObjectGroupPython] G4_THALLIUM_CHLORIDE  # scripted group (container) (typed FeaturePython)
  Dunit = g/cm3
  Dvalue = 7.004
  Group = -> [Tl_element009,Cl_element146]
  conduct = 2
  density = 1
  expand = 3
  formula = G4_THALLIUM_CHLORIDE
  name = G4_THALLIUM_CHLORIDE
  specific = 4
FEATURE [App::DocumentObjectGroupPython] H_element652  label="H_element : 0.281"  # scripted group (container) (typed FeaturePython)
  n = 0.105
FEATURE [App::DocumentObjectGroupPython] C_element702  label="C_element : 0.1012"  # scripted group (container) (typed FeaturePython)
  n = 0.256
FEATURE [App::DocumentObjectGroupPython] N_element314  label="N_element : 0.853"  # scripted group (container) (typed FeaturePython)
  n = 0.027
FEATURE [App::DocumentObjectGroupPython] O_element614  label="O_element : 0.1003"  # scripted group (container) (typed FeaturePython)
  n = 0.602
FEATURE [App::DocumentObjectGroupPython] Na_element099  label="Na_element : 0.156"  # scripted group (container) (typed FeaturePython)
  n = 0.001
FEATURE [App::DocumentObjectGroupPython] P_element087  label="P_element : 0.148"  # scripted group (container) (typed FeaturePython)
  n = 0.002
FEATURE [App::DocumentObjectGroupPython] S_element114  label="S_element : 0.080"  # scripted group (container) (typed FeaturePython)
  n = 0.003
FEATURE [App::DocumentObjectGroupPython] Cl_element147  label="Cl_element : 0.640"  # scripted group (container) (typed FeaturePython)
  n = 0.002
FEATURE [App::DocumentObjectGroupPython] K_element064  label="K_element : 0.053"  # scripted group (container) (typed FeaturePython)
  n = 0.002
FEATURE [App::DocumentObjectGroupPython] G4_TISSUE_SOFT_ICRP  # scripted group (container) (typed FeaturePython)
  Dunit = g/cm3
  Dvalue = 1.03
  Group = -> [H_element652,C_element702,N_element314,O_element614,Na_element099,P_element087,S_element114,Cl_element147,K_element064]
  conduct = 2
  density = 1
  expand = 3
  formula = G4_TISSUE_SOFT_ICRP
  name = G4_TISSUE_SOFT_ICRP
  specific = 4
FEATURE [App::DocumentObjectGroupPython] H_element653  label="H_element : 0.282"  # scripted group (container) (typed FeaturePython)
  n = 0.101
FEATURE [App::DocumentObjectGroupPython] C_element703  label="C_element : 0.1013"  # scripted group (container) (typed FeaturePython)
  n = 0.111
FEATURE [App::DocumentObjectGroupPython] N_element315  label="N_element : 0.854"  # scripted group (container) (typed FeaturePython)
  n = 0.026
FEATURE [App::DocumentObjectGroupPython] O_element615  label="O_element : 0.1004"  # scripted group (container) (typed FeaturePython)
  n = 0.762
FEATURE [App::DocumentObjectGroupPython] G4_TISSUE_SOFT_ICRU_4  label="G4_TISSUE_SOFT_ICRU-4"  # scripted group (container) (typed FeaturePython)
  Dunit = g/cm3
  Dvalue = 1
  Group = -> [H_element653,C_element703,N_element315,O_element615]
  conduct = 2
  density = 1
  expand = 3
  formula = G4_TISSUE_SOFT_ICRU-4
  name = G4_TISSUE_SOFT_ICRU-4
  specific = 4
FEATURE [App::DocumentObjectGroupPython] H_element654  label="H_element : 0.283"  # scripted group (container) (typed FeaturePython)
  n = 0.101869
FEATURE [App::DocumentObjectGroupPython] C_element704  label="C_element : 0.1014"  # scripted group (container) (typed FeaturePython)
  n = 0.456179
FEATURE [App::DocumentObjectGroupPython] N_element316  label="N_element : 0.855"  # scripted group (container) (typed FeaturePython)
  n = 0.035172
FEATURE [App::DocumentObjectGroupPython] O_element616  label="O_element : 0.1005"  # scripted group (container) (typed FeaturePython)
  n = 0.40678
FEATURE [App::DocumentObjectGroupPython] G4_TISSUE_METHANE  label="G4_TISSUE-METHANE"  # scripted group (container) (typed FeaturePython)
  Dunit = g/cm3
  Dvalue = 0.00106409
  Group = -> [H_element654,C_element704,N_element316,O_element616]
  conduct = 2
  density = 1
  expand = 3
  formula = G4_TISSUE-METHANE
  name = G4_TISSUE-METHANE
  specific = 4
FEATURE [App::DocumentObjectGroupPython] H_element655  label="H_element : 0.284"  # scripted group (container) (typed FeaturePython)
  n = 0.102672
FEATURE [App::DocumentObjectGroupPython] C_element705  label="C_element : 0.1015"  # scripted group (container) (typed FeaturePython)
  n = 0.56894
FEATURE [App::DocumentObjectGroupPython] N_element317  label="N_element : 0.856"  # scripted group (container) (typed FeaturePython)
  n = 0.035022
FEATURE [App::DocumentObjectGroupPython] O_element617  label="O_element : 0.1006"  # scripted group (container) (typed FeaturePython)
  n = 0.293366
FEATURE [App::DocumentObjectGroupPython] G4_TISSUE_PROPANE  label="G4_TISSUE-PROPANE"  # scripted group (container) (typed FeaturePython)
  Dunit = g/cm3
  Dvalue = 0.00182628
  Group = -> [H_element655,C_element705,N_element317,O_element617]
  conduct = 2
  density = 1
  expand = 3
  formula = G4_TISSUE-PROPANE
  name = G4_TISSUE-PROPANE
  specific = 4
FEATURE [App::DocumentObjectGroupPython] Ti_element019  label="Ti_element : 008"  # scripted group (container) (typed FeaturePython)
  n = 1
  ref = Ti_element
FEATURE [App::DocumentObjectGroupPython] O_element618  label="O_element : 391"  # scripted group (container) (typed FeaturePython)
  n = 2
  ref = O_element
FEATURE [App::DocumentObjectGroupPython] G4_TITANIUM_DIOXIDE  # scripted group (container) (typed FeaturePython)
  Dunit = g/cm3
  Dvalue = 4.26
  Group = -> [Ti_element019,O_element618]
  conduct = 2
  density = 1
  expand = 3
  formula = G4_TITANIUM_DIOXIDE
  name = G4_TITANIUM_DIOXIDE
  specific = 4
FEATURE [App::DocumentObjectGroupPython] C_element706  label="C_element : 461"  # scripted group (container) (typed FeaturePython)
  n = 7
  ref = C_element
FEATURE [App::DocumentObjectGroupPython] H_element656  label="H_element : 422"  # scripted group (container) (typed FeaturePython)
  n = 8
  ref = H_element
FEATURE [App::DocumentObjectGroupPython] G4_TOLUENE  # scripted group (container) (typed FeaturePython)
  Dunit = g/cm3
  Dvalue = 0.8669
  Group = -> [C_element706,H_element656]
  conduct = 2
  density = 1
  expand = 3
  formula = G4_TOLUENE
  name = G4_TOLUENE
  specific = 4
FEATURE [App::DocumentObjectGroupPython] C_element707  label="C_element : 462"  # scripted group (container) (typed FeaturePython)
  n = 2
  ref = C_element
FEATURE [App::DocumentObjectGroupPython] H_element657  label="H_element : 423"  # scripted group (container) (typed FeaturePython)
  n = 1
  ref = H_element
FEATURE [App::DocumentObjectGroupPython] Cl_element148  label="Cl_element : 074"  # scripted group (container) (typed FeaturePython)
  n = 3
  ref = Cl_element
FEATURE [App::DocumentObjectGroupPython] G4_TRICHLOROETHYLENE  # scripted group (container) (typed FeaturePython)
  Dunit = g/cm3
  Dvalue = 1.46
  Group = -> [C_element707,H_element657,Cl_element148]
  conduct = 2
  density = 1
  expand = 3
  formula = G4_TRICHLOROETHYLENE
  name = G4_TRICHLOROETHYLENE
  specific = 4
FEATURE [App::DocumentObjectGroupPython] C_element708  label="C_element : 463"  # scripted group (container) (typed FeaturePython)
  n = 6
  ref = C_element
FEATURE [App::DocumentObjectGroupPython] H_element658  label="H_element : 424"  # scripted group (container) (typed FeaturePython)
  n = 15
  ref = H_element
FEATURE [App::DocumentObjectGroupPython] O_element619  label="O_element : 392"  # scripted group (container) (typed FeaturePython)
  n = 4
  ref = O_element
FEATURE [App::DocumentObjectGroupPython] P_element088  label="P_element : 032"  # scripted group (container) (typed FeaturePython)
  n = 1
  ref = P_element
FEATURE [App::DocumentObjectGroupPython] G4_TRIETHYL_PHOSPHATE  # scripted group (container) (typed FeaturePython)
  Dunit = g/cm3
  Dvalue = 1.07
  Group = -> [C_element708,H_element658,O_element619,P_element088]
  conduct = 2
  density = 1
  expand = 3
  formula = G4_TRIETHYL_PHOSPHATE
  name = G4_TRIETHYL_PHOSPHATE
  specific = 4
FEATURE [App::DocumentObjectGroupPython] W_element023  label="W_element : 022"  # scripted group (container) (typed FeaturePython)
  n = 1
  ref = W_element
FEATURE [App::DocumentObjectGroupPython] F_element093  label="F_element : 046"  # scripted group (container) (typed FeaturePython)
  n = 6
  ref = F_element
FEATURE [App::DocumentObjectGroupPython] G4_TUNGSTEN_HEXAFLUORIDE  # scripted group (container) (typed FeaturePython)
  Dunit = g/cm3
  Dvalue = 2.4
  Group = -> [W_element023,F_element093]
  conduct = 2
  density = 1
  expand = 3
  formula = G4_TUNGSTEN_HEXAFLUORIDE
  name = G4_TUNGSTEN_HEXAFLUORIDE
  specific = 4
FEATURE [App::DocumentObjectGroupPython] U_element017  label="U_element : 016"  # scripted group (container) (typed FeaturePython)
  n = 1
  ref = U_element
FEATURE [App::DocumentObjectGroupPython] C_element709  label="C_element : 464"  # scripted group (container) (typed FeaturePython)
  n = 2
  ref = C_element
FEATURE [App::DocumentObjectGroupPython] G4_URANIUM_DICARBIDE  # scripted group (container) (typed FeaturePython)
  Dunit = g/cm3
  Dvalue = 11.28
  Group = -> [U_element017,C_element709]
  conduct = 2
  density = 1
  expand = 3
  formula = G4_URANIUM_DICARBIDE
  name = G4_URANIUM_DICARBIDE
  specific = 4
FEATURE [App::DocumentObjectGroupPython] U_element018  label="U_element : 017"  # scripted group (container) (typed FeaturePython)
  n = 1
  ref = U_element
FEATURE [App::DocumentObjectGroupPython] C_element710  label="C_element : 465"  # scripted group (container) (typed FeaturePython)
  n = 1
  ref = C_element
FEATURE [App::DocumentObjectGroupPython] G4_URANIUM_MONOCARBIDE  # scripted group (container) (typed FeaturePython)
  Dunit = g/cm3
  Dvalue = 13.63
  Group = -> [U_element018,C_element710]
  conduct = 2
  density = 1
  expand = 3
  formula = G4_URANIUM_MONOCARBIDE
  name = G4_URANIUM_MONOCARBIDE
  specific = 4
FEATURE [App::DocumentObjectGroupPython] U_element019  label="U_element : 018"  # scripted group (container) (typed FeaturePython)
  n = 1
  ref = U_element
FEATURE [App::DocumentObjectGroupPython] O_element620  label="O_element : 393"  # scripted group (container) (typed FeaturePython)
  n = 2
  ref = O_element
FEATURE [App::DocumentObjectGroupPython] G4_URANIUM_OXIDE  # scripted group (container) (typed FeaturePython)
  Dunit = g/cm3
  Dvalue = 10.96
  Group = -> [U_element019,O_element620]
  conduct = 2
  density = 1
  expand = 3
  formula = G4_URANIUM_OXIDE
  name = G4_URANIUM_OXIDE
  specific = 4
FEATURE [App::DocumentObjectGroupPython] C_element711  label="C_element : 466"  # scripted group (container) (typed FeaturePython)
  n = 1
  ref = C_element
FEATURE [App::DocumentObjectGroupPython] H_element659  label="H_element : 425"  # scripted group (container) (typed FeaturePython)
  n = 4
  ref = H_element
FEATURE [App::DocumentObjectGroupPython] N_element318  label="N_element : 170"  # scripted group (container) (typed FeaturePython)
  n = 2
  ref = N_element
FEATURE [App::DocumentObjectGroupPython] O_element621  label="O_element : 394"  # scripted group (container) (typed FeaturePython)
  n = 1
  ref = O_element
FEATURE [App::DocumentObjectGroupPython] G4_UREA  # scripted group (container) (typed FeaturePython)
  Dunit = g/cm3
  Dvalue = 1.323
  Group = -> [C_element711,H_element659,N_element318,O_element621]
  conduct = 2
  density = 1
  expand = 3
  formula = G4_UREA
  name = G4_UREA
  specific = 4
FEATURE [App::DocumentObjectGroupPython] C_element712  label="C_element : 467"  # scripted group (container) (typed FeaturePython)
  n = 5
  ref = C_element
FEATURE [App::DocumentObjectGroupPython] H_element660  label="H_element : 426"  # scripted group (container) (typed FeaturePython)
  n = 11
  ref = H_element
FEATURE [App::DocumentObjectGroupPython] N_element319  label="N_element : 171"  # scripted group (container) (typed FeaturePython)
  n = 1
  ref = N_element
FEATURE [App::DocumentObjectGroupPython] O_element622  label="O_element : 395"  # scripted group (container) (typed FeaturePython)
  n = 2
  ref = O_element
FEATURE [App::DocumentObjectGroupPython] G4_VALINE  # scripted group (container) (typed FeaturePython)
  Dunit = g/cm3
  Dvalue = 1.23
  Group = -> [C_element712,H_element660,N_element319,O_element622]
  conduct = 2
  density = 1
  expand = 3
  formula = G4_VALINE
  name = G4_VALINE
  specific = 4
FEATURE [App::DocumentObjectGroupPython] H_element661  label="H_element : 0.285"  # scripted group (container) (typed FeaturePython)
  n = 0.009417
FEATURE [App::DocumentObjectGroupPython] C_element713  label="C_element : 0.1016"  # scripted group (container) (typed FeaturePython)
  n = 0.280555
FEATURE [App::DocumentObjectGroupPython] F_element094  label="F_element : 0.734"  # scripted group (container) (typed FeaturePython)
  n = 0.710028
FEATURE [App::DocumentObjectGroupPython] G4_VITON  # scripted group (container) (typed FeaturePython)
  Dunit = g/cm3
  Dvalue = 1.8
  Group = -> [H_element661,C_element713,F_element094]
  conduct = 2
  density = 1
  expand = 3
  formula = G4_VITON
  name = G4_VITON
  specific = 4
FEATURE [App::DocumentObjectGroupPython] H_element662  label="H_element : 427"  # scripted group (container) (typed FeaturePython)
  n = 2
  ref = H_element
FEATURE [App::DocumentObjectGroupPython] O_element623  label="O_element : 396"  # scripted group (container) (typed FeaturePython)
  n = 1
  ref = O_element
FEATURE [App::DocumentObjectGroupPython] G4_WATER  # scripted group (container) (typed FeaturePython)
  Dunit = g/cm3
  Dvalue = 1
  Group = -> [H_element662,O_element623]
  conduct = 2
  density = 1
  expand = 3
  formula = G4_WATER
  name = G4_WATER
  specific = 4
FEATURE [App::DocumentObjectGroupPython] H_element663  label="H_element : 428"  # scripted group (container) (typed FeaturePython)
  n = 2
  ref = H_element
FEATURE [App::DocumentObjectGroupPython] O_element624  label="O_element : 397"  # scripted group (container) (typed FeaturePython)
  n = 1
  ref = O_element
FEATURE [App::DocumentObjectGroupPython] G4_WATER_VAPOR  # scripted group (container) (typed FeaturePython)
  Dunit = g/cm3
  Dvalue = 0.000756182
  Group = -> [H_element663,O_element624]
  conduct = 2
  density = 1
  expand = 3
  formula = G4_WATER_VAPOR
  name = G4_WATER_VAPOR
  specific = 4
FEATURE [App::DocumentObjectGroupPython] C_element714  label="C_element : 468"  # scripted group (container) (typed FeaturePython)
  n = 8
  ref = C_element
FEATURE [App::DocumentObjectGroupPython] H_element664  label="H_element : 429"  # scripted group (container) (typed FeaturePython)
  n = 10
  ref = H_element
FEATURE [App::DocumentObjectGroupPython] G4_XYLENE  # scripted group (container) (typed FeaturePython)
  Dunit = g/cm3
  Dvalue = 0.87
  Group = -> [C_element714,H_element664]
  conduct = 2
  density = 1
  expand = 3
  formula = G4_XYLENE
  name = G4_XYLENE
  specific = 4
FEATURE [App::DocumentObjectGroupPython] C_element715  label="C_element : 469"  # scripted group (container) (typed FeaturePython)
  n = 1
  ref = C_element
FEATURE [App::DocumentObjectGroupPython] G4_GRAPHITE  # scripted group (container) (typed FeaturePython)
  Dunit = g/cm3
  Dvalue = 2.21
  Group = -> [C_element715]
  conduct = 2
  density = 1
  expand = 3
  formula = G4_GRAPHITE
  name = G4_GRAPHITE
  specific = 4
FEATURE [App::DocumentObjectGroupPython] NIST  # scripted group (container) (typed FeaturePython)
  Group = -> [G4_A_150_TISSUE,G4_ACETONE,G4_ACETYLENE,G4_ADENINE,G4_ADIPOSE_TISSUE_ICRP,G4_AIR,G4_ALANINE,G4_ALUMINUM_OXIDE,G4_AMBER,G4_AMMONIA,G4_ANILINE,G4_ANTHRACENE,G4_B_100_BONE,G4_BAKELITE,G4_BARIUM_FLUORIDE,G4_BARIUM_SULFATE,G4_BENZENE,G4_BERYLLIUM_OXIDE,G4_BGO,G4_BLOOD_ICRP,G4_BONE_COMPACT_ICRU,G4_BONE_CORTICAL_ICRP,G4_BORON_CARBIDE,G4_BORON_OXIDE,G4_BRAIN_ICRP,G4_BUTANE,G4_N_BUTYL_ALCOHOL,G4_C_552,+152 more]
FEATURE [App::DocumentObjectGroupPython] H_element665  label="H_element : 430"  # scripted group (container) (typed FeaturePython)
  n = 1
  ref = H_element
FEATURE [App::DocumentObjectGroupPython] G4_H  # scripted group (container) (typed FeaturePython)
  Dunit = g/cm3
  Dvalue = 8.3748e-05
  Group = -> [H_element665]
  conduct = 2
  density = 1
  expand = 3
  formula = H
  name = G4_H
  specific = 4
FEATURE [App::DocumentObjectGroupPython] He_element005  label="He_element : 004"  # scripted group (container) (typed FeaturePython)
  n = 1
  ref = He_element
FEATURE [App::DocumentObjectGroupPython] G4_He  # scripted group (container) (typed FeaturePython)
  Dunit = g/cm3
  Dvalue = 0.000166322
  Group = -> [He_element005]
  conduct = 2
  density = 1
  expand = 3
  formula = He
  name = G4_He
  specific = 4
FEATURE [App::DocumentObjectGroupPython] Li_element040  label="Li_element : 038"  # scripted group (container) (typed FeaturePython)
  n = 1
  ref = Li_element
FEATURE [App::DocumentObjectGroupPython] G4_Li  # scripted group (container) (typed FeaturePython)
  Dunit = g/cm3
  Dvalue = 0.534
  Group = -> [Li_element040]
  conduct = 2
  density = 1
  expand = 3
  formula = Li
  name = G4_Li
  specific = 4
FEATURE [App::DocumentObjectGroupPython] Be_element010  label="Be_element : 009"  # scripted group (container) (typed FeaturePython)
  n = 1
  ref = Be_element
FEATURE [App::DocumentObjectGroupPython] G4_Be  # scripted group (container) (typed FeaturePython)
  Dunit = g/cm3
  Dvalue = 1.848
  Group = -> [Be_element010]
  conduct = 2
  density = 1
  expand = 3
  formula = Be
  name = G4_Be
  specific = 4
FEATURE [App::DocumentObjectGroupPython] B_element035  label="B_element : 028"  # scripted group (container) (typed FeaturePython)
  n = 1
  ref = B_element
FEATURE [App::DocumentObjectGroupPython] G4_B  # scripted group (container) (typed FeaturePython)
  Dunit = g/cm3
  Dvalue = 2.37
  Group = -> [B_element035]
  conduct = 2
  density = 1
  expand = 3
  formula = B
  name = G4_B
  specific = 4
FEATURE [App::DocumentObjectGroupPython] C_element716  label="C_element : 470"  # scripted group (container) (typed FeaturePython)
  n = 1
  ref = C_element
FEATURE [App::DocumentObjectGroupPython] G4_C  # scripted group (container) (typed FeaturePython)
  Dunit = g/cm3
  Dvalue = 2
  Group = -> [C_element716]
  conduct = 2
  density = 1
  expand = 3
  formula = C
  name = G4_C
  specific = 4
FEATURE [App::DocumentObjectGroupPython] N_element320  label="N_element : 172"  # scripted group (container) (typed FeaturePython)
  n = 1
  ref = N_element
FEATURE [App::DocumentObjectGroupPython] G4_N  # scripted group (container) (typed FeaturePython)
  Dunit = g/cm3
  Dvalue = 0.0011652
  Group = -> [N_element320]
  conduct = 2
  density = 1
  expand = 3
  formula = N
  name = G4_N
  specific = 4
FEATURE [App::DocumentObjectGroupPython] O_element625  label="O_element : 398"  # scripted group (container) (typed FeaturePython)
  n = 1
  ref = O_element
FEATURE [App::DocumentObjectGroupPython] G4_O  # scripted group (container) (typed FeaturePython)
  Dunit = g/cm3
  Dvalue = 0.00133151
  Group = -> [O_element625]
  conduct = 2
  density = 1
  expand = 3
  formula = O
  name = G4_O
  specific = 4
FEATURE [App::DocumentObjectGroupPython] F_element095  label="F_element : 047"  # scripted group (container) (typed FeaturePython)
  n = 1
  ref = F_element
FEATURE [App::DocumentObjectGroupPython] G4_F  # scripted group (container) (typed FeaturePython)
  Dunit = g/cm3
  Dvalue = 0.00158029
  Group = -> [F_element095]
  conduct = 2
  density = 1
  expand = 3
  formula = F
  name = G4_F
  specific = 4
FEATURE [App::DocumentObjectGroupPython] Ne_element005  label="Ne_element : 004"  # scripted group (container) (typed FeaturePython)
  n = 1
  ref = Ne_element
FEATURE [App::DocumentObjectGroupPython] G4_Ne  # scripted group (container) (typed FeaturePython)
  Dunit = g/cm3
  Dvalue = 0.000838505
  Group = -> [Ne_element005]
  conduct = 2
  density = 1
  expand = 3
  formula = Ne
  name = G4_Ne
  specific = 4
FEATURE [App::DocumentObjectGroupPython] Na_element100  label="Na_element : 023"  # scripted group (container) (typed FeaturePython)
  n = 1
  ref = Na_element
FEATURE [App::DocumentObjectGroupPython] G4_Na  # scripted group (container) (typed FeaturePython)
  Dunit = g/cm3
  Dvalue = 0.971
  Group = -> [Na_element100]
  conduct = 2
  density = 1
  expand = 3
  formula = Na
  name = G4_Na
  specific = 4
FEATURE [App::DocumentObjectGroupPython] Mg_element055  label="Mg_element : 024"  # scripted group (container) (typed FeaturePython)
  n = 1
  ref = Mg_element
FEATURE [App::DocumentObjectGroupPython] G4_Mg  # scripted group (container) (typed FeaturePython)
  Dunit = g/cm3
  Dvalue = 1.74
  Group = -> [Mg_element055]
  conduct = 2
  density = 1
  expand = 3
  formula = Mg
  name = G4_Mg
  specific = 4
FEATURE [App::DocumentObjectGroupPython] Al_element020  label="Al_element : 008"  # scripted group (container) (typed FeaturePython)
  n = 1
  ref = Al_element
FEATURE [App::DocumentObjectGroupPython] G4_Al  # scripted group (container) (typed FeaturePython)
  Dunit = g/cm3
  Dvalue = 2.699
  Group = -> [Al_element020]
  conduct = 2
  density = 1
  expand = 3
  formula = Al
  name = G4_Al
  specific = 4
FEATURE [App::DocumentObjectGroupPython] Si_element035  label="Si_element : 009"  # scripted group (container) (typed FeaturePython)
  n = 1
  ref = Si_element
FEATURE [App::DocumentObjectGroupPython] G4_Si  # scripted group (container) (typed FeaturePython)
  Dunit = g/cm3
  Dvalue = 2.33
  Group = -> [Si_element035]
  conduct = 2
  density = 1
  expand = 3
  formula = Si
  name = G4_Si
  specific = 4
FEATURE [App::DocumentObjectGroupPython] P_element089  label="P_element : 033"  # scripted group (container) (typed FeaturePython)
  n = 1
  ref = P_element
FEATURE [App::DocumentObjectGroupPython] G4_P  # scripted group (container) (typed FeaturePython)
  Dunit = g/cm3
  Dvalue = 2.2
  Group = -> [P_element089]
  conduct = 2
  density = 1
  expand = 3
  formula = P
  name = G4_P
  specific = 4
FEATURE [App::DocumentObjectGroupPython] S_element115  label="S_element : 034"  # scripted group (container) (typed FeaturePython)
  n = 1
  ref = S_element
FEATURE [App::DocumentObjectGroupPython] G4_S  # scripted group (container) (typed FeaturePython)
  Dunit = g/cm3
  Dvalue = 2
  Group = -> [S_element115]
  conduct = 2
  density = 1
  expand = 3
  formula = S
  name = G4_S
  specific = 4
FEATURE [App::DocumentObjectGroupPython] Cl_element149  label="Cl_element : 075"  # scripted group (container) (typed FeaturePython)
  n = 1
  ref = Cl_element
FEATURE [App::DocumentObjectGroupPython] G4_Cl  # scripted group (container) (typed FeaturePython)
  Dunit = g/cm3
  Dvalue = 0.00299473
  Group = -> [Cl_element149]
  conduct = 2
  density = 1
  expand = 3
  formula = Cl
  name = G4_Cl
  specific = 4
FEATURE [App::DocumentObjectGroupPython] Ar_element010  label="Ar_element : 004"  # scripted group (container) (typed FeaturePython)
  n = 1
  ref = Ar_element
FEATURE [App::DocumentObjectGroupPython] G4_Ar  # scripted group (container) (typed FeaturePython)
  Dunit = g/cm3
  Dvalue = 0.00166201
  Group = -> [Ar_element010]
  conduct = 2
  density = 1
  expand = 3
  formula = Ar
  name = G4_Ar
  specific = 4
FEATURE [App::DocumentObjectGroupPython] K_element065  label="K_element : 013"  # scripted group (container) (typed FeaturePython)
  n = 1
  ref = K_element
FEATURE [App::DocumentObjectGroupPython] G4_K  # scripted group (container) (typed FeaturePython)
  Dunit = g/cm3
  Dvalue = 0.862
  Group = -> [K_element065]
  conduct = 2
  density = 1
  expand = 3
  formula = K
  name = G4_K
  specific = 4
FEATURE [App::DocumentObjectGroupPython] Ca_element070  label="Ca_element : 034"  # scripted group (container) (typed FeaturePython)
  n = 1
  ref = Ca_element
FEATURE [App::DocumentObjectGroupPython] G4_Ca  # scripted group (container) (typed FeaturePython)
  Dunit = g/cm3
  Dvalue = 1.55
  Group = -> [Ca_element070]
  conduct = 2
  density = 1
  expand = 3
  formula = Ca
  name = G4_Ca
  specific = 4
FEATURE [App::DocumentObjectGroupPython] Sc_element005  label="Sc_element : 004"  # scripted group (container) (typed FeaturePython)
  n = 1
  ref = Sc_element
FEATURE [App::DocumentObjectGroupPython] G4_Sc  # scripted group (container) (typed FeaturePython)
  Dunit = g/cm3
  Dvalue = 2.989
  Group = -> [Sc_element005]
  conduct = 2
  density = 1
  expand = 3
  formula = Sc
  name = G4_Sc
  specific = 4
FEATURE [App::DocumentObjectGroupPython] Ti_element020  label="Ti_element : 009"  # scripted group (container) (typed FeaturePython)
  n = 1
  ref = Ti_element
FEATURE [App::DocumentObjectGroupPython] G4_Ti  # scripted group (container) (typed FeaturePython)
  Dunit = g/cm3
  Dvalue = 4.54
  Group = -> [Ti_element020]
  conduct = 2
  density = 1
  expand = 3
  formula = Ti
  name = G4_Ti
  specific = 4
FEATURE [App::DocumentObjectGroupPython] V_element005  label="V_element : 004"  # scripted group (container) (typed FeaturePython)
  n = 1
  ref = V_element
FEATURE [App::DocumentObjectGroupPython] G4_V  # scripted group (container) (typed FeaturePython)
  Dunit = g/cm3
  Dvalue = 6.11
  Group = -> [V_element005]
  conduct = 2
  density = 1
  expand = 3
  formula = V
  name = G4_V
  specific = 4
FEATURE [App::DocumentObjectGroupPython] Cr_element009  label="Cr_element : 023"  # scripted group (container) (typed FeaturePython)
  n = 1
  ref = Cr_element
FEATURE [App::DocumentObjectGroupPython] G4_Cr  # scripted group (container) (typed FeaturePython)
  Dunit = g/cm3
  Dvalue = 7.18
  Group = -> [Cr_element009]
  conduct = 2
  density = 1
  expand = 3
  formula = Cr
  name = G4_Cr
  specific = 4
FEATURE [App::DocumentObjectGroupPython] Mn_element005  label="Mn_element : 004"  # scripted group (container) (typed FeaturePython)
  n = 1
  ref = Mn_element
FEATURE [App::DocumentObjectGroupPython] G4_Mn  # scripted group (container) (typed FeaturePython)
  Dunit = g/cm3
  Dvalue = 7.44
  Group = -> [Mn_element005]
  conduct = 2
  density = 1
  expand = 3
  formula = Mn
  name = G4_Mn
  specific = 4
FEATURE [App::DocumentObjectGroupPython] Fe_element039  label="Fe_element : 020"  # scripted group (container) (typed FeaturePython)
  n = 1
  ref = Fe_element
FEATURE [App::DocumentObjectGroupPython] G4_Fe  # scripted group (container) (typed FeaturePython)
  Dunit = g/cm3
  Dvalue = 7.874
  Group = -> [Fe_element039]
  conduct = 2
  density = 1
  expand = 3
  formula = Fe
  name = G4_Fe
  specific = 4
FEATURE [App::DocumentObjectGroupPython] Co_element005  label="Co_element : 004"  # scripted group (container) (typed FeaturePython)
  n = 1
  ref = Co_element
FEATURE [App::DocumentObjectGroupPython] G4_Co  # scripted group (container) (typed FeaturePython)
  Dunit = g/cm3
  Dvalue = 8.9
  Group = -> [Co_element005]
  conduct = 2
  density = 1
  expand = 3
  formula = Co
  name = G4_Co
  specific = 4
FEATURE [App::DocumentObjectGroupPython] Ni_element009  label="Ni_element : 013"  # scripted group (container) (typed FeaturePython)
  n = 1
  ref = Ni_element
FEATURE [App::DocumentObjectGroupPython] G4_Ni  # scripted group (container) (typed FeaturePython)
  Dunit = g/cm3
  Dvalue = 8.902
  Group = -> [Ni_element009]
  conduct = 2
  density = 1
  expand = 3
  formula = Ni
  name = G4_Ni
  specific = 4
FEATURE [App::DocumentObjectGroupPython] Cu_element013  label="Cu_element : 096"  # scripted group (container) (typed FeaturePython)
  n = 1
  ref = Cu_element
FEATURE [App::DocumentObjectGroupPython] G4_Cu  # scripted group (container) (typed FeaturePython)
  Dunit = g/cm3
  Dvalue = 8.96
  Group = -> [Cu_element013]
  conduct = 2
  density = 1
  expand = 3
  formula = Cu
  name = G4_Cu
  specific = 4
FEATURE [App::DocumentObjectGroupPython] Zn_element013  label="Zn_element : 042"  # scripted group (container) (typed FeaturePython)
  n = 1
  ref = Zn_element
FEATURE [App::DocumentObjectGroupPython] G4_Zn  # scripted group (container) (typed FeaturePython)
  Dunit = g/cm3
  Dvalue = 7.133
  Group = -> [Zn_element013]
  conduct = 2
  density = 1
  expand = 3
  formula = Zn
  name = G4_Zn
  specific = 4
FEATURE [App::DocumentObjectGroupPython] Ga_element010  label="Ga_element : 009"  # scripted group (container) (typed FeaturePython)
  n = 1
  ref = Ga_element
FEATURE [App::DocumentObjectGroupPython] G4_Ga  # scripted group (container) (typed FeaturePython)
  Dunit = g/cm3
  Dvalue = 5.904
  Group = -> [Ga_element010]
  conduct = 2
  density = 1
  expand = 3
  formula = Ga
  name = G4_Ga
  specific = 4
FEATURE [App::DocumentObjectGroupPython] Ge_element010  label="Ge_element : 009"  # scripted group (container) (typed FeaturePython)
  n = 1
  ref = Ge_element
FEATURE [App::DocumentObjectGroupPython] G4_Ge  # scripted group (container) (typed FeaturePython)
  Dunit = g/cm3
  Dvalue = 5.323
  Group = -> [Ge_element010]
  conduct = 2
  density = 1
  expand = 3
  formula = Ge
  name = G4_Ge
  specific = 4
FEATURE [App::DocumentObjectGroupPython] As_element015  label="As_element : 009"  # scripted group (container) (typed FeaturePython)
  n = 1
  ref = As_element
FEATURE [App::DocumentObjectGroupPython] G4_As  # scripted group (container) (typed FeaturePython)
  Dunit = g/cm3
  Dvalue = 5.73
  Group = -> [As_element015]
  conduct = 2
  density = 1
  expand = 3
  formula = As
  name = G4_As
  specific = 4
FEATURE [App::DocumentObjectGroupPython] Se_element005  label="Se_element : 004"  # scripted group (container) (typed FeaturePython)
  n = 1
  ref = Se_element
FEATURE [App::DocumentObjectGroupPython] G4_Se  # scripted group (container) (typed FeaturePython)
  Dunit = g/cm3
  Dvalue = 4.5
  Group = -> [Se_element005]
  conduct = 2
  density = 1
  expand = 3
  formula = Se
  name = G4_Se
  specific = 4
FEATURE [App::DocumentObjectGroupPython] Br_element035  label="Br_element : 019"  # scripted group (container) (typed FeaturePython)
  n = 1
  ref = Br_element
FEATURE [App::DocumentObjectGroupPython] G4_Br  # scripted group (container) (typed FeaturePython)
  Dunit = g/cm3
  Dvalue = 0.0070721
  Group = -> [Br_element035]
  conduct = 2
  density = 1
  expand = 3
  formula = Br
  name = G4_Br
  specific = 4
FEATURE [App::DocumentObjectGroupPython] Kr_element005  label="Kr_element : 004"  # scripted group (container) (typed FeaturePython)
  n = 1
  ref = Kr_element
FEATURE [App::DocumentObjectGroupPython] G4_Kr  # scripted group (container) (typed FeaturePython)
  Dunit = g/cm3
  Dvalue = 0.00347832
  Group = -> [Kr_element005]
  conduct = 2
  density = 1
  expand = 3
  formula = Kr
  name = G4_Kr
  specific = 4
FEATURE [App::DocumentObjectGroupPython] Rb_element005  label="Rb_element : 004"  # scripted group (container) (typed FeaturePython)
  n = 1
  ref = Rb_element
FEATURE [App::DocumentObjectGroupPython] G4_Rb  # scripted group (container) (typed FeaturePython)
  Dunit = g/cm3
  Dvalue = 1.532
  Group = -> [Rb_element005]
  conduct = 2
  density = 1
  expand = 3
  formula = Rb
  name = G4_Rb
  specific = 4
FEATURE [App::DocumentObjectGroupPython] Sr_element005  label="Sr_element : 004"  # scripted group (container) (typed FeaturePython)
  n = 1
  ref = Sr_element
FEATURE [App::DocumentObjectGroupPython] G4_Sr  # scripted group (container) (typed FeaturePython)
  Dunit = g/cm3
  Dvalue = 2.54
  Group = -> [Sr_element005]
  conduct = 2
  density = 1
  expand = 3
  formula = Sr
  name = G4_Sr
  specific = 4
FEATURE [App::DocumentObjectGroupPython] Y_element005  label="Y_element : 004"  # scripted group (container) (typed FeaturePython)
  n = 1
  ref = Y_element
FEATURE [App::DocumentObjectGroupPython] G4_Y  # scripted group (container) (typed FeaturePython)
  Dunit = g/cm3
  Dvalue = 4.469
  Group = -> [Y_element005]
  conduct = 2
  density = 1
  expand = 3
  formula = Y
  name = G4_Y
  specific = 4
FEATURE [App::DocumentObjectGroupPython] Zr_element005  label="Zr_element : 004"  # scripted group (container) (typed FeaturePython)
  n = 1
  ref = Zr_element
FEATURE [App::DocumentObjectGroupPython] G4_Zr  # scripted group (container) (typed FeaturePython)
  Dunit = g/cm3
  Dvalue = 6.506
  Group = -> [Zr_element005]
  conduct = 2
  density = 1
  expand = 3
  formula = Zr
  name = G4_Zr
  specific = 4
FEATURE [App::DocumentObjectGroupPython] Nb_element005  label="Nb_element : 004"  # scripted group (container) (typed FeaturePython)
  n = 1
  ref = Nb_element
FEATURE [App::DocumentObjectGroupPython] G4_Nb  # scripted group (container) (typed FeaturePython)
  Dunit = g/cm3
  Dvalue = 8.57
  Group = -> [Nb_element005]
  conduct = 2
  density = 1
  expand = 3
  formula = Nb
  name = G4_Nb
  specific = 4
FEATURE [App::DocumentObjectGroupPython] Mo_element005  label="Mo_element : 004"  # scripted group (container) (typed FeaturePython)
  n = 1
  ref = Mo_element
FEATURE [App::DocumentObjectGroupPython] G4_Mo  # scripted group (container) (typed FeaturePython)
  Dunit = g/cm3
  Dvalue = 10.22
  Group = -> [Mo_element005]
  conduct = 2
  density = 1
  expand = 3
  formula = Mo
  name = G4_Mo
  specific = 4
FEATURE [App::DocumentObjectGroupPython] Tc_element005  label="Tc_element : 004"  # scripted group (container) (typed FeaturePython)
  n = 1
  ref = Tc_element
FEATURE [App::DocumentObjectGroupPython] G4_Tc  # scripted group (container) (typed FeaturePython)
  Dunit = g/cm3
  Dvalue = 11.5
  Group = -> [Tc_element005]
  conduct = 2
  density = 1
  expand = 3
  formula = Tc
  name = G4_Tc
  specific = 4
FEATURE [App::DocumentObjectGroupPython] Ru_element005  label="Ru_element : 004"  # scripted group (container) (typed FeaturePython)
  n = 1
  ref = Ru_element
FEATURE [App::DocumentObjectGroupPython] G4_Ru  # scripted group (container) (typed FeaturePython)
  Dunit = g/cm3
  Dvalue = 12.41
  Group = -> [Ru_element005]
  conduct = 2
  density = 1
  expand = 3
  formula = Ru
  name = G4_Ru
  specific = 4
FEATURE [App::DocumentObjectGroupPython] Rh_element005  label="Rh_element : 004"  # scripted group (container) (typed FeaturePython)
  n = 1
  ref = Rh_element
FEATURE [App::DocumentObjectGroupPython] G4_Rh  # scripted group (container) (typed FeaturePython)
  Dunit = g/cm3
  Dvalue = 12.41
  Group = -> [Rh_element005]
  conduct = 2
  density = 1
  expand = 3
  formula = Rh
  name = G4_Rh
  specific = 4
FEATURE [App::DocumentObjectGroupPython] Pd_element005  label="Pd_element : 004"  # scripted group (container) (typed FeaturePython)
  n = 1
  ref = Pd_element
FEATURE [App::DocumentObjectGroupPython] G4_Pd  # scripted group (container) (typed FeaturePython)
  Dunit = g/cm3
  Dvalue = 12.02
  Group = -> [Pd_element005]
  conduct = 2
  density = 1
  expand = 3
  formula = Pd
  name = G4_Pd
  specific = 4
FEATURE [App::DocumentObjectGroupPython] Ag_element030  label="Ag_element : 019"  # scripted group (container) (typed FeaturePython)
  n = 1
  ref = Ag_element
FEATURE [App::DocumentObjectGroupPython] G4_Ag  # scripted group (container) (typed FeaturePython)
  Dunit = g/cm3
  Dvalue = 10.5
  Group = -> [Ag_element030]
  conduct = 2
  density = 1
  expand = 3
  formula = Ag
  name = G4_Ag
  specific = 4
FEATURE [App::DocumentObjectGroupPython] Cd_element015  label="Cd_element : 014"  # scripted group (container) (typed FeaturePython)
  n = 1
  ref = Cd_element
FEATURE [App::DocumentObjectGroupPython] G4_Cd  # scripted group (container) (typed FeaturePython)
  Dunit = g/cm3
  Dvalue = 8.65
  Group = -> [Cd_element015]
  conduct = 2
  density = 1
  expand = 3
  formula = Cd
  name = G4_Cd
  specific = 4
FEATURE [App::DocumentObjectGroupPython] In_element005  label="In_element : 004"  # scripted group (container) (typed FeaturePython)
  n = 1
  ref = In_element
FEATURE [App::DocumentObjectGroupPython] G4_In  # scripted group (container) (typed FeaturePython)
  Dunit = g/cm3
  Dvalue = 7.31
  Group = -> [In_element005]
  conduct = 2
  density = 1
  expand = 3
  formula = In
  name = G4_In
  specific = 4
FEATURE [App::DocumentObjectGroupPython] Sn_element005  label="Sn_element : 004"  # scripted group (container) (typed FeaturePython)
  n = 1
  ref = Sn_element
FEATURE [App::DocumentObjectGroupPython] G4_Sn  # scripted group (container) (typed FeaturePython)
  Dunit = g/cm3
  Dvalue = 7.31
  Group = -> [Sn_element005]
  conduct = 2
  density = 1
  expand = 3
  formula = Sn
  name = G4_Sn
  specific = 4
FEATURE [App::DocumentObjectGroupPython] Sb_element005  label="Sb_element : 004"  # scripted group (container) (typed FeaturePython)
  n = 1
  ref = Sb_element
FEATURE [App::DocumentObjectGroupPython] G4_Sb  # scripted group (container) (typed FeaturePython)
  Dunit = g/cm3
  Dvalue = 6.691
  Group = -> [Sb_element005]
  conduct = 2
  density = 1
  expand = 3
  formula = Sb
  name = G4_Sb
  specific = 4
FEATURE [App::DocumentObjectGroupPython] Te_element010  label="Te_element : 009"  # scripted group (container) (typed FeaturePython)
  n = 1
  ref = Te_element
FEATURE [App::DocumentObjectGroupPython] G4_Te  # scripted group (container) (typed FeaturePython)
  Dunit = g/cm3
  Dvalue = 6.24
  Group = -> [Te_element010]
  conduct = 2
  density = 1
  expand = 3
  formula = Te
  name = G4_Te
  specific = 4
FEATURE [App::DocumentObjectGroupPython] I_element050  label="I_element : 032"  # scripted group (container) (typed FeaturePython)
  n = 1
  ref = I_element
FEATURE [App::DocumentObjectGroupPython] G4_I  # scripted group (container) (typed FeaturePython)
  Dunit = g/cm3
  Dvalue = 4.93
  Group = -> [I_element050]
  conduct = 2
  density = 1
  expand = 3
  formula = I
  name = G4_I
  specific = 4
FEATURE [App::DocumentObjectGroupPython] Xe_element005  label="Xe_element : 004"  # scripted group (container) (typed FeaturePython)
  n = 1
  ref = Xe_element
FEATURE [App::DocumentObjectGroupPython] G4_Xe  # scripted group (container) (typed FeaturePython)
  Dunit = g/cm3
  Dvalue = 0.00548536
  Group = -> [Xe_element005]
  conduct = 2
  density = 1
  expand = 3
  formula = Xe
  name = G4_Xe
  specific = 4
FEATURE [App::DocumentObjectGroupPython] Cs_element015  label="Cs_element : 014"  # scripted group (container) (typed FeaturePython)
  n = 1
  ref = Cs_element
FEATURE [App::DocumentObjectGroupPython] G4_Cs  # scripted group (container) (typed FeaturePython)
  Dunit = g/cm3
  Dvalue = 1.873
  Group = -> [Cs_element015]
  conduct = 2
  density = 1
  expand = 3
  formula = Cs
  name = G4_Cs
  specific = 4
FEATURE [App::DocumentObjectGroupPython] Ba_element015  label="Ba_element : 014"  # scripted group (container) (typed FeaturePython)
  n = 1
  ref = Ba_element
FEATURE [App::DocumentObjectGroupPython] G4_Ba  # scripted group (container) (typed FeaturePython)
  Dunit = g/cm3
  Dvalue = 3.5
  Group = -> [Ba_element015]
  conduct = 2
  density = 1
  expand = 3
  formula = Ba
  name = G4_Ba
  specific = 4
FEATURE [App::DocumentObjectGroupPython] La_element015  label="La_element : 013"  # scripted group (container) (typed FeaturePython)
  n = 1
  ref = La_element
FEATURE [App::DocumentObjectGroupPython] G4_La  # scripted group (container) (typed FeaturePython)
  Dunit = g/cm3
  Dvalue = 6.154
  Group = -> [La_element015]
  conduct = 2
  density = 1
  expand = 3
  formula = La
  name = G4_La
  specific = 4
FEATURE [App::DocumentObjectGroupPython] Ce_element010  label="Ce_element : 004"  # scripted group (container) (typed FeaturePython)
  n = 1
  ref = Ce_element
FEATURE [App::DocumentObjectGroupPython] G4_Ce  # scripted group (container) (typed FeaturePython)
  Dunit = g/cm3
  Dvalue = 6.657
  Group = -> [Ce_element010]
  conduct = 2
  density = 1
  expand = 3
  formula = Ce
  name = G4_Ce
  specific = 4
FEATURE [App::DocumentObjectGroupPython] Pr_element005  label="Pr_element : 004"  # scripted group (container) (typed FeaturePython)
  n = 1
  ref = Pr_element
FEATURE [App::DocumentObjectGroupPython] G4_Pr  # scripted group (container) (typed FeaturePython)
  Dunit = g/cm3
  Dvalue = 6.71
  Group = -> [Pr_element005]
  conduct = 2
  density = 1
  expand = 3
  formula = Pr
  name = G4_Pr
  specific = 4
FEATURE [App::DocumentObjectGroupPython] Nd_element005  label="Nd_element : 004"  # scripted group (container) (typed FeaturePython)
  n = 1
  ref = Nd_element
FEATURE [App::DocumentObjectGroupPython] G4_Nd  # scripted group (container) (typed FeaturePython)
  Dunit = g/cm3
  Dvalue = 6.9
  Group = -> [Nd_element005]
  conduct = 2
  density = 1
  expand = 3
  formula = Nd
  name = G4_Nd
  specific = 4
FEATURE [App::DocumentObjectGroupPython] Pm_element005  label="Pm_element : 004"  # scripted group (container) (typed FeaturePython)
  n = 1
  ref = Pm_element
FEATURE [App::DocumentObjectGroupPython] G4_Pm  # scripted group (container) (typed FeaturePython)
  Dunit = g/cm3
  Dvalue = 7.22
  Group = -> [Pm_element005]
  conduct = 2
  density = 1
  expand = 3
  formula = Pm
  name = G4_Pm
  specific = 4
FEATURE [App::DocumentObjectGroupPython] Sm_element005  label="Sm_element : 004"  # scripted group (container) (typed FeaturePython)
  n = 1
  ref = Sm_element
FEATURE [App::DocumentObjectGroupPython] G4_Sm  # scripted group (container) (typed FeaturePython)
  Dunit = g/cm3
  Dvalue = 7.46
  Group = -> [Sm_element005]
  conduct = 2
  density = 1
  expand = 3
  formula = Sm
  name = G4_Sm
  specific = 4
FEATURE [App::DocumentObjectGroupPython] Eu_element005  label="Eu_element : 004"  # scripted group (container) (typed FeaturePython)
  n = 1
  ref = Eu_element
FEATURE [App::DocumentObjectGroupPython] G4_Eu  # scripted group (container) (typed FeaturePython)
  Dunit = g/cm3
  Dvalue = 5.243
  Group = -> [Eu_element005]
  conduct = 2
  density = 1
  expand = 3
  formula = Eu
  name = G4_Eu
  specific = 4
FEATURE [App::DocumentObjectGroupPython] Gd_element010  label="Gd_element : 008"  # scripted group (container) (typed FeaturePython)
  n = 1
  ref = Gd_element
FEATURE [App::DocumentObjectGroupPython] G4_Gd  # scripted group (container) (typed FeaturePython)
  Dunit = g/cm3
  Dvalue = 7.9004
  Group = -> [Gd_element010]
  conduct = 2
  density = 1
  expand = 3
  formula = Gd
  name = G4_Gd
  specific = 4
FEATURE [App::DocumentObjectGroupPython] Tb_element005  label="Tb_element : 004"  # scripted group (container) (typed FeaturePython)
  n = 1
  ref = Tb_element
FEATURE [App::DocumentObjectGroupPython] G4_Tb  # scripted group (container) (typed FeaturePython)
  Dunit = g/cm3
  Dvalue = 8.229
  Group = -> [Tb_element005]
  conduct = 2
  density = 1
  expand = 3
  formula = Tb
  name = G4_Tb
  specific = 4
FEATURE [App::DocumentObjectGroupPython] Dy_element005  label="Dy_element : 004"  # scripted group (container) (typed FeaturePython)
  n = 1
  ref = Dy_element
FEATURE [App::DocumentObjectGroupPython] G4_Dy  # scripted group (container) (typed FeaturePython)
  Dunit = g/cm3
  Dvalue = 8.55
  Group = -> [Dy_element005]
  conduct = 2
  density = 1
  expand = 3
  formula = Dy
  name = G4_Dy
  specific = 4
FEATURE [App::DocumentObjectGroupPython] Ho_element005  label="Ho_element : 004"  # scripted group (container) (typed FeaturePython)
  n = 1
  ref = Ho_element
FEATURE [App::DocumentObjectGroupPython] G4_Ho  # scripted group (container) (typed FeaturePython)
  Dunit = g/cm3
  Dvalue = 8.795
  Group = -> [Ho_element005]
  conduct = 2
  density = 1
  expand = 3
  formula = Ho
  name = G4_Ho
  specific = 4
FEATURE [App::DocumentObjectGroupPython] Er_element005  label="Er_element : 004"  # scripted group (container) (typed FeaturePython)
  n = 1
  ref = Er_element
FEATURE [App::DocumentObjectGroupPython] G4_Er  # scripted group (container) (typed FeaturePython)
  Dunit = g/cm3
  Dvalue = 9.066
  Group = -> [Er_element005]
  conduct = 2
  density = 1
  expand = 3
  formula = Er
  name = G4_Er
  specific = 4
FEATURE [App::DocumentObjectGroupPython] Tm_element005  label="Tm_element : 004"  # scripted group (container) (typed FeaturePython)
  n = 1
  ref = Tm_element
FEATURE [App::DocumentObjectGroupPython] G4_Tm  # scripted group (container) (typed FeaturePython)
  Dunit = g/cm3
  Dvalue = 9.321
  Group = -> [Tm_element005]
  conduct = 2
  density = 1
  expand = 3
  formula = Tm
  name = G4_Tm
  specific = 4
FEATURE [App::DocumentObjectGroupPython] Yb_element005  label="Yb_element : 004"  # scripted group (container) (typed FeaturePython)
  n = 1
  ref = Yb_element
FEATURE [App::DocumentObjectGroupPython] G4_Yb  # scripted group (container) (typed FeaturePython)
  Dunit = g/cm3
  Dvalue = 6.73
  Group = -> [Yb_element005]
  conduct = 2
  density = 1
  expand = 3
  formula = Yb
  name = G4_Yb
  specific = 4
FEATURE [App::DocumentObjectGroupPython] Lu_element005  label="Lu_element : 004"  # scripted group (container) (typed FeaturePython)
  n = 1
  ref = Lu_element
FEATURE [App::DocumentObjectGroupPython] G4_Lu  # scripted group (container) (typed FeaturePython)
  Dunit = g/cm3
  Dvalue = 9.84
  Group = -> [Lu_element005]
  conduct = 2
  density = 1
  expand = 3
  formula = Lu
  name = G4_Lu
  specific = 4
FEATURE [App::DocumentObjectGroupPython] Hf_element005  label="Hf_element : 004"  # scripted group (container) (typed FeaturePython)
  n = 1
  ref = Hf_element
FEATURE [App::DocumentObjectGroupPython] G4_Hf  # scripted group (container) (typed FeaturePython)
  Dunit = g/cm3
  Dvalue = 13.31
  Group = -> [Hf_element005]
  conduct = 2
  density = 1
  expand = 3
  formula = Hf
  name = G4_Hf
  specific = 4
FEATURE [App::DocumentObjectGroupPython] Ta_element005  label="Ta_element : 004"  # scripted group (container) (typed FeaturePython)
  n = 1
  ref = Ta_element
FEATURE [App::DocumentObjectGroupPython] G4_Ta  # scripted group (container) (typed FeaturePython)
  Dunit = g/cm3
  Dvalue = 16.654
  Group = -> [Ta_element005]
  conduct = 2
  density = 1
  expand = 3
  formula = Ta
  name = G4_Ta
  specific = 4
FEATURE [App::DocumentObjectGroupPython] W_element024  label="W_element : 023"  # scripted group (container) (typed FeaturePython)
  n = 1
  ref = W_element
FEATURE [App::DocumentObjectGroupPython] G4_W  # scripted group (container) (typed FeaturePython)
  Dunit = g/cm3
  Dvalue = 19.3
  Group = -> [W_element024]
  conduct = 2
  density = 1
  expand = 3
  formula = W
  name = G4_W
  specific = 4
FEATURE [App::DocumentObjectGroupPython] Re_element005  label="Re_element : 004"  # scripted group (container) (typed FeaturePython)
  n = 1
  ref = Re_element
FEATURE [App::DocumentObjectGroupPython] G4_Re  # scripted group (container) (typed FeaturePython)
  Dunit = g/cm3
  Dvalue = 21.02
  Group = -> [Re_element005]
  conduct = 2
  density = 1
  expand = 3
  formula = Re
  name = G4_Re
  specific = 4
FEATURE [App::DocumentObjectGroupPython] Os_element005  label="Os_element : 004"  # scripted group (container) (typed FeaturePython)
  n = 1
  ref = Os_element
FEATURE [App::DocumentObjectGroupPython] G4_Os  # scripted group (container) (typed FeaturePython)
  Dunit = g/cm3
  Dvalue = 22.57
  Group = -> [Os_element005]
  conduct = 2
  density = 1
  expand = 3
  formula = Os
  name = G4_Os
  specific = 4
FEATURE [App::DocumentObjectGroupPython] Ir_element005  label="Ir_element : 004"  # scripted group (container) (typed FeaturePython)
  n = 1
  ref = Ir_element
FEATURE [App::DocumentObjectGroupPython] G4_Ir  # scripted group (container) (typed FeaturePython)
  Dunit = g/cm3
  Dvalue = 22.42
  Group = -> [Ir_element005]
  conduct = 2
  density = 1
  expand = 3
  formula = Ir
  name = G4_Ir
  specific = 4
FEATURE [App::DocumentObjectGroupPython] Pt_element005  label="Pt_element : 004"  # scripted group (container) (typed FeaturePython)
  n = 1
  ref = Pt_element
FEATURE [App::DocumentObjectGroupPython] G4_Pt  # scripted group (container) (typed FeaturePython)
  Dunit = g/cm3
  Dvalue = 21.45
  Group = -> [Pt_element005]
  conduct = 2
  density = 1
  expand = 3
  formula = Pt
  name = G4_Pt
  specific = 4
FEATURE [App::DocumentObjectGroupPython] Au_element005  label="Au_element : 004"  # scripted group (container) (typed FeaturePython)
  n = 1
  ref = Au_element
FEATURE [App::DocumentObjectGroupPython] G4_Au  # scripted group (container) (typed FeaturePython)
  Dunit = g/cm3
  Dvalue = 19.32
  Group = -> [Au_element005]
  conduct = 2
  density = 1
  expand = 3
  formula = Au
  name = G4_Au
  specific = 4
FEATURE [App::DocumentObjectGroupPython] Hg_element010  label="Hg_element : 009"  # scripted group (container) (typed FeaturePython)
  n = 1
  ref = Hg_element
FEATURE [App::DocumentObjectGroupPython] G4_Hg  # scripted group (container) (typed FeaturePython)
  Dunit = g/cm3
  Dvalue = 13.546
  Group = -> [Hg_element010]
  conduct = 2
  density = 1
  expand = 3
  formula = Hg
  name = G4_Hg
  specific = 4
FEATURE [App::DocumentObjectGroupPython] Tl_element010  label="Tl_element : 009"  # scripted group (container) (typed FeaturePython)
  n = 1
  ref = Tl_element
FEATURE [App::DocumentObjectGroupPython] G4_Tl  # scripted group (container) (typed FeaturePython)
  Dunit = g/cm3
  Dvalue = 11.72
  Group = -> [Tl_element010]
  conduct = 2
  density = 1
  expand = 3
  formula = Tl
  name = G4_Tl
  specific = 4
FEATURE [App::DocumentObjectGroupPython] Pb_element027  label="Pb_element : 012"  # scripted group (container) (typed FeaturePython)
  n = 1
  ref = Pb_element
FEATURE [App::DocumentObjectGroupPython] G4_Pb  # scripted group (container) (typed FeaturePython)
  Dunit = g/cm3
  Dvalue = 11.35
  Group = -> [Pb_element027]
  conduct = 2
  density = 1
  expand = 3
  formula = Pb
  name = G4_Pb
  specific = 4
FEATURE [App::DocumentObjectGroupPython] Bi_element010  label="Bi_element : 010"  # scripted group (container) (typed FeaturePython)
  n = 1
  ref = Bi_element
FEATURE [App::DocumentObjectGroupPython] G4_Bi  # scripted group (container) (typed FeaturePython)
  Dunit = g/cm3
  Dvalue = 9.747
  Group = -> [Bi_element010]
  conduct = 2
  density = 1
  expand = 3
  formula = Bi
  name = G4_Bi
  specific = 4
FEATURE [App::DocumentObjectGroupPython] Po_element005  label="Po_element : 004"  # scripted group (container) (typed FeaturePython)
  n = 1
  ref = Po_element
FEATURE [App::DocumentObjectGroupPython] G4_Po  # scripted group (container) (typed FeaturePython)
  Dunit = g/cm3
  Dvalue = 9.32
  Group = -> [Po_element005]
  conduct = 2
  density = 1
  expand = 3
  formula = Po
  name = G4_Po
  specific = 4
FEATURE [App::DocumentObjectGroupPython] At_element005  label="At_element : 004"  # scripted group (container) (typed FeaturePython)
  n = 1
  ref = At_element
FEATURE [App::DocumentObjectGroupPython] G4_At  # scripted group (container) (typed FeaturePython)
  Dunit = g/cm3
  Dvalue = 9.32
  Group = -> [At_element005]
  conduct = 2
  density = 1
  expand = 3
  formula = At
  name = G4_At
  specific = 4
FEATURE [App::DocumentObjectGroupPython] Rn_element005  label="Rn_element : 004"  # scripted group (container) (typed FeaturePython)
  n = 1
  ref = Rn_element
FEATURE [App::DocumentObjectGroupPython] G4_Rn  # scripted group (container) (typed FeaturePython)
  Dunit = g/cm3
  Dvalue = 0.00900662
  Group = -> [Rn_element005]
  conduct = 2
  density = 1
  expand = 3
  formula = Rn
  name = G4_Rn
  specific = 4
FEATURE [App::DocumentObjectGroupPython] Fr_element005  label="Fr_element : 004"  # scripted group (container) (typed FeaturePython)
  n = 1
  ref = Fr_element
FEATURE [App::DocumentObjectGroupPython] G4_Fr  # scripted group (container) (typed FeaturePython)
  Dunit = g/cm3
  Dvalue = 1
  Group = -> [Fr_element005]
  conduct = 2
  density = 1
  expand = 3
  formula = Fr
  name = G4_Fr
  specific = 4
FEATURE [App::DocumentObjectGroupPython] Ra_element005  label="Ra_element : 004"  # scripted group (container) (typed FeaturePython)
  n = 1
  ref = Ra_element
FEATURE [App::DocumentObjectGroupPython] G4_Ra  # scripted group (container) (typed FeaturePython)
  Dunit = g/cm3
  Dvalue = 5
  Group = -> [Ra_element005]
  conduct = 2
  density = 1
  expand = 3
  formula = Ra
  name = G4_Ra
  specific = 4
FEATURE [App::DocumentObjectGroupPython] Ac_element005  label="Ac_element : 004"  # scripted group (container) (typed FeaturePython)
  n = 1
  ref = Ac_element
FEATURE [App::DocumentObjectGroupPython] G4_Ac  # scripted group (container) (typed FeaturePython)
  Dunit = g/cm3
  Dvalue = 10.07
  Group = -> [Ac_element005]
  conduct = 2
  density = 1
  expand = 3
  formula = Ac
  name = G4_Ac
  specific = 4
FEATURE [App::DocumentObjectGroupPython] Th_element005  label="Th_element : 004"  # scripted group (container) (typed FeaturePython)
  n = 1
  ref = Th_element
FEATURE [App::DocumentObjectGroupPython] G4_Th  # scripted group (container) (typed FeaturePython)
  Dunit = g/cm3
  Dvalue = 11.72
  Group = -> [Th_element005]
  conduct = 2
  density = 1
  expand = 3
  formula = Th
  name = G4_Th
  specific = 4
FEATURE [App::DocumentObjectGroupPython] Pa_element005  label="Pa_element : 004"  # scripted group (container) (typed FeaturePython)
  n = 1
  ref = Pa_element
FEATURE [App::DocumentObjectGroupPython] G4_Pa  # scripted group (container) (typed FeaturePython)
  Dunit = g/cm3
  Dvalue = 15.37
  Group = -> [Pa_element005]
  conduct = 2
  density = 1
  expand = 3
  formula = Pa
  name = G4_Pa
  specific = 4
FEATURE [App::DocumentObjectGroupPython] U_element020  label="U_element : 019"  # scripted group (container) (typed FeaturePython)
  n = 1
  ref = U_element
FEATURE [App::DocumentObjectGroupPython] G4_U  # scripted group (container) (typed FeaturePython)
  Dunit = g/cm3
  Dvalue = 18.95
  Group = -> [U_element020]
  conduct = 2
  density = 1
  expand = 3
  formula = U
  name = G4_U
  specific = 4
FEATURE [App::DocumentObjectGroupPython] Np_element005  label="Np_element : 004"  # scripted group (container) (typed FeaturePython)
  n = 1
  ref = Np_element
FEATURE [App::DocumentObjectGroupPython] G4_Np  # scripted group (container) (typed FeaturePython)
  Dunit = g/cm3
  Dvalue = 20.25
  Group = -> [Np_element005]
  conduct = 2
  density = 1
  expand = 3
  formula = Np
  name = G4_Np
  specific = 4
FEATURE [App::DocumentObjectGroupPython] Pu_element010  label="Pu_element : 009"  # scripted group (container) (typed FeaturePython)
  n = 1
  ref = Pu_element
FEATURE [App::DocumentObjectGroupPython] G4_Pu  # scripted group (container) (typed FeaturePython)
  Dunit = g/cm3
  Dvalue = 19.84
  Group = -> [Pu_element010]
  conduct = 2
  density = 1
  expand = 3
  formula = Pu
  name = G4_Pu
  specific = 4
FEATURE [App::DocumentObjectGroupPython] Am_element005  label="Am_element : 004"  # scripted group (container) (typed FeaturePython)
  n = 1
  ref = Am_element
FEATURE [App::DocumentObjectGroupPython] G4_Am  # scripted group (container) (typed FeaturePython)
  Dunit = g/cm3
  Dvalue = 13.67
  Group = -> [Am_element005]
  conduct = 2
  density = 1
  expand = 3
  formula = Am
  name = G4_Am
  specific = 4
FEATURE [App::DocumentObjectGroupPython] Cm_element005  label="Cm_element : 004"  # scripted group (container) (typed FeaturePython)
  n = 1
  ref = Cm_element
FEATURE [App::DocumentObjectGroupPython] G4_Cm  # scripted group (container) (typed FeaturePython)
  Dunit = g/cm3
  Dvalue = 13.51
  Group = -> [Cm_element005]
  conduct = 2
  density = 1
  expand = 3
  formula = Cm
  name = G4_Cm
  specific = 4
FEATURE [App::DocumentObjectGroupPython] Bk_element005  label="Bk_element : 004"  # scripted group (container) (typed FeaturePython)
  n = 1
  ref = Bk_element
FEATURE [App::DocumentObjectGroupPython] G4_Bk  # scripted group (container) (typed FeaturePython)
  Dunit = g/cm3
  Dvalue = 14
  Group = -> [Bk_element005]
  conduct = 2
  density = 1
  expand = 3
  formula = Bk
  name = G4_Bk
  specific = 4
FEATURE [App::DocumentObjectGroupPython] Cf_element005  label="Cf_element : 004"  # scripted group (container) (typed FeaturePython)
  n = 1
  ref = Cf_element
FEATURE [App::DocumentObjectGroupPython] G4_Cf  # scripted group (container) (typed FeaturePython)
  Dunit = g/cm3
  Dvalue = 10
  Group = -> [Cf_element005]
  conduct = 2
  density = 1
  expand = 3
  formula = Cf
  name = G4_Cf
  specific = 4
FEATURE [App::DocumentObjectGroupPython] Element  # scripted group (container) (typed FeaturePython)
  Group = -> [G4_H,G4_He,G4_Li,G4_Be,G4_B,G4_C,G4_N,G4_O,G4_F,G4_Ne,G4_Na,G4_Mg,G4_Al,G4_Si,G4_P,G4_S,G4_Cl,G4_Ar,G4_K,G4_Ca,G4_Sc,G4_Ti,G4_V,G4_Cr,G4_Mn,G4_Fe,G4_Co,G4_Ni,G4_Cu,G4_Zn,G4_Ga,G4_Ge,G4_As,G4_Se,G4_Br,G4_Kr,G4_Rb,G4_Sr,G4_Y,G4_Zr,G4_Nb,G4_Mo,G4_Tc,G4_Ru,G4_Rh,G4_Pd,G4_Ag,G4_Cd,G4_In,G4_Sn,G4_Sb,G4_Te,G4_I,G4_Xe,G4_Cs,G4_Ba,G4_La,G4_Ce,G4_Pr,G4_Nd,G4_Pm,G4_Sm,G4_Eu,G4_Gd,G4_Tb,G4_Dy,G4_Ho,G4_Er,+30 more]
FEATURE [App::DocumentObjectGroupPython] H_element666  label="H_element : 431"  # scripted group (container) (typed FeaturePython)
  n = 2
  ref = H_element
FEATURE [App::DocumentObjectGroupPython] G4_lH2  # scripted group (container) (typed FeaturePython)
  Dunit = g/cm3
  Dvalue = 0.0708
  Group = -> [H_element666]
  conduct = 2
  density = 1
  expand = 3
  formula = G4_lH2
  name = G4_lH2
  specific = 4
FEATURE [App::DocumentObjectGroupPython] N_element321  label="N_element : 173"  # scripted group (container) (typed FeaturePython)
  n = 2
  ref = N_element
FEATURE [App::DocumentObjectGroupPython] G4_lN2  # scripted group (container) (typed FeaturePython)
  Dunit = g/cm3
  Dvalue = 0.807
  Group = -> [N_element321]
  conduct = 2
  density = 1
  expand = 3
  formula = G4_lN2
  name = G4_lN2
  specific = 4
FEATURE [App::DocumentObjectGroupPython] O_element626  label="O_element : 399"  # scripted group (container) (typed FeaturePython)
  n = 2
  ref = O_element
FEATURE [App::DocumentObjectGroupPython] G4_lO2  # scripted group (container) (typed FeaturePython)
  Dunit = g/cm3
  Dvalue = 1.141
  Group = -> [O_element626]
  conduct = 2
  density = 1
  expand = 3
  formula = G4_lO2
  name = G4_lO2
  specific = 4
FEATURE [App::DocumentObjectGroupPython] Ar003  label="Ar : 004"  # scripted group (container) (typed FeaturePython)
  n = 1
  ref = Ar
FEATURE [App::DocumentObjectGroupPython] G4_lAr  # scripted group (container) (typed FeaturePython)
  Dunit = g/cm3
  Dvalue = 1.396
  Group = -> [Ar003]
  conduct = 2
  density = 1
  expand = 3
  formula = G4_lAr
  name = G4_lAr
  specific = 4
FEATURE [App::DocumentObjectGroupPython] Br003  label="Br : 004"  # scripted group (container) (typed FeaturePython)
  n = 1
  ref = Br
FEATURE [App::DocumentObjectGroupPython] G4_lBr  # scripted group (container) (typed FeaturePython)
  Dunit = g/cm3
  Dvalue = 3.1028
  Group = -> [Br003]
  conduct = 2
  density = 1
  expand = 3
  formula = G4_lBr
  name = G4_lBr
  specific = 4
FEATURE [App::DocumentObjectGroupPython] Kr003  label="Kr : 004"  # scripted group (container) (typed FeaturePython)
  n = 1
  ref = Kr
FEATURE [App::DocumentObjectGroupPython] G4_lKr  # scripted group (container) (typed FeaturePython)
  Dunit = g/cm3
  Dvalue = 2.418
  Group = -> [Kr003]
  conduct = 2
  density = 1
  expand = 3
  formula = G4_lKr
  name = G4_lKr
  specific = 4
FEATURE [App::DocumentObjectGroupPython] Xe003  label="Xe : 004"  # scripted group (container) (typed FeaturePython)
  n = 1
  ref = Xe
FEATURE [App::DocumentObjectGroupPython] G4_lXe  # scripted group (container) (typed FeaturePython)
  Dunit = g/cm3
  Dvalue = 2.953
  Group = -> [Xe003]
  conduct = 2
  density = 1
  expand = 3
  formula = G4_lXe
  name = G4_lXe
  specific = 4
FEATURE [App::DocumentObjectGroupPython] O_element627  label="O_element : 400"  # scripted group (container) (typed FeaturePython)
  n = 4
  ref = O_element
FEATURE [App::DocumentObjectGroupPython] Pb_element028  label="Pb_element : 013"  # scripted group (container) (typed FeaturePython)
  n = 1
  ref = Pb_element
FEATURE [App::DocumentObjectGroupPython] W_element025  label="W_element : 024"  # scripted group (container) (typed FeaturePython)
  n = 1
  ref = W_element
FEATURE [App::DocumentObjectGroupPython] G4_PbWO4  # scripted group (container) (typed FeaturePython)
  Dunit = g/cm3
  Dvalue = 8.28
  Group = -> [O_element627,Pb_element028,W_element025]
  conduct = 2
  density = 1
  expand = 3
  formula = G4_PbWO4
  name = G4_PbWO4
  specific = 4
FEATURE [App::DocumentObjectGroupPython] alactic003  label="alactic : 004"  # scripted group (container) (typed FeaturePython)
  n = 1
  ref = alactic
FEATURE [App::DocumentObjectGroupPython] G4_Galactic  # scripted group (container) (typed FeaturePython)
  Dunit = g/cm3
  Dvalue = 0
  Group = -> [alactic003]
  conduct = 2
  density = 1
  expand = 3
  formula = G4_Galactic
  name = G4_Galactic
  specific = 4
FEATURE [App::DocumentObjectGroupPython] RAPHITE_POROUS003  label="RAPHITE_POROUS : 004"  # scripted group (container) (typed FeaturePython)
  n = 1
  ref = RAPHITE_POROUS
FEATURE [App::DocumentObjectGroupPython] G4_GRAPHITE_POROUS  # scripted group (container) (typed FeaturePython)
  Dunit = g/cm3
  Dvalue = 1.7
  Group = -> [RAPHITE_POROUS003]
  conduct = 2
  density = 1
  expand = 3
  formula = G4_GRAPHITE_POROUS
  name = G4_GRAPHITE_POROUS
  specific = 4
FEATURE [App::DocumentObjectGroupPython] H_element667  label="H_element : 0.286"  # scripted group (container) (typed FeaturePython)
  n = 0.080538
FEATURE [App::DocumentObjectGroupPython] C_element717  label="C_element : 0.1017"  # scripted group (container) (typed FeaturePython)
  n = 0.599848
FEATURE [App::DocumentObjectGroupPython] O_element628  label="O_element : 0.1007"  # scripted group (container) (typed FeaturePython)
  n = 0.319614
FEATURE [App::DocumentObjectGroupPython] G4_LUCITE  # scripted group (container) (typed FeaturePython)
  Dunit = g/cm3
  Dvalue = 1.19
  Group = -> [H_element667,C_element717,O_element628]
  conduct = 2
  density = 1
  expand = 3
  formula = G4_LUCITE
  name = G4_LUCITE
  specific = 4
FEATURE [App::DocumentObjectGroupPython] Cu_element014  label="Cu_element : 097"  # scripted group (container) (typed FeaturePython)
  n = 62
  ref = Cu_element
FEATURE [App::DocumentObjectGroupPython] Zn_element014  label="Zn_element : 043"  # scripted group (container) (typed FeaturePython)
  n = 35
  ref = Zn_element
FEATURE [App::DocumentObjectGroupPython] Pb_element029  label="Pb_element : 014"  # scripted group (container) (typed FeaturePython)
  n = 3
  ref = Pb_element
FEATURE [App::DocumentObjectGroupPython] G4_BRASS  # scripted group (container) (typed FeaturePython)
  Dunit = g/cm3
  Dvalue = 8.52
  Group = -> [Cu_element014,Zn_element014,Pb_element029]
  conduct = 2
  density = 1
  expand = 3
  formula = G4_BRASS
  name = G4_BRASS
  specific = 4
FEATURE [App::DocumentObjectGroupPython] Cu_element015  label="Cu_element : 098"  # scripted group (container) (typed FeaturePython)
  n = 89
  ref = Cu_element
FEATURE [App::DocumentObjectGroupPython] Zn_element015  label="Zn_element : 044"  # scripted group (container) (typed FeaturePython)
  n = 9
  ref = Zn_element
FEATURE [App::DocumentObjectGroupPython] Pb_element030  label="Pb_element : 015"  # scripted group (container) (typed FeaturePython)
  n = 2
  ref = Pb_element
FEATURE [App::DocumentObjectGroupPython] G4_BRONZE  # scripted group (container) (typed FeaturePython)
  Dunit = g/cm3
  Dvalue = 8.82
  Group = -> [Cu_element015,Zn_element015,Pb_element030]
  conduct = 2
  density = 1
  expand = 3
  formula = G4_BRONZE
  name = G4_BRONZE
  specific = 4
FEATURE [App::DocumentObjectGroupPython] Fe_element040  label="Fe_element : 021"  # scripted group (container) (typed FeaturePython)
  n = 74
  ref = Fe_element
FEATURE [App::DocumentObjectGroupPython] Cr_element010  label="Cr_element : 024"  # scripted group (container) (typed FeaturePython)
  n = 18
  ref = Cr_element
FEATURE [App::DocumentObjectGroupPython] Ni_element010  label="Ni_element : 014"  # scripted group (container) (typed FeaturePython)
  n = 8
  ref = Ni_element
FEATURE [App::DocumentObjectGroupPython] G4_STAINLESS_STEEL  label="G4_STAINLESS-STEEL"  # scripted group (container) (typed FeaturePython)
  Dunit = g/cm3
  Dvalue = 8
  Group = -> [Fe_element040,Cr_element010,Ni_element010]
  conduct = 2
  density = 1
  expand = 3
  formula = G4_STAINLESS-STEEL
  name = G4_STAINLESS-STEEL
  specific = 4
FEATURE [App::DocumentObjectGroupPython] H_element668  label="H_element : 432"  # scripted group (container) (typed FeaturePython)
  n = 18
  ref = H_element
FEATURE [App::DocumentObjectGroupPython] C_element718  label="C_element : 471"  # scripted group (container) (typed FeaturePython)
  n = 12
  ref = C_element
FEATURE [App::DocumentObjectGroupPython] O_element629  label="O_element : 401"  # scripted group (container) (typed FeaturePython)
  n = 7
  ref = O_element
FEATURE [App::DocumentObjectGroupPython] G4_CR39  # scripted group (container) (typed FeaturePython)
  Dunit = g/cm3
  Dvalue = 1.32
  Group = -> [H_element668,C_element718,O_element629]
  conduct = 2
  density = 1
  expand = 3
  formula = G4_CR39
  name = G4_CR39
  specific = 4
FEATURE [App::DocumentObjectGroupPython] H_element669  label="H_element : 433"  # scripted group (container) (typed FeaturePython)
  n = 38
  ref = H_element
FEATURE [App::DocumentObjectGroupPython] C_element719  label="C_element : 472"  # scripted group (container) (typed FeaturePython)
  n = 18
  ref = C_element
FEATURE [App::DocumentObjectGroupPython] O_element630  label="O_element : 402"  # scripted group (container) (typed FeaturePython)
  n = 1
  ref = O_element
FEATURE [App::DocumentObjectGroupPython] G4_OCTADECANOL  # scripted group (container) (typed FeaturePython)
  Dunit = g/cm3
  Dvalue = 0.812
  Group = -> [H_element669,C_element719,O_element630]
  conduct = 2
  density = 1
  expand = 3
  formula = G4_OCTADECANOL
  name = G4_OCTADECANOL
  specific = 4
FEATURE [App::DocumentObjectGroupPython] HEP  # scripted group (container) (typed FeaturePython)
  Group = -> [G4_lH2,G4_lN2,G4_lO2,G4_lAr,G4_lBr,G4_lKr,G4_lXe,G4_PbWO4,G4_Galactic,G4_GRAPHITE_POROUS,G4_LUCITE,G4_BRASS,G4_BRONZE,G4_STAINLESS_STEEL,G4_CR39,G4_OCTADECANOL]
FEATURE [App::DocumentObjectGroupPython] C_element720  label="C_element : 473"  # scripted group (container) (typed FeaturePython)
  n = 14
  ref = C_element
FEATURE [App::DocumentObjectGroupPython] H_element670  label="H_element : 434"  # scripted group (container) (typed FeaturePython)
  n = 10
  ref = H_element
FEATURE [App::DocumentObjectGroupPython] O_element631  label="O_element : 403"  # scripted group (container) (typed FeaturePython)
  n = 2
  ref = O_element
FEATURE [App::DocumentObjectGroupPython] N_element322  label="N_element : 174"  # scripted group (container) (typed FeaturePython)
  n = 2
  ref = N_element
FEATURE [App::DocumentObjectGroupPython] G4_KEVLAR  # scripted group (container) (typed FeaturePython)
  Dunit = g/cm3
  Dvalue = 1.44
  Group = -> [C_element720,H_element670,O_element631,N_element322]
  conduct = 2
  density = 1
  expand = 3
  formula = G4_KEVLAR
  name = G4_KEVLAR
  specific = 4
FEATURE [App::DocumentObjectGroupPython] C_element721  label="C_element : 474"  # scripted group (container) (typed FeaturePython)
  n = 10
  ref = C_element
FEATURE [App::DocumentObjectGroupPython] H_element671  label="H_element : 435"  # scripted group (container) (typed FeaturePython)
  n = 8
  ref = H_element
FEATURE [App::DocumentObjectGroupPython] O_element632  label="O_element : 404"  # scripted group (container) (typed FeaturePython)
  n = 4
  ref = O_element
FEATURE [App::DocumentObjectGroupPython] G4_DACRON  # scripted group (container) (typed FeaturePython)
  Dunit = g/cm3
  Dvalue = 1.4
  Group = -> [C_element721,H_element671,O_element632]
  conduct = 2
  density = 1
  expand = 3
  formula = G4_DACRON
  name = G4_DACRON
  specific = 4
FEATURE [App::DocumentObjectGroupPython] C_element722  label="C_element : 475"  # scripted group (container) (typed FeaturePython)
  n = 4
  ref = C_element
FEATURE [App::DocumentObjectGroupPython] H_element672  label="H_element : 436"  # scripted group (container) (typed FeaturePython)
  n = 5
  ref = H_element
FEATURE [App::DocumentObjectGroupPython] Cl_element150  label="Cl_element : 076"  # scripted group (container) (typed FeaturePython)
  n = 1
  ref = Cl_element
FEATURE [App::DocumentObjectGroupPython] G4_NEOPRENE  # scripted group (container) (typed FeaturePython)
  Dunit = g/cm3
  Dvalue = 1.23
  Group = -> [C_element722,H_element672,Cl_element150]
  conduct = 2
  density = 1
  expand = 3
  formula = G4_NEOPRENE
  name = G4_NEOPRENE
  specific = 4
FEATURE [App::DocumentObjectGroupPython] Space  # scripted group (container) (typed FeaturePython)
  Group = -> [G4_KEVLAR,G4_DACRON,G4_NEOPRENE]
FEATURE [App::DocumentObjectGroupPython] H_element673  label="H_element : 437"  # scripted group (container) (typed FeaturePython)
  n = 5
  ref = H_element
FEATURE [App::DocumentObjectGroupPython] C_element723  label="C_element : 476"  # scripted group (container) (typed FeaturePython)
  n = 4
  ref = C_element
FEATURE [App::DocumentObjectGroupPython] N_element323  label="N_element : 175"  # scripted group (container) (typed FeaturePython)
  n = 3
  ref = N_element
FEATURE [App::DocumentObjectGroupPython] O_element633  label="O_element : 405"  # scripted group (container) (typed FeaturePython)
  n = 1
  ref = O_element
FEATURE [App::DocumentObjectGroupPython] G4_CYTOSINE  # scripted group (container) (typed FeaturePython)
  Dunit = g/cm3
  Dvalue = 1.55
  Group = -> [H_element673,C_element723,N_element323,O_element633]
  conduct = 2
  density = 1
  expand = 3
  formula = G4_CYTOSINE
  name = G4_CYTOSINE
  specific = 4
FEATURE [App::DocumentObjectGroupPython] H_element674  label="H_element : 438"  # scripted group (container) (typed FeaturePython)
  n = 6
  ref = H_element
FEATURE [App::DocumentObjectGroupPython] C_element724  label="C_element : 477"  # scripted group (container) (typed FeaturePython)
  n = 5
  ref = C_element
FEATURE [App::DocumentObjectGroupPython] N_element324  label="N_element : 176"  # scripted group (container) (typed FeaturePython)
  n = 2
  ref = N_element
FEATURE [App::DocumentObjectGroupPython] O_element634  label="O_element : 406"  # scripted group (container) (typed FeaturePython)
  n = 2
  ref = O_element
FEATURE [App::DocumentObjectGroupPython] G4_THYMINE  # scripted group (container) (typed FeaturePython)
  Dunit = g/cm3
  Dvalue = 1.23
  Group = -> [H_element674,C_element724,N_element324,O_element634]
  conduct = 2
  density = 1
  expand = 3
  formula = G4_THYMINE
  name = G4_THYMINE
  specific = 4
FEATURE [App::DocumentObjectGroupPython] H_element675  label="H_element : 439"  # scripted group (container) (typed FeaturePython)
  n = 4
  ref = H_element
FEATURE [App::DocumentObjectGroupPython] C_element725  label="C_element : 478"  # scripted group (container) (typed FeaturePython)
  n = 4
  ref = C_element
FEATURE [App::DocumentObjectGroupPython] N_element325  label="N_element : 177"  # scripted group (container) (typed FeaturePython)
  n = 2
  ref = N_element
FEATURE [App::DocumentObjectGroupPython] O_element635  label="O_element : 407"  # scripted group (container) (typed FeaturePython)
  n = 2
  ref = O_element
FEATURE [App::DocumentObjectGroupPython] G4_URACIL  # scripted group (container) (typed FeaturePython)
  Dunit = g/cm3
  Dvalue = 1.32
  Group = -> [H_element675,C_element725,N_element325,O_element635]
  conduct = 2
  density = 1
  expand = 3
  formula = G4_URACIL
  name = G4_URACIL
  specific = 4
FEATURE [App::DocumentObjectGroupPython] H_element676  label="H_element : 440"  # scripted group (container) (typed FeaturePython)
  n = 4
  ref = H_element
FEATURE [App::DocumentObjectGroupPython] C_element726  label="C_element : 479"  # scripted group (container) (typed FeaturePython)
  n = 5
  ref = C_element
FEATURE [App::DocumentObjectGroupPython] N_element326  label="N_element : 178"  # scripted group (container) (typed FeaturePython)
  n = 5
  ref = N_element
FEATURE [App::DocumentObjectGroupPython] G4_DNA_ADENINE  # scripted group (container) (typed FeaturePython)
  Dunit = g/cm3
  Dvalue = 1
  Group = -> [H_element676,C_element726,N_element326]
  conduct = 2
  density = 1
  expand = 3
  formula = G4_DNA_ADENINE
  name = G4_DNA_ADENINE
  specific = 4
FEATURE [App::DocumentObjectGroupPython] H_element677  label="H_element : 441"  # scripted group (container) (typed FeaturePython)
  n = 4
  ref = H_element
FEATURE [App::DocumentObjectGroupPython] C_element727  label="C_element : 480"  # scripted group (container) (typed FeaturePython)
  n = 5
  ref = C_element
FEATURE [App::DocumentObjectGroupPython] N_element327  label="N_element : 179"  # scripted group (container) (typed FeaturePython)
  n = 5
  ref = N_element
FEATURE [App::DocumentObjectGroupPython] O_element636  label="O_element : 408"  # scripted group (container) (typed FeaturePython)
  n = 1
  ref = O_element
FEATURE [App::DocumentObjectGroupPython] G4_DNA_GUANINE  # scripted group (container) (typed FeaturePython)
  Dunit = g/cm3
  Dvalue = 1
  Group = -> [H_element677,C_element727,N_element327,O_element636]
  conduct = 2
  density = 1
  expand = 3
  formula = G4_DNA_GUANINE
  name = G4_DNA_GUANINE
  specific = 4
FEATURE [App::DocumentObjectGroupPython] H_element678  label="H_element : 442"  # scripted group (container) (typed FeaturePython)
  n = 4
  ref = H_element
FEATURE [App::DocumentObjectGroupPython] C_element728  label="C_element : 481"  # scripted group (container) (typed FeaturePython)
  n = 4
  ref = C_element
FEATURE [App::DocumentObjectGroupPython] N_element328  label="N_element : 180"  # scripted group (container) (typed FeaturePython)
  n = 3
  ref = N_element
FEATURE [App::DocumentObjectGroupPython] O_element637  label="O_element : 409"  # scripted group (container) (typed FeaturePython)
  n = 1
  ref = O_element
FEATURE [App::DocumentObjectGroupPython] G4_DNA_CYTOSINE  # scripted group (container) (typed FeaturePython)
  Dunit = g/cm3
  Dvalue = 1
  Group = -> [H_element678,C_element728,N_element328,O_element637]
  conduct = 2
  density = 1
  expand = 3
  formula = G4_DNA_CYTOSINE
  name = G4_DNA_CYTOSINE
  specific = 4
FEATURE [App::DocumentObjectGroupPython] H_element679  label="H_element : 443"  # scripted group (container) (typed FeaturePython)
  n = 5
  ref = H_element
FEATURE [App::DocumentObjectGroupPython] C_element729  label="C_element : 482"  # scripted group (container) (typed FeaturePython)
  n = 5
  ref = C_element
FEATURE [App::DocumentObjectGroupPython] N_element329  label="N_element : 181"  # scripted group (container) (typed FeaturePython)
  n = 2
  ref = N_element
FEATURE [App::DocumentObjectGroupPython] O_element638  label="O_element : 410"  # scripted group (container) (typed FeaturePython)
  n = 2
  ref = O_element
FEATURE [App::DocumentObjectGroupPython] G4_DNA_THYMINE  # scripted group (container) (typed FeaturePython)
  Dunit = g/cm3
  Dvalue = 1
  Group = -> [H_element679,C_element729,N_element329,O_element638]
  conduct = 2
  density = 1
  expand = 3
  formula = G4_DNA_THYMINE
  name = G4_DNA_THYMINE
  specific = 4
FEATURE [App::DocumentObjectGroupPython] H_element680  label="H_element : 444"  # scripted group (container) (typed FeaturePython)
  n = 3
  ref = H_element
FEATURE [App::DocumentObjectGroupPython] C_element730  label="C_element : 483"  # scripted group (container) (typed FeaturePython)
  n = 4
  ref = C_element
FEATURE [App::DocumentObjectGroupPython] N_element330  label="N_element : 182"  # scripted group (container) (typed FeaturePython)
  n = 2
  ref = N_element
FEATURE [App::DocumentObjectGroupPython] O_element639  label="O_element : 411"  # scripted group (container) (typed FeaturePython)
  n = 2
  ref = O_element
FEATURE [App::DocumentObjectGroupPython] G4_DNA_URACIL  # scripted group (container) (typed FeaturePython)
  Dunit = g/cm3
  Dvalue = 1
  Group = -> [H_element680,C_element730,N_element330,O_element639]
  conduct = 2
  density = 1
  expand = 3
  formula = G4_DNA_URACIL
  name = G4_DNA_URACIL
  specific = 4
FEATURE [App::DocumentObjectGroupPython] H_element681  label="H_element : 445"  # scripted group (container) (typed FeaturePython)
  n = 10
  ref = H_element
FEATURE [App::DocumentObjectGroupPython] C_element731  label="C_element : 484"  # scripted group (container) (typed FeaturePython)
  n = 10
  ref = C_element
FEATURE [App::DocumentObjectGroupPython] N_element331  label="N_element : 183"  # scripted group (container) (typed FeaturePython)
  n = 5
  ref = N_element
FEATURE [App::DocumentObjectGroupPython] O_element640  label="O_element : 412"  # scripted group (container) (typed FeaturePython)
  n = 4
  ref = O_element
FEATURE [App::DocumentObjectGroupPython] G4_DNA_ADENOSINE  # scripted group (container) (typed FeaturePython)
  Dunit = g/cm3
  Dvalue = 1
  Group = -> [H_element681,C_element731,N_element331,O_element640]
  conduct = 2
  density = 1
  expand = 3
  formula = G4_DNA_ADENOSINE
  name = G4_DNA_ADENOSINE
  specific = 4
FEATURE [App::DocumentObjectGroupPython] H_element682  label="H_element : 446"  # scripted group (container) (typed FeaturePython)
  n = 10
  ref = H_element
FEATURE [App::DocumentObjectGroupPython] C_element732  label="C_element : 485"  # scripted group (container) (typed FeaturePython)
  n = 10
  ref = C_element
FEATURE [App::DocumentObjectGroupPython] N_element332  label="N_element : 184"  # scripted group (container) (typed FeaturePython)
  n = 5
  ref = N_element
FEATURE [App::DocumentObjectGroupPython] O_element641  label="O_element : 413"  # scripted group (container) (typed FeaturePython)
  n = 5
  ref = O_element
FEATURE [App::DocumentObjectGroupPython] G4_DNA_GUANOSINE  # scripted group (container) (typed FeaturePython)
  Dunit = g/cm3
  Dvalue = 1
  Group = -> [H_element682,C_element732,N_element332,O_element641]
  conduct = 2
  density = 1
  expand = 3
  formula = G4_DNA_GUANOSINE
  name = G4_DNA_GUANOSINE
  specific = 4
FEATURE [App::DocumentObjectGroupPython] H_element683  label="H_element : 447"  # scripted group (container) (typed FeaturePython)
  n = 10
  ref = H_element
FEATURE [App::DocumentObjectGroupPython] C_element733  label="C_element : 486"  # scripted group (container) (typed FeaturePython)
  n = 9
  ref = C_element
FEATURE [App::DocumentObjectGroupPython] N_element333  label="N_element : 185"  # scripted group (container) (typed FeaturePython)
  n = 3
  ref = N_element
FEATURE [App::DocumentObjectGroupPython] O_element642  label="O_element : 414"  # scripted group (container) (typed FeaturePython)
  n = 5
  ref = O_element
FEATURE [App::DocumentObjectGroupPython] G4_DNA_CYTIDINE  # scripted group (container) (typed FeaturePython)
  Dunit = g/cm3
  Dvalue = 1
  Group = -> [H_element683,C_element733,N_element333,O_element642]
  conduct = 2
  density = 1
  expand = 3
  formula = G4_DNA_CYTIDINE
  name = G4_DNA_CYTIDINE
  specific = 4
FEATURE [App::DocumentObjectGroupPython] H_element684  label="H_element : 448"  # scripted group (container) (typed FeaturePython)
  n = 9
  ref = H_element
FEATURE [App::DocumentObjectGroupPython] C_element734  label="C_element : 487"  # scripted group (container) (typed FeaturePython)
  n = 9
  ref = C_element
FEATURE [App::DocumentObjectGroupPython] N_element334  label="N_element : 186"  # scripted group (container) (typed FeaturePython)
  n = 2
  ref = N_element
FEATURE [App::DocumentObjectGroupPython] O_element643  label="O_element : 415"  # scripted group (container) (typed FeaturePython)
  n = 6
  ref = O_element
FEATURE [App::DocumentObjectGroupPython] G4_DNA_URIDINE  # scripted group (container) (typed FeaturePython)
  Dunit = g/cm3
  Dvalue = 1
  Group = -> [H_element684,C_element734,N_element334,O_element643]
  conduct = 2
  density = 1
  expand = 3
  formula = G4_DNA_URIDINE
  name = G4_DNA_URIDINE
  specific = 4
FEATURE [App::DocumentObjectGroupPython] H_element685  label="H_element : 449"  # scripted group (container) (typed FeaturePython)
  n = 11
  ref = H_element
FEATURE [App::DocumentObjectGroupPython] C_element735  label="C_element : 488"  # scripted group (container) (typed FeaturePython)
  n = 10
  ref = C_element
FEATURE [App::DocumentObjectGroupPython] N_element335  label="N_element : 187"  # scripted group (container) (typed FeaturePython)
  n = 2
  ref = N_element
FEATURE [App::DocumentObjectGroupPython] O_element644  label="O_element : 416"  # scripted group (container) (typed FeaturePython)
  n = 6
  ref = O_element
FEATURE [App::DocumentObjectGroupPython] G4_DNA_METHYLURIDINE  # scripted group (container) (typed FeaturePython)
  Dunit = g/cm3
  Dvalue = 1
  Group = -> [H_element685,C_element735,N_element335,O_element644]
  conduct = 2
  density = 1
  expand = 3
  formula = G4_DNA_METHYLURIDINE
  name = G4_DNA_METHYLURIDINE
  specific = 4
FEATURE [App::DocumentObjectGroupPython] P_element090  label="P_element : 034"  # scripted group (container) (typed FeaturePython)
  n = 1
  ref = P_element
FEATURE [App::DocumentObjectGroupPython] O_element645  label="O_element : 417"  # scripted group (container) (typed FeaturePython)
  n = 3
  ref = O_element
FEATURE [App::DocumentObjectGroupPython] G4_DNA_MONOPHOSPHATE  # scripted group (container) (typed FeaturePython)
  Dunit = g/cm3
  Dvalue = 1
  Group = -> [P_element090,O_element645]
  conduct = 2
  density = 1
  expand = 3
  formula = G4_DNA_MONOPHOSPHATE
  name = G4_DNA_MONOPHOSPHATE
  specific = 4
FEATURE [App::DocumentObjectGroupPython] H_element686  label="H_element : 450"  # scripted group (container) (typed FeaturePython)
  n = 10
  ref = H_element
FEATURE [App::DocumentObjectGroupPython] C_element736  label="C_element : 489"  # scripted group (container) (typed FeaturePython)
  n = 10
  ref = C_element
FEATURE [App::DocumentObjectGroupPython] N_element336  label="N_element : 188"  # scripted group (container) (typed FeaturePython)
  n = 5
  ref = N_element
FEATURE [App::DocumentObjectGroupPython] O_element646  label="O_element : 418"  # scripted group (container) (typed FeaturePython)
  n = 7
  ref = O_element
FEATURE [App::DocumentObjectGroupPython] P_element091  label="P_element : 035"  # scripted group (container) (typed FeaturePython)
  n = 1
  ref = P_element
FEATURE [App::DocumentObjectGroupPython] G4_DNA_A  # scripted group (container) (typed FeaturePython)
  Dunit = g/cm3
  Dvalue = 1
  Group = -> [H_element686,C_element736,N_element336,O_element646,P_element091]
  conduct = 2
  density = 1
  expand = 3
  formula = G4_DNA_A
  name = G4_DNA_A
  specific = 4
FEATURE [App::DocumentObjectGroupPython] H_element687  label="H_element : 451"  # scripted group (container) (typed FeaturePython)
  n = 10
  ref = H_element
FEATURE [App::DocumentObjectGroupPython] C_element737  label="C_element : 490"  # scripted group (container) (typed FeaturePython)
  n = 10
  ref = C_element
FEATURE [App::DocumentObjectGroupPython] N_element337  label="N_element : 189"  # scripted group (container) (typed FeaturePython)
  n = 5
  ref = N_element
FEATURE [App::DocumentObjectGroupPython] O_element647  label="O_element : 419"  # scripted group (container) (typed FeaturePython)
  n = 8
  ref = O_element
FEATURE [App::DocumentObjectGroupPython] P_element092  label="P_element : 036"  # scripted group (container) (typed FeaturePython)
  n = 1
  ref = P_element
FEATURE [App::DocumentObjectGroupPython] G4_DNA_G  # scripted group (container) (typed FeaturePython)
  Dunit = g/cm3
  Dvalue = 1
  Group = -> [H_element687,C_element737,N_element337,O_element647,P_element092]
  conduct = 2
  density = 1
  expand = 3
  formula = G4_DNA_G
  name = G4_DNA_G
  specific = 4
FEATURE [App::DocumentObjectGroupPython] H_element688  label="H_element : 452"  # scripted group (container) (typed FeaturePython)
  n = 10
  ref = H_element
FEATURE [App::DocumentObjectGroupPython] C_element738  label="C_element : 491"  # scripted group (container) (typed FeaturePython)
  n = 9
  ref = C_element
FEATURE [App::DocumentObjectGroupPython] N_element338  label="N_element : 190"  # scripted group (container) (typed FeaturePython)
  n = 3
  ref = N_element
FEATURE [App::DocumentObjectGroupPython] O_element648  label="O_element : 420"  # scripted group (container) (typed FeaturePython)
  n = 8
  ref = O_element
FEATURE [App::DocumentObjectGroupPython] P_element093  label="P_element : 037"  # scripted group (container) (typed FeaturePython)
  n = 1
  ref = P_element
FEATURE [App::DocumentObjectGroupPython] G4_DNA_C  # scripted group (container) (typed FeaturePython)
  Dunit = g/cm3
  Dvalue = 1
  Group = -> [H_element688,C_element738,N_element338,O_element648,P_element093]
  conduct = 2
  density = 1
  expand = 3
  formula = G4_DNA_C
  name = G4_DNA_C
  specific = 4
FEATURE [App::DocumentObjectGroupPython] H_element689  label="H_element : 453"  # scripted group (container) (typed FeaturePython)
  n = 9
  ref = H_element
FEATURE [App::DocumentObjectGroupPython] C_element739  label="C_element : 492"  # scripted group (container) (typed FeaturePython)
  n = 9
  ref = C_element
FEATURE [App::DocumentObjectGroupPython] N_element339  label="N_element : 191"  # scripted group (container) (typed FeaturePython)
  n = 2
  ref = N_element
FEATURE [App::DocumentObjectGroupPython] O_element649  label="O_element : 421"  # scripted group (container) (typed FeaturePython)
  n = 9
  ref = O_element
FEATURE [App::DocumentObjectGroupPython] P_element094  label="P_element : 038"  # scripted group (container) (typed FeaturePython)
  n = 1
  ref = P_element
FEATURE [App::DocumentObjectGroupPython] G4_DNA_U  # scripted group (container) (typed FeaturePython)
  Dunit = g/cm3
  Dvalue = 1
  Group = -> [H_element689,C_element739,N_element339,O_element649,P_element094]
  conduct = 2
  density = 1
  expand = 3
  formula = G4_DNA_U
  name = G4_DNA_U
  specific = 4
FEATURE [App::DocumentObjectGroupPython] H_element690  label="H_element : 454"  # scripted group (container) (typed FeaturePython)
  n = 11
  ref = H_element
FEATURE [App::DocumentObjectGroupPython] C_element740  label="C_element : 493"  # scripted group (container) (typed FeaturePython)
  n = 10
  ref = C_element
FEATURE [App::DocumentObjectGroupPython] N_element340  label="N_element : 192"  # scripted group (container) (typed FeaturePython)
  n = 2
  ref = N_element
FEATURE [App::DocumentObjectGroupPython] O_element650  label="O_element : 422"  # scripted group (container) (typed FeaturePython)
  n = 9
  ref = O_element
FEATURE [App::DocumentObjectGroupPython] P_element095  label="P_element : 039"  # scripted group (container) (typed FeaturePython)
  n = 1
  ref = P_element
FEATURE [App::DocumentObjectGroupPython] G4_DNA_MU  # scripted group (container) (typed FeaturePython)
  Dunit = g/cm3
  Dvalue = 1
  Group = -> [H_element690,C_element740,N_element340,O_element650,P_element095]
  conduct = 2
  density = 1
  expand = 3
  formula = G4_DNA_MU
  name = G4_DNA_MU
  specific = 4
FEATURE [App::DocumentObjectGroupPython] BioChemical  # scripted group (container) (typed FeaturePython)
  Group = -> [G4_CYTOSINE,G4_THYMINE,G4_URACIL,G4_DNA_ADENINE,G4_DNA_GUANINE,G4_DNA_CYTOSINE,G4_DNA_THYMINE,G4_DNA_URACIL,G4_DNA_ADENOSINE,G4_DNA_GUANOSINE,G4_DNA_CYTIDINE,G4_DNA_URIDINE,G4_DNA_METHYLURIDINE,G4_DNA_MONOPHOSPHATE,G4_DNA_A,G4_DNA_G,G4_DNA_C,G4_DNA_U,G4_DNA_MU]
FEATURE [App::DocumentObjectGroupPython] G4Materials  # scripted group (container) (typed FeaturePython)
  Group = -> [NIST,Element,HEP,Space,BioChemical]
FEATURE [App::DocumentObjectGroupPython] Geant4  # scripted group (container) (typed FeaturePython)
  Group = -> [G4Isotopes,G4Elements,G4Materials]
FEATURE [App::DocumentObjectGroupPython] Materials  # scripted group (container) (typed FeaturePython)
  Group = -> [Geant4]
